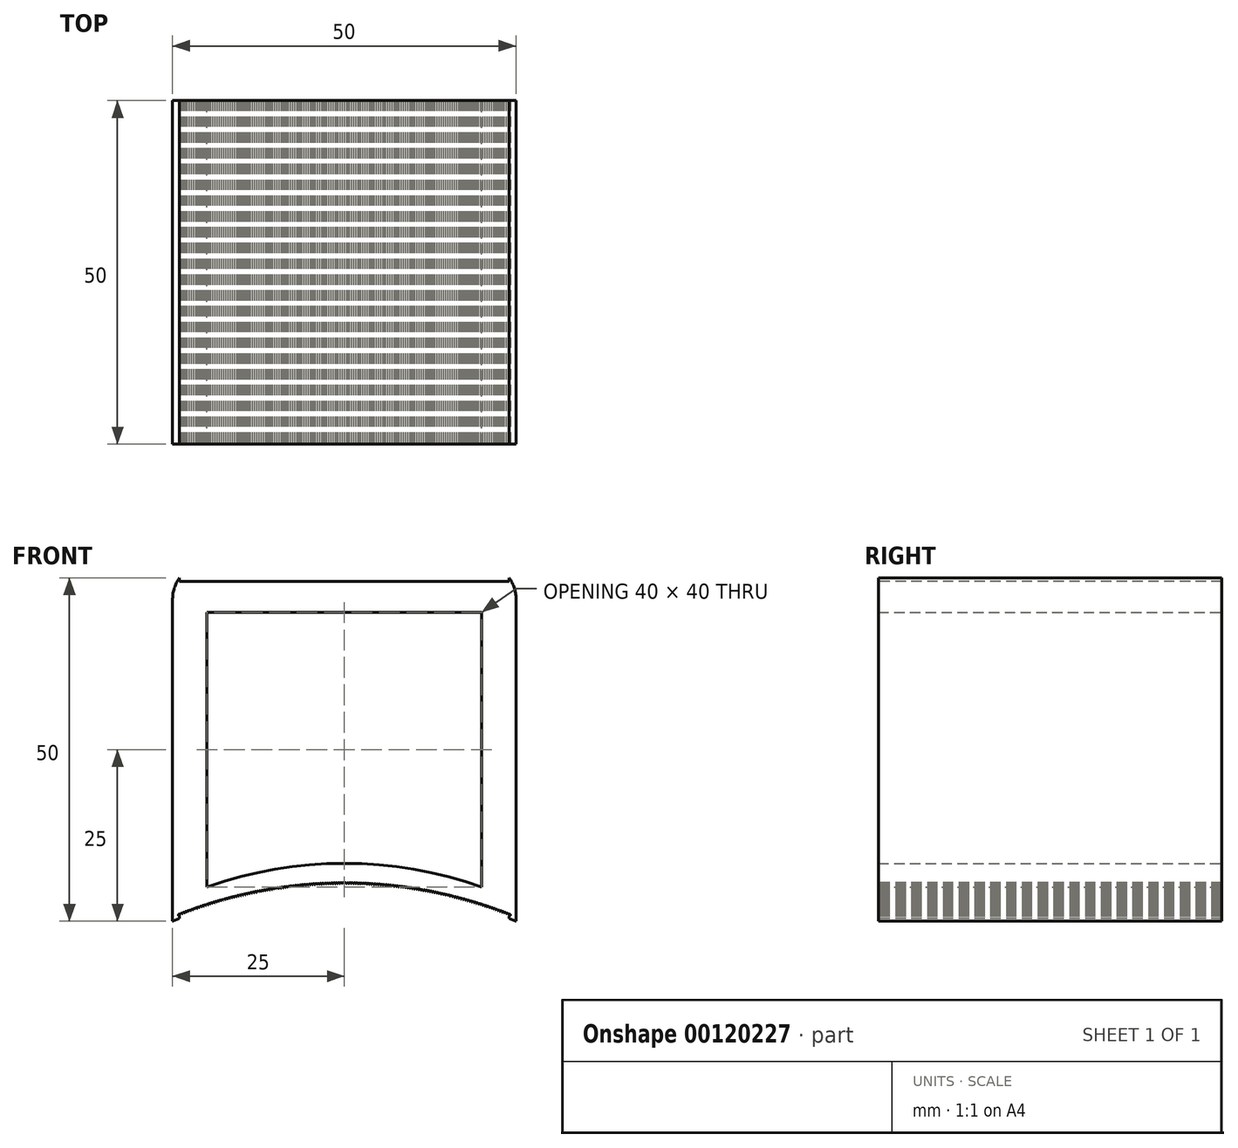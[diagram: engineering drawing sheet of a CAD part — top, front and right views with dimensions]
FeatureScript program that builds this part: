
annotation { "Feature Type Name" : "Feature", "Feature Type Description" : "" }
export const myFeature = defineFeature(function(context is Context, id is Id, definition is map)
    precondition{}
    {
        {
            var Q0;
            Q0=qCreatedBy(makeId("Front.planeOp"),FACE);
            var sketch = newSketch(context, id + "F0", { "sketchPlane" : qUnion([Q0])});
            skLineSegment(sketch, "E0.top", {"start": v(25, 25) * mm, "end": v(-25, 25) * mm});
            skLineSegment(sketch, "E0.left", {"start": v(25, -25) * mm, "end": v(25, 25) * mm});
            skLineSegment(sketch, "E0.right", {"start": v(-25, -25) * mm, "end": v(-25, 25) * mm});
            skPoint(sketch, "E0.middle", {"position": v(0, 0) * mm});
            skLineSegment(sketch, "E1.top", {"start": v(20, 20) * mm, "end": v(-20, 20) * mm});
            skLineSegment(sketch, "E1.left", {"start": v(20, -20) * mm, "end": v(20, 20) * mm});
            skLineSegment(sketch, "E1.right", {"start": v(-20, -20) * mm, "end": v(-20, 20) * mm});
            skArc(sketch, "E2", {"start": v(25, -25) * mm, "mid": v(0, -20) * mm, "end": v(-25, -25) * mm});
            skArc(sketch, "E3", {"start": v(20, -20) * mm, "mid": v(0, -16.57) * mm, "end": v(-20, -20) * mm});
            skSolve(sketch);
        }
        {
            var Q0;
            Q0=makeQuery(id+"F0.imprint","IMPRINT",FACE,{"disambiguationData":[TD([[makeQuery(id+"F0.imprint","IMPRINT",EDGE,{"derivedFrom":sQuery(id+"F0.wireOp",EDGE,"E0.top")}),1.0]])]});
            extrude(context, id + "F1", {"entities" : qUnion([Q0]), "depth" : 50 * mm});
        }
        {
            var Q0;
            Q0=makeQuery(id+"F1.opExtrude","CAP_FACE",FACE,{"disambiguationData":[OSD([sQuery(id+"F0.wireOp",EDGE,"E0.top"),sQuery(id+"F0.wireOp",EDGE,"E0.left"),sQuery(id+"F0.wireOp",EDGE,"E0.right"),sQuery(id+"F0.wireOp",EDGE,"E1.top"),sQuery(id+"F0.wireOp",EDGE,"E1.left"),sQuery(id+"F0.wireOp",EDGE,"E1.right"),sQuery(id+"F0.wireOp",EDGE,"E2"),sQuery(id+"F0.wireOp",EDGE,"E3")])],"isStart":false});
            var sketch = newSketch(context, id + "F2", { "sketchPlane" : qUnion([Q0])});
            skLineSegment(sketch, "E4", {"start": v(-24, -24.6) * mm, "end": v(-24, -24.1) * mm});
            skLineSegment(sketch, "E5", {"start": v(24, -24.6) * mm, "end": v(24, -24.1) * mm});
            skArc(sketch, "E6", {"start": v(24, -24.1) * mm, "mid": v(0, -19.54) * mm, "end": v(-24, -24.1) * mm});
            skArc(sketch, "E7", {"start": v(24, -24.6) * mm, "mid": v(0, -20) * mm, "end": v(-24, -24.6) * mm});
            skLineSegment(sketch, "E8.bottom", {"start": v(-24, 26.5) * mm, "end": v(24, 26.5) * mm});
            skLineSegment(sketch, "E8.top", {"start": v(-24, 24.5) * mm, "end": v(24, 24.5) * mm});
            skLineSegment(sketch, "E8.left", {"start": v(-24, 26.5) * mm, "end": v(-24, 24.5) * mm});
            skLineSegment(sketch, "E8.right", {"start": v(24, 26.5) * mm, "end": v(24, 24.5) * mm});
            skSolve(sketch);
        }
        {
            var Q0;
            {var subQ0=sQuery(id+"F2.wireOp",EDGE,"E8.top");Q0=makeQuery(id+"F2.imprint","IMPRINT",FACE,{"disambiguationData":[TD([[makeQuery(id+"F2.imprint","IMPRINT",EDGE,{"derivedFrom":subQ0}),1.0]])]});}
            var Q1;
            {var subQ0=sQuery(id+"F2.wireOp",EDGE,"E8.bottom");Q1=makeQuery(id+"F2.imprint","IMPRINT",FACE,{"disambiguationData":[TD([[makeQuery(id+"F2.imprint","IMPRINT",EDGE,{"derivedFrom":subQ0}),-1.0]])]});}
            var Q2;
            Q2=makeQuery(id+"F2.imprint","IMPRINT",FACE,{"disambiguationData":[TD([[makeQuery(id+"F2.imprint","IMPRINT",EDGE,{"derivedFrom":sQuery(id+"F2.wireOp",EDGE,"E4")}),-1.0]])]});
            extrude(context, id + "F3", {"entities" : qUnion([Q0, Q1, Q2]), "operationType" : NewBodyOperationType.REMOVE, "oppositeDirection" : true, "depth" : 50 * mm});
        }
        {
            var Q0;
            Q0=makeQuery(id+"F1.opExtrude","SWEPT_EDGE",EDGE,{"disambiguationData":[OSD([sQuery(id+"F0.wireOp",EDGE,"E0.top"),sQuery(id+"F0.wireOp",EDGE,"E0.left")])]});
            var Q1;
            Q1=makeQuery(id+"F1.opExtrude","SWEPT_EDGE",EDGE,{"disambiguationData":[OSD([sQuery(id+"F0.wireOp",EDGE,"E0.top"),sQuery(id+"F0.wireOp",EDGE,"E0.right")])]});
            fillet(context, id + "F4", {"entities" : qUnion([Q0, Q1]), "radius" : 5.08 * mm, "tangentPropagation" : true, "allowEdgeOverflow" : false});
        }
        {
            var Q0;
            Q0=makeQuery(id+"F1.opExtrude","CAP_FACE",FACE,{"disambiguationData":[OSD([sQuery(id+"F0.wireOp",EDGE,"E0.top"),sQuery(id+"F0.wireOp",EDGE,"E0.left"),sQuery(id+"F0.wireOp",EDGE,"E0.right"),sQuery(id+"F0.wireOp",EDGE,"E1.top"),sQuery(id+"F0.wireOp",EDGE,"E1.left"),sQuery(id+"F0.wireOp",EDGE,"E1.right"),sQuery(id+"F0.wireOp",EDGE,"E2"),sQuery(id+"F0.wireOp",EDGE,"E3")])],"isStart":false});
            var sketch = newSketch(context, id + "F5", { "sketchPlane" : qUnion([Q0])});
            skCircle(sketch, "E9", {"center": v(-24, -24.1) * mm, "radius": 0.15 * mm});
            skCircle(sketch, "E10", {"center": v(0, -85.04) * mm, "radius": 65.5 * mm, "construction": true});
            skPoint(sketch, "E10.first.point", {"position": v(-20.95, -22.98) * mm});
            skPoint(sketch, "E10.second.point", {"position": v(1.95, -19.57) * mm});
            skPoint(sketch, "E10.third.point", {"position": v(16.7, -21.7) * mm});
            skCircle(sketch, "E11.1.0", {"center": v(-23.7, -23.97) * mm, "radius": 0.15 * mm});
            skCircle(sketch, "E11.2.0", {"center": v(-23.38, -23.85) * mm, "radius": 0.15 * mm});
            skCircle(sketch, "E11.3.0", {"center": v(-23.08, -23.74) * mm, "radius": 0.15 * mm});
            skCircle(sketch, "E11.4.0", {"center": v(-22.77, -23.62) * mm, "radius": 0.15 * mm});
            skCircle(sketch, "E11.5.0", {"center": v(-22.46, -23.5) * mm, "radius": 0.15 * mm});
            skCircle(sketch, "E11.6.0", {"center": v(-22.15, -23.4) * mm, "radius": 0.15 * mm});
            skCircle(sketch, "E11.7.0", {"center": v(-21.84, -23.28) * mm, "radius": 0.15 * mm});
            skCircle(sketch, "E11.8.0", {"center": v(-21.53, -23.18) * mm, "radius": 0.15 * mm});
            skCircle(sketch, "E11.9.0", {"center": v(-21.21, -23.07) * mm, "radius": 0.15 * mm});
            skCircle(sketch, "E11.10.0", {"center": v(-20.9, -22.96) * mm, "radius": 0.15 * mm});
            skCircle(sketch, "E11.11.0", {"center": v(-20.59, -22.86) * mm, "radius": 0.15 * mm});
            skCircle(sketch, "E11.12.0", {"center": v(-20.27, -22.75) * mm, "radius": 0.15 * mm});
            skCircle(sketch, "E11.13.0", {"center": v(-19.96, -22.65) * mm, "radius": 0.15 * mm});
            skCircle(sketch, "E11.14.0", {"center": v(-19.65, -22.55) * mm, "radius": 0.15 * mm});
            skCircle(sketch, "E11.15.0", {"center": v(-19.33, -22.46) * mm, "radius": 0.15 * mm});
            skCircle(sketch, "E11.16.0", {"center": v(-19.02, -22.36) * mm, "radius": 0.15 * mm});
            skCircle(sketch, "E11.17.0", {"center": v(-18.7, -22.26) * mm, "radius": 0.15 * mm});
            skCircle(sketch, "E11.18.0", {"center": v(-18.38, -22.17) * mm, "radius": 0.15 * mm});
            skCircle(sketch, "E11.19.0", {"center": v(-18.07, -22.08) * mm, "radius": 0.15 * mm});
            skCircle(sketch, "E11.20.0", {"center": v(-17.75, -21.99) * mm, "radius": 0.15 * mm});
            skCircle(sketch, "E11.21.0", {"center": v(-17.43, -21.9) * mm, "radius": 0.15 * mm});
            skCircle(sketch, "E11.22.0", {"center": v(-17.11, -21.81) * mm, "radius": 0.15 * mm});
            skCircle(sketch, "E11.23.0", {"center": v(-16.8, -21.73) * mm, "radius": 0.15 * mm});
            skCircle(sketch, "E11.24.0", {"center": v(-16.48, -21.64) * mm, "radius": 0.15 * mm});
            skCircle(sketch, "E11.25.0", {"center": v(-16.16, -21.56) * mm, "radius": 0.15 * mm});
            skCircle(sketch, "E11.26.0", {"center": v(-15.84, -21.48) * mm, "radius": 0.15 * mm});
            skCircle(sketch, "E11.27.0", {"center": v(-15.52, -21.4) * mm, "radius": 0.15 * mm});
            skCircle(sketch, "E11.28.0", {"center": v(-15.2, -21.32) * mm, "radius": 0.15 * mm});
            skCircle(sketch, "E11.29.0", {"center": v(-14.87, -21.25) * mm, "radius": 0.15 * mm});
            skCircle(sketch, "E11.30.0", {"center": v(-14.55, -21.17) * mm, "radius": 0.15 * mm});
            skCircle(sketch, "E11.31.0", {"center": v(-14.23, -21.1) * mm, "radius": 0.15 * mm});
            skCircle(sketch, "E11.32.0", {"center": v(-13.9, -21.03) * mm, "radius": 0.15 * mm});
            skCircle(sketch, "E11.33.0", {"center": v(-13.59, -20.96) * mm, "radius": 0.15 * mm});
            skCircle(sketch, "E11.34.0", {"center": v(-13.26, -20.9) * mm, "radius": 0.15 * mm});
            skCircle(sketch, "E11.35.0", {"center": v(-12.94, -20.83) * mm, "radius": 0.15 * mm});
            skCircle(sketch, "E11.36.0", {"center": v(-12.62, -20.76) * mm, "radius": 0.15 * mm});
            skCircle(sketch, "E11.37.0", {"center": v(-12.3, -20.7) * mm, "radius": 0.15 * mm});
            skCircle(sketch, "E11.38.0", {"center": v(-11.97, -20.64) * mm, "radius": 0.15 * mm});
            skCircle(sketch, "E11.39.0", {"center": v(-11.64, -20.58) * mm, "radius": 0.15 * mm});
            skCircle(sketch, "E11.40.0", {"center": v(-11.32, -20.52) * mm, "radius": 0.15 * mm});
            skCircle(sketch, "E11.41.0", {"center": v(-11, -20.47) * mm, "radius": 0.15 * mm});
            skCircle(sketch, "E11.42.0", {"center": v(-10.67, -20.41) * mm, "radius": 0.15 * mm});
            skCircle(sketch, "E11.43.0", {"center": v(-10.34, -20.36) * mm, "radius": 0.15 * mm});
            skCircle(sketch, "E11.44.0", {"center": v(-10.02, -20.3) * mm, "radius": 0.15 * mm});
            skCircle(sketch, "E11.45.0", {"center": v(-9.7, -20.26) * mm, "radius": 0.15 * mm});
            skCircle(sketch, "E11.46.0", {"center": v(-9.36, -20.21) * mm, "radius": 0.15 * mm});
            skCircle(sketch, "E11.47.0", {"center": v(-9.04, -20.16) * mm, "radius": 0.15 * mm});
            skCircle(sketch, "E11.48.0", {"center": v(-8.71, -20.12) * mm, "radius": 0.15 * mm});
            skCircle(sketch, "E11.49.0", {"center": v(-8.38, -20.08) * mm, "radius": 0.15 * mm});
            skLineSegment(sketch, "E11.anchor1", {"start": v(0, -85.04) * mm, "end": v(-24, -24.1) * mm, "construction": true});
            skLineSegment(sketch, "E11.anchor2", {"start": v(0, -85.04) * mm, "end": v(24.01, -24.1) * mm, "construction": true});
            skCircle(sketch, "E12.1.50.0", {"center": v(-8.06, -20.04) * mm, "radius": 0.15 * mm});
            skCircle(sketch, "E12.1.51.0", {"center": v(-7.73, -20) * mm, "radius": 0.15 * mm});
            skCircle(sketch, "E12.1.52.0", {"center": v(-7.4, -19.96) * mm, "radius": 0.15 * mm});
            skCircle(sketch, "E12.1.53.0", {"center": v(-7.07, -19.92) * mm, "radius": 0.15 * mm});
            skCircle(sketch, "E12.1.54.0", {"center": v(-6.74, -19.89) * mm, "radius": 0.15 * mm});
            skCircle(sketch, "E12.1.55.0", {"center": v(-6.42, -19.85) * mm, "radius": 0.15 * mm});
            skCircle(sketch, "E12.1.56.0", {"center": v(-6.09, -19.82) * mm, "radius": 0.15 * mm});
            skCircle(sketch, "E12.1.57.0", {"center": v(-5.76, -19.8) * mm, "radius": 0.15 * mm});
            skCircle(sketch, "E12.1.58.0", {"center": v(-5.43, -19.76) * mm, "radius": 0.15 * mm});
            skCircle(sketch, "E12.1.59.0", {"center": v(-5.1, -19.74) * mm, "radius": 0.15 * mm});
            skCircle(sketch, "E12.1.60.0", {"center": v(-4.77, -19.71) * mm, "radius": 0.15 * mm});
            skCircle(sketch, "E12.1.61.0", {"center": v(-4.44, -19.69) * mm, "radius": 0.15 * mm});
            skCircle(sketch, "E12.1.62.0", {"center": v(-4.11, -19.67) * mm, "radius": 0.15 * mm});
            skCircle(sketch, "E12.1.63.0", {"center": v(-3.79, -19.65) * mm, "radius": 0.15 * mm});
            skCircle(sketch, "E12.1.64.0", {"center": v(-3.46, -19.63) * mm, "radius": 0.15 * mm});
            skCircle(sketch, "E12.1.65.0", {"center": v(-3.13, -19.61) * mm, "radius": 0.15 * mm});
            skCircle(sketch, "E12.1.66.0", {"center": v(-2.8, -19.6) * mm, "radius": 0.15 * mm});
            skCircle(sketch, "E12.1.67.0", {"center": v(-2.47, -19.58) * mm, "radius": 0.15 * mm});
            skCircle(sketch, "E12.1.68.0", {"center": v(-2.14, -19.57) * mm, "radius": 0.15 * mm});
            skCircle(sketch, "E12.1.69.0", {"center": v(-1.8, -19.56) * mm, "radius": 0.15 * mm});
            skCircle(sketch, "E12.1.70.0", {"center": v(-1.48, -19.55) * mm, "radius": 0.15 * mm});
            skCircle(sketch, "E12.1.71.0", {"center": v(-1.15, -19.55) * mm, "radius": 0.15 * mm});
            skCircle(sketch, "E12.1.72.0", {"center": v(-0.82, -19.54) * mm, "radius": 0.15 * mm});
            skCircle(sketch, "E12.1.73.0", {"center": v(-0.49, -19.54) * mm, "radius": 0.15 * mm});
            skCircle(sketch, "E12.1.74.0", {"center": v(-0.16, -19.54) * mm, "radius": 0.15 * mm});
            skCircle(sketch, "E12.1.75.0", {"center": v(0.17, -19.54) * mm, "radius": 0.15 * mm});
            skCircle(sketch, "E12.1.76.0", {"center": v(0.5, -19.54) * mm, "radius": 0.15 * mm});
            skCircle(sketch, "E12.1.77.0", {"center": v(0.83, -19.54) * mm, "radius": 0.15 * mm});
            skCircle(sketch, "E12.1.78.0", {"center": v(1.16, -19.55) * mm, "radius": 0.15 * mm});
            skCircle(sketch, "E12.1.79.0", {"center": v(1.5, -19.55) * mm, "radius": 0.15 * mm});
            skCircle(sketch, "E12.1.80.0", {"center": v(1.82, -19.56) * mm, "radius": 0.15 * mm});
            skCircle(sketch, "E12.1.81.0", {"center": v(2.15, -19.57) * mm, "radius": 0.15 * mm});
            skCircle(sketch, "E12.1.82.0", {"center": v(2.48, -19.58) * mm, "radius": 0.15 * mm});
            skCircle(sketch, "E12.1.83.0", {"center": v(2.8, -19.6) * mm, "radius": 0.15 * mm});
            skCircle(sketch, "E12.1.84.0", {"center": v(3.14, -19.61) * mm, "radius": 0.15 * mm});
            skCircle(sketch, "E12.1.85.0", {"center": v(3.47, -19.63) * mm, "radius": 0.15 * mm});
            skCircle(sketch, "E12.1.86.0", {"center": v(3.8, -19.65) * mm, "radius": 0.15 * mm});
            skCircle(sketch, "E12.1.87.0", {"center": v(4.13, -19.67) * mm, "radius": 0.15 * mm});
            skCircle(sketch, "E12.1.88.0", {"center": v(4.46, -19.69) * mm, "radius": 0.15 * mm});
            skCircle(sketch, "E12.1.89.0", {"center": v(4.79, -19.71) * mm, "radius": 0.15 * mm});
            skCircle(sketch, "E12.1.90.0", {"center": v(5.11, -19.74) * mm, "radius": 0.15 * mm});
            skCircle(sketch, "E12.1.91.0", {"center": v(5.44, -19.76) * mm, "radius": 0.15 * mm});
            skCircle(sketch, "E12.1.92.0", {"center": v(5.77, -19.8) * mm, "radius": 0.15 * mm});
            skCircle(sketch, "E12.1.93.0", {"center": v(6.1, -19.82) * mm, "radius": 0.15 * mm});
            skCircle(sketch, "E12.1.94.0", {"center": v(6.43, -19.85) * mm, "radius": 0.15 * mm});
            skCircle(sketch, "E12.1.95.0", {"center": v(6.76, -19.89) * mm, "radius": 0.15 * mm});
            skCircle(sketch, "E12.1.96.0", {"center": v(7.09, -19.92) * mm, "radius": 0.15 * mm});
            skCircle(sketch, "E12.1.97.0", {"center": v(7.41, -19.96) * mm, "radius": 0.15 * mm});
            skCircle(sketch, "E12.1.98.0", {"center": v(7.74, -20) * mm, "radius": 0.15 * mm});
            skCircle(sketch, "E12.1.99.0", {"center": v(8.07, -20.04) * mm, "radius": 0.15 * mm});
            skCircle(sketch, "E12.1.100.0", {"center": v(8.4, -20.08) * mm, "radius": 0.15 * mm});
            skCircle(sketch, "E12.1.101.0", {"center": v(8.72, -20.12) * mm, "radius": 0.15 * mm});
            skCircle(sketch, "E12.1.102.0", {"center": v(9.05, -20.17) * mm, "radius": 0.15 * mm});
            skCircle(sketch, "E12.1.103.0", {"center": v(9.38, -20.21) * mm, "radius": 0.15 * mm});
            skCircle(sketch, "E12.1.104.0", {"center": v(9.7, -20.26) * mm, "radius": 0.15 * mm});
            skCircle(sketch, "E12.1.105.0", {"center": v(10.03, -20.31) * mm, "radius": 0.15 * mm});
            skCircle(sketch, "E12.1.106.0", {"center": v(10.35, -20.36) * mm, "radius": 0.15 * mm});
            skCircle(sketch, "E12.1.107.0", {"center": v(10.68, -20.41) * mm, "radius": 0.15 * mm});
            skCircle(sketch, "E12.1.108.0", {"center": v(11, -20.47) * mm, "radius": 0.15 * mm});
            skCircle(sketch, "E12.1.109.0", {"center": v(11.33, -20.53) * mm, "radius": 0.15 * mm});
            skCircle(sketch, "E12.1.110.0", {"center": v(11.66, -20.58) * mm, "radius": 0.15 * mm});
            skCircle(sketch, "E12.1.111.0", {"center": v(11.98, -20.64) * mm, "radius": 0.15 * mm});
            skCircle(sketch, "E12.1.112.0", {"center": v(12.3, -20.7) * mm, "radius": 0.15 * mm});
            skCircle(sketch, "E12.1.113.0", {"center": v(12.63, -20.77) * mm, "radius": 0.15 * mm});
            skCircle(sketch, "E12.1.114.0", {"center": v(12.95, -20.83) * mm, "radius": 0.15 * mm});
            skCircle(sketch, "E12.1.115.0", {"center": v(13.28, -20.9) * mm, "radius": 0.15 * mm});
            skCircle(sketch, "E12.1.116.0", {"center": v(13.6, -20.96) * mm, "radius": 0.15 * mm});
            skCircle(sketch, "E12.1.117.0", {"center": v(13.92, -21.03) * mm, "radius": 0.15 * mm});
            skCircle(sketch, "E12.1.118.0", {"center": v(14.24, -21.1) * mm, "radius": 0.15 * mm});
            skCircle(sketch, "E12.1.119.0", {"center": v(14.56, -21.18) * mm, "radius": 0.15 * mm});
            skCircle(sketch, "E12.1.120.0", {"center": v(14.89, -21.25) * mm, "radius": 0.15 * mm});
            skCircle(sketch, "E12.1.121.0", {"center": v(15.2, -21.33) * mm, "radius": 0.15 * mm});
            skCircle(sketch, "E12.1.122.0", {"center": v(15.53, -21.4) * mm, "radius": 0.15 * mm});
            skCircle(sketch, "E12.1.123.0", {"center": v(15.85, -21.48) * mm, "radius": 0.15 * mm});
            skCircle(sketch, "E12.1.124.0", {"center": v(16.17, -21.56) * mm, "radius": 0.15 * mm});
            skCircle(sketch, "E12.1.125.0", {"center": v(16.49, -21.65) * mm, "radius": 0.15 * mm});
            skCircle(sketch, "E12.1.126.0", {"center": v(16.8, -21.73) * mm, "radius": 0.15 * mm});
            skCircle(sketch, "E12.1.127.0", {"center": v(17.13, -21.82) * mm, "radius": 0.15 * mm});
            skCircle(sketch, "E12.1.128.0", {"center": v(17.44, -21.9) * mm, "radius": 0.15 * mm});
            skCircle(sketch, "E12.1.129.0", {"center": v(17.76, -22) * mm, "radius": 0.15 * mm});
            skCircle(sketch, "E12.1.130.0", {"center": v(18.08, -22.08) * mm, "radius": 0.15 * mm});
            skCircle(sketch, "E12.1.131.0", {"center": v(18.4, -22.17) * mm, "radius": 0.15 * mm});
            skCircle(sketch, "E12.1.132.0", {"center": v(18.71, -22.27) * mm, "radius": 0.15 * mm});
            skCircle(sketch, "E12.1.133.0", {"center": v(19.03, -22.36) * mm, "radius": 0.15 * mm});
            skCircle(sketch, "E12.1.134.0", {"center": v(19.34, -22.46) * mm, "radius": 0.15 * mm});
            skCircle(sketch, "E12.1.135.0", {"center": v(19.66, -22.56) * mm, "radius": 0.15 * mm});
            skCircle(sketch, "E12.1.136.0", {"center": v(19.97, -22.66) * mm, "radius": 0.15 * mm});
            skCircle(sketch, "E12.1.137.0", {"center": v(20.29, -22.76) * mm, "radius": 0.15 * mm});
            skCircle(sketch, "E12.1.138.0", {"center": v(20.6, -22.86) * mm, "radius": 0.15 * mm});
            skCircle(sketch, "E12.1.139.0", {"center": v(20.91, -22.97) * mm, "radius": 0.15 * mm});
            skCircle(sketch, "E12.1.140.0", {"center": v(21.23, -23.07) * mm, "radius": 0.15 * mm});
            skCircle(sketch, "E12.1.141.0", {"center": v(21.54, -23.18) * mm, "radius": 0.15 * mm});
            skCircle(sketch, "E12.1.142.0", {"center": v(21.85, -23.29) * mm, "radius": 0.15 * mm});
            skCircle(sketch, "E12.1.143.0", {"center": v(22.16, -23.4) * mm, "radius": 0.15 * mm});
            skCircle(sketch, "E12.1.144.0", {"center": v(22.47, -23.51) * mm, "radius": 0.15 * mm});
            skCircle(sketch, "E12.1.145.0", {"center": v(22.78, -23.63) * mm, "radius": 0.15 * mm});
            skCircle(sketch, "E12.1.146.0", {"center": v(23.09, -23.74) * mm, "radius": 0.15 * mm});
            skCircle(sketch, "E12.1.147.0", {"center": v(23.4, -23.86) * mm, "radius": 0.15 * mm});
            skCircle(sketch, "E12.1.148.0", {"center": v(23.7, -23.98) * mm, "radius": 0.15 * mm});
            skCircle(sketch, "E12.1.149.0", {"center": v(24.01, -24.1) * mm, "radius": 0.15 * mm});
            skSolve(sketch);
        }
        {
            var Q0;
            {var subQ0=sQuery(id+"F5.wireOp",EDGE,"E11.4.0");var subQ1=makeQuery(id+"F3.boolean.opBoolean","COPY",EDGE,{"derivedFrom":makeQuery(id+"F3.opExtrude","CAP_EDGE",EDGE,{"disambiguationData":[OSD([sQuery(id+"F2.wireOp",EDGE,"E6")])],"isStart":true})});var subQ2=makeQuery(id+"F5.imprint","INTERSECT",VERTEX,{"disambiguationData":[OD(0.0)],"derivedFrom":[subQ1,subQ0]});Q0=makeQuery(id+"F5.imprint","IMPRINT",FACE,{"disambiguationData":[TD([[makeQuery(id+"F5.imprint","IMPRINT",EDGE,{"disambiguationData":[TD([[subQ2,-1.0]])],"derivedFrom":subQ0}),1.0]])]});}
            var Q1;
            {var subQ0=sQuery(id+"F5.wireOp",EDGE,"E11.3.0");var subQ1=makeQuery(id+"F3.boolean.opBoolean","COPY",EDGE,{"derivedFrom":makeQuery(id+"F3.opExtrude","CAP_EDGE",EDGE,{"disambiguationData":[OSD([sQuery(id+"F2.wireOp",EDGE,"E6")])],"isStart":true})});var subQ2=makeQuery(id+"F5.imprint","INTERSECT",VERTEX,{"disambiguationData":[OD(0.0)],"derivedFrom":[subQ1,subQ0]});Q1=makeQuery(id+"F5.imprint","IMPRINT",FACE,{"disambiguationData":[TD([[makeQuery(id+"F5.imprint","IMPRINT",EDGE,{"disambiguationData":[TD([[subQ2,-1.0]])],"derivedFrom":subQ0}),1.0]])]});}
            var Q2;
            {var subQ0=sQuery(id+"F5.wireOp",EDGE,"E11.2.0");var subQ1=makeQuery(id+"F3.boolean.opBoolean","COPY",EDGE,{"derivedFrom":makeQuery(id+"F3.opExtrude","CAP_EDGE",EDGE,{"disambiguationData":[OSD([sQuery(id+"F2.wireOp",EDGE,"E6")])],"isStart":true})});var subQ2=makeQuery(id+"F5.imprint","INTERSECT",VERTEX,{"disambiguationData":[OD(0.0)],"derivedFrom":[subQ1,subQ0]});Q2=makeQuery(id+"F5.imprint","IMPRINT",FACE,{"disambiguationData":[TD([[makeQuery(id+"F5.imprint","IMPRINT",EDGE,{"disambiguationData":[TD([[subQ2,-1.0]])],"derivedFrom":subQ0}),1.0]])]});}
            var Q3;
            {var subQ0=sQuery(id+"F5.wireOp",EDGE,"E11.1.0");var subQ1=makeQuery(id+"F3.boolean.opBoolean","COPY",EDGE,{"derivedFrom":makeQuery(id+"F3.opExtrude","CAP_EDGE",EDGE,{"disambiguationData":[OSD([sQuery(id+"F2.wireOp",EDGE,"E6")])],"isStart":true})});var subQ2=makeQuery(id+"F5.imprint","INTERSECT",VERTEX,{"disambiguationData":[OD(0.0)],"derivedFrom":[subQ1,subQ0]});Q3=makeQuery(id+"F5.imprint","IMPRINT",FACE,{"disambiguationData":[TD([[makeQuery(id+"F5.imprint","IMPRINT",EDGE,{"disambiguationData":[TD([[subQ2,-1.0]])],"derivedFrom":subQ0}),1.0]])]});}
            var Q4;
            {var subQ0=sQuery(id+"F5.wireOp",EDGE,"E11.1.0");var subQ1=makeQuery(id+"F3.boolean.opBoolean","COPY",EDGE,{"derivedFrom":makeQuery(id+"F3.opExtrude","CAP_EDGE",EDGE,{"disambiguationData":[OSD([sQuery(id+"F2.wireOp",EDGE,"E6")])],"isStart":true})});var subQ2=makeQuery(id+"F5.imprint","INTERSECT",VERTEX,{"disambiguationData":[OD(0.0)],"derivedFrom":[subQ1,subQ0]});Q4=makeQuery(id+"F5.imprint","IMPRINT",FACE,{"disambiguationData":[TD([[makeQuery(id+"F5.imprint","IMPRINT",EDGE,{"disambiguationData":[TD([[subQ2,1.0]])],"derivedFrom":subQ0}),1.0]])]});}
            var Q5;
            {var subQ0=sQuery(id+"F5.wireOp",EDGE,"E11.2.0");var subQ1=makeQuery(id+"F3.boolean.opBoolean","COPY",EDGE,{"derivedFrom":makeQuery(id+"F3.opExtrude","CAP_EDGE",EDGE,{"disambiguationData":[OSD([sQuery(id+"F2.wireOp",EDGE,"E6")])],"isStart":true})});var subQ2=makeQuery(id+"F5.imprint","INTERSECT",VERTEX,{"disambiguationData":[OD(0.0)],"derivedFrom":[subQ1,subQ0]});Q5=makeQuery(id+"F5.imprint","IMPRINT",FACE,{"disambiguationData":[TD([[makeQuery(id+"F5.imprint","IMPRINT",EDGE,{"disambiguationData":[TD([[subQ2,1.0]])],"derivedFrom":subQ0}),1.0]])]});}
            var Q6;
            {var subQ0=sQuery(id+"F5.wireOp",EDGE,"E11.3.0");var subQ1=makeQuery(id+"F3.boolean.opBoolean","COPY",EDGE,{"derivedFrom":makeQuery(id+"F3.opExtrude","CAP_EDGE",EDGE,{"disambiguationData":[OSD([sQuery(id+"F2.wireOp",EDGE,"E6")])],"isStart":true})});var subQ2=makeQuery(id+"F5.imprint","INTERSECT",VERTEX,{"disambiguationData":[OD(0.0)],"derivedFrom":[subQ1,subQ0]});Q6=makeQuery(id+"F5.imprint","IMPRINT",FACE,{"disambiguationData":[TD([[makeQuery(id+"F5.imprint","IMPRINT",EDGE,{"disambiguationData":[TD([[subQ2,1.0]])],"derivedFrom":subQ0}),1.0]])]});}
            var Q7;
            {var subQ0=sQuery(id+"F5.wireOp",EDGE,"E9");var subQ1=makeQuery(id+"F3.boolean.opBoolean","COPY",EDGE,{"derivedFrom":makeQuery(id+"F3.opExtrude","CAP_EDGE",EDGE,{"disambiguationData":[OSD([sQuery(id+"F2.wireOp",EDGE,"E4")])],"isStart":true})});var subQ2=makeQuery(id+"F5.imprint","INTERSECT",VERTEX,{"derivedFrom":[subQ1,subQ0]});Q7=makeQuery(id+"F5.imprint","IMPRINT",FACE,{"disambiguationData":[TD([[makeQuery(id+"F5.imprint","IMPRINT",EDGE,{"disambiguationData":[TD([[subQ2,-1.0]])],"derivedFrom":subQ0}),1.0]])]});}
            var Q8;
            {var subQ0=sQuery(id+"F5.wireOp",EDGE,"E9");var subQ1=makeQuery(id+"F3.boolean.opBoolean","COPY",EDGE,{"derivedFrom":makeQuery(id+"F3.opExtrude","CAP_EDGE",EDGE,{"disambiguationData":[OSD([sQuery(id+"F2.wireOp",EDGE,"E4")])],"isStart":true})});var subQ2=makeQuery(id+"F5.imprint","INTERSECT",VERTEX,{"derivedFrom":[subQ1,subQ0]});Q8=makeQuery(id+"F5.imprint","IMPRINT",FACE,{"disambiguationData":[TD([[makeQuery(id+"F5.imprint","IMPRINT",EDGE,{"disambiguationData":[TD([[subQ2,1.0]])],"derivedFrom":subQ0}),1.0]])]});}
            var Q9;
            {var subQ0=sQuery(id+"F5.wireOp",EDGE,"E11.13.0");var subQ1=makeQuery(id+"F3.boolean.opBoolean","COPY",EDGE,{"derivedFrom":makeQuery(id+"F3.opExtrude","CAP_EDGE",EDGE,{"disambiguationData":[OSD([sQuery(id+"F2.wireOp",EDGE,"E6")])],"isStart":true})});var subQ2=makeQuery(id+"F5.imprint","INTERSECT",VERTEX,{"disambiguationData":[OD(0.0)],"derivedFrom":[subQ1,subQ0]});Q9=makeQuery(id+"F5.imprint","IMPRINT",FACE,{"disambiguationData":[TD([[makeQuery(id+"F5.imprint","IMPRINT",EDGE,{"disambiguationData":[TD([[subQ2,1.0]])],"derivedFrom":subQ0}),1.0]])]});}
            var Q10;
            {var subQ0=sQuery(id+"F5.wireOp",EDGE,"E11.14.0");var subQ1=makeQuery(id+"F3.boolean.opBoolean","COPY",EDGE,{"derivedFrom":makeQuery(id+"F3.opExtrude","CAP_EDGE",EDGE,{"disambiguationData":[OSD([sQuery(id+"F2.wireOp",EDGE,"E6")])],"isStart":true})});var subQ2=makeQuery(id+"F5.imprint","INTERSECT",VERTEX,{"disambiguationData":[OD(0.0)],"derivedFrom":[subQ1,subQ0]});Q10=makeQuery(id+"F5.imprint","IMPRINT",FACE,{"disambiguationData":[TD([[makeQuery(id+"F5.imprint","IMPRINT",EDGE,{"disambiguationData":[TD([[subQ2,1.0]])],"derivedFrom":subQ0}),1.0]])]});}
            var Q11;
            {var subQ0=sQuery(id+"F5.wireOp",EDGE,"E11.30.0");var subQ1=makeQuery(id+"F3.boolean.opBoolean","COPY",EDGE,{"derivedFrom":makeQuery(id+"F3.opExtrude","CAP_EDGE",EDGE,{"disambiguationData":[OSD([sQuery(id+"F2.wireOp",EDGE,"E6")])],"isStart":true})});var subQ2=makeQuery(id+"F5.imprint","INTERSECT",VERTEX,{"disambiguationData":[OD(0.0)],"derivedFrom":[subQ1,subQ0]});Q11=makeQuery(id+"F5.imprint","IMPRINT",FACE,{"disambiguationData":[TD([[makeQuery(id+"F5.imprint","IMPRINT",EDGE,{"disambiguationData":[TD([[subQ2,-1.0]])],"derivedFrom":subQ0}),1.0]])]});}
            var Q12;
            {var subQ0=sQuery(id+"F5.wireOp",EDGE,"E11.13.0");var subQ1=makeQuery(id+"F3.boolean.opBoolean","COPY",EDGE,{"derivedFrom":makeQuery(id+"F3.opExtrude","CAP_EDGE",EDGE,{"disambiguationData":[OSD([sQuery(id+"F2.wireOp",EDGE,"E6")])],"isStart":true})});var subQ2=makeQuery(id+"F5.imprint","INTERSECT",VERTEX,{"disambiguationData":[OD(0.0)],"derivedFrom":[subQ1,subQ0]});Q12=makeQuery(id+"F5.imprint","IMPRINT",FACE,{"disambiguationData":[TD([[makeQuery(id+"F5.imprint","IMPRINT",EDGE,{"disambiguationData":[TD([[subQ2,-1.0]])],"derivedFrom":subQ0}),1.0]])]});}
            var Q13;
            {var subQ0=sQuery(id+"F5.wireOp",EDGE,"E11.15.0");var subQ1=makeQuery(id+"F3.boolean.opBoolean","COPY",EDGE,{"derivedFrom":makeQuery(id+"F3.opExtrude","CAP_EDGE",EDGE,{"disambiguationData":[OSD([sQuery(id+"F2.wireOp",EDGE,"E6")])],"isStart":true})});var subQ2=makeQuery(id+"F5.imprint","INTERSECT",VERTEX,{"disambiguationData":[OD(0.0)],"derivedFrom":[subQ1,subQ0]});Q13=makeQuery(id+"F5.imprint","IMPRINT",FACE,{"disambiguationData":[TD([[makeQuery(id+"F5.imprint","IMPRINT",EDGE,{"disambiguationData":[TD([[subQ2,1.0]])],"derivedFrom":subQ0}),1.0]])]});}
            var Q14;
            {var subQ0=sQuery(id+"F5.wireOp",EDGE,"E11.18.0");var subQ1=makeQuery(id+"F3.boolean.opBoolean","COPY",EDGE,{"derivedFrom":makeQuery(id+"F3.opExtrude","CAP_EDGE",EDGE,{"disambiguationData":[OSD([sQuery(id+"F2.wireOp",EDGE,"E6")])],"isStart":true})});var subQ2=makeQuery(id+"F5.imprint","INTERSECT",VERTEX,{"disambiguationData":[OD(0.0)],"derivedFrom":[subQ1,subQ0]});Q14=makeQuery(id+"F5.imprint","IMPRINT",FACE,{"disambiguationData":[TD([[makeQuery(id+"F5.imprint","IMPRINT",EDGE,{"disambiguationData":[TD([[subQ2,1.0]])],"derivedFrom":subQ0}),1.0]])]});}
            var Q15;
            {var subQ0=sQuery(id+"F5.wireOp",EDGE,"E11.35.0");var subQ1=makeQuery(id+"F3.boolean.opBoolean","COPY",EDGE,{"derivedFrom":makeQuery(id+"F3.opExtrude","CAP_EDGE",EDGE,{"disambiguationData":[OSD([sQuery(id+"F2.wireOp",EDGE,"E6")])],"isStart":true})});var subQ2=makeQuery(id+"F5.imprint","INTERSECT",VERTEX,{"disambiguationData":[OD(0.0)],"derivedFrom":[subQ1,subQ0]});Q15=makeQuery(id+"F5.imprint","IMPRINT",FACE,{"disambiguationData":[TD([[makeQuery(id+"F5.imprint","IMPRINT",EDGE,{"disambiguationData":[TD([[subQ2,1.0]])],"derivedFrom":subQ0}),1.0]])]});}
            var Q16;
            {var subQ0=sQuery(id+"F5.wireOp",EDGE,"E11.24.0");var subQ1=makeQuery(id+"F3.boolean.opBoolean","COPY",EDGE,{"derivedFrom":makeQuery(id+"F3.opExtrude","CAP_EDGE",EDGE,{"disambiguationData":[OSD([sQuery(id+"F2.wireOp",EDGE,"E6")])],"isStart":true})});var subQ2=makeQuery(id+"F5.imprint","INTERSECT",VERTEX,{"disambiguationData":[OD(0.0)],"derivedFrom":[subQ1,subQ0]});Q16=makeQuery(id+"F5.imprint","IMPRINT",FACE,{"disambiguationData":[TD([[makeQuery(id+"F5.imprint","IMPRINT",EDGE,{"disambiguationData":[TD([[subQ2,-1.0]])],"derivedFrom":subQ0}),1.0]])]});}
            var Q17;
            {var subQ0=sQuery(id+"F5.wireOp",EDGE,"E11.21.0");var subQ1=makeQuery(id+"F3.boolean.opBoolean","COPY",EDGE,{"derivedFrom":makeQuery(id+"F3.opExtrude","CAP_EDGE",EDGE,{"disambiguationData":[OSD([sQuery(id+"F2.wireOp",EDGE,"E6")])],"isStart":true})});var subQ2=makeQuery(id+"F5.imprint","INTERSECT",VERTEX,{"disambiguationData":[OD(0.0)],"derivedFrom":[subQ1,subQ0]});Q17=makeQuery(id+"F5.imprint","IMPRINT",FACE,{"disambiguationData":[TD([[makeQuery(id+"F5.imprint","IMPRINT",EDGE,{"disambiguationData":[TD([[subQ2,1.0]])],"derivedFrom":subQ0}),1.0]])]});}
            var Q18;
            {var subQ0=sQuery(id+"F5.wireOp",EDGE,"E11.22.0");var subQ1=makeQuery(id+"F3.boolean.opBoolean","COPY",EDGE,{"derivedFrom":makeQuery(id+"F3.opExtrude","CAP_EDGE",EDGE,{"disambiguationData":[OSD([sQuery(id+"F2.wireOp",EDGE,"E6")])],"isStart":true})});var subQ2=makeQuery(id+"F5.imprint","INTERSECT",VERTEX,{"disambiguationData":[OD(0.0)],"derivedFrom":[subQ1,subQ0]});Q18=makeQuery(id+"F5.imprint","IMPRINT",FACE,{"disambiguationData":[TD([[makeQuery(id+"F5.imprint","IMPRINT",EDGE,{"disambiguationData":[TD([[subQ2,1.0]])],"derivedFrom":subQ0}),1.0]])]});}
            var Q19;
            {var subQ0=sQuery(id+"F5.wireOp",EDGE,"E11.29.0");var subQ1=makeQuery(id+"F3.boolean.opBoolean","COPY",EDGE,{"derivedFrom":makeQuery(id+"F3.opExtrude","CAP_EDGE",EDGE,{"disambiguationData":[OSD([sQuery(id+"F2.wireOp",EDGE,"E6")])],"isStart":true})});var subQ2=makeQuery(id+"F5.imprint","INTERSECT",VERTEX,{"disambiguationData":[OD(0.0)],"derivedFrom":[subQ1,subQ0]});Q19=makeQuery(id+"F5.imprint","IMPRINT",FACE,{"disambiguationData":[TD([[makeQuery(id+"F5.imprint","IMPRINT",EDGE,{"disambiguationData":[TD([[subQ2,1.0]])],"derivedFrom":subQ0}),1.0]])]});}
            var Q20;
            {var subQ0=sQuery(id+"F5.wireOp",EDGE,"E11.9.0");var subQ1=makeQuery(id+"F3.boolean.opBoolean","COPY",EDGE,{"derivedFrom":makeQuery(id+"F3.opExtrude","CAP_EDGE",EDGE,{"disambiguationData":[OSD([sQuery(id+"F2.wireOp",EDGE,"E6")])],"isStart":true})});var subQ2=makeQuery(id+"F5.imprint","INTERSECT",VERTEX,{"disambiguationData":[OD(0.0)],"derivedFrom":[subQ1,subQ0]});Q20=makeQuery(id+"F5.imprint","IMPRINT",FACE,{"disambiguationData":[TD([[makeQuery(id+"F5.imprint","IMPRINT",EDGE,{"disambiguationData":[TD([[subQ2,-1.0]])],"derivedFrom":subQ0}),1.0]])]});}
            var Q21;
            {var subQ0=sQuery(id+"F5.wireOp",EDGE,"E11.6.0");var subQ1=makeQuery(id+"F3.boolean.opBoolean","COPY",EDGE,{"derivedFrom":makeQuery(id+"F3.opExtrude","CAP_EDGE",EDGE,{"disambiguationData":[OSD([sQuery(id+"F2.wireOp",EDGE,"E6")])],"isStart":true})});var subQ2=makeQuery(id+"F5.imprint","INTERSECT",VERTEX,{"disambiguationData":[OD(0.0)],"derivedFrom":[subQ1,subQ0]});Q21=makeQuery(id+"F5.imprint","IMPRINT",FACE,{"disambiguationData":[TD([[makeQuery(id+"F5.imprint","IMPRINT",EDGE,{"disambiguationData":[TD([[subQ2,-1.0]])],"derivedFrom":subQ0}),1.0]])]});}
            var Q22;
            {var subQ0=sQuery(id+"F5.wireOp",EDGE,"E11.7.0");var subQ1=makeQuery(id+"F3.boolean.opBoolean","COPY",EDGE,{"derivedFrom":makeQuery(id+"F3.opExtrude","CAP_EDGE",EDGE,{"disambiguationData":[OSD([sQuery(id+"F2.wireOp",EDGE,"E6")])],"isStart":true})});var subQ2=makeQuery(id+"F5.imprint","INTERSECT",VERTEX,{"disambiguationData":[OD(0.0)],"derivedFrom":[subQ1,subQ0]});Q22=makeQuery(id+"F5.imprint","IMPRINT",FACE,{"disambiguationData":[TD([[makeQuery(id+"F5.imprint","IMPRINT",EDGE,{"disambiguationData":[TD([[subQ2,-1.0]])],"derivedFrom":subQ0}),1.0]])]});}
            var Q23;
            {var subQ0=sQuery(id+"F5.wireOp",EDGE,"E11.11.0");var subQ1=makeQuery(id+"F3.boolean.opBoolean","COPY",EDGE,{"derivedFrom":makeQuery(id+"F3.opExtrude","CAP_EDGE",EDGE,{"disambiguationData":[OSD([sQuery(id+"F2.wireOp",EDGE,"E6")])],"isStart":true})});var subQ2=makeQuery(id+"F5.imprint","INTERSECT",VERTEX,{"disambiguationData":[OD(0.0)],"derivedFrom":[subQ1,subQ0]});Q23=makeQuery(id+"F5.imprint","IMPRINT",FACE,{"disambiguationData":[TD([[makeQuery(id+"F5.imprint","IMPRINT",EDGE,{"disambiguationData":[TD([[subQ2,-1.0]])],"derivedFrom":subQ0}),1.0]])]});}
            var Q24;
            {var subQ0=sQuery(id+"F5.wireOp",EDGE,"E11.12.0");var subQ1=makeQuery(id+"F3.boolean.opBoolean","COPY",EDGE,{"derivedFrom":makeQuery(id+"F3.opExtrude","CAP_EDGE",EDGE,{"disambiguationData":[OSD([sQuery(id+"F2.wireOp",EDGE,"E6")])],"isStart":true})});var subQ2=makeQuery(id+"F5.imprint","INTERSECT",VERTEX,{"disambiguationData":[OD(0.0)],"derivedFrom":[subQ1,subQ0]});Q24=makeQuery(id+"F5.imprint","IMPRINT",FACE,{"disambiguationData":[TD([[makeQuery(id+"F5.imprint","IMPRINT",EDGE,{"disambiguationData":[TD([[subQ2,-1.0]])],"derivedFrom":subQ0}),1.0]])]});}
            var Q25;
            {var subQ0=sQuery(id+"F5.wireOp",EDGE,"E11.18.0");var subQ1=makeQuery(id+"F3.boolean.opBoolean","COPY",EDGE,{"derivedFrom":makeQuery(id+"F3.opExtrude","CAP_EDGE",EDGE,{"disambiguationData":[OSD([sQuery(id+"F2.wireOp",EDGE,"E6")])],"isStart":true})});var subQ2=makeQuery(id+"F5.imprint","INTERSECT",VERTEX,{"disambiguationData":[OD(0.0)],"derivedFrom":[subQ1,subQ0]});Q25=makeQuery(id+"F5.imprint","IMPRINT",FACE,{"disambiguationData":[TD([[makeQuery(id+"F5.imprint","IMPRINT",EDGE,{"disambiguationData":[TD([[subQ2,-1.0]])],"derivedFrom":subQ0}),1.0]])]});}
            var Q26;
            {var subQ0=sQuery(id+"F5.wireOp",EDGE,"E11.34.0");var subQ1=makeQuery(id+"F3.boolean.opBoolean","COPY",EDGE,{"derivedFrom":makeQuery(id+"F3.opExtrude","CAP_EDGE",EDGE,{"disambiguationData":[OSD([sQuery(id+"F2.wireOp",EDGE,"E6")])],"isStart":true})});var subQ2=makeQuery(id+"F5.imprint","INTERSECT",VERTEX,{"disambiguationData":[OD(0.0)],"derivedFrom":[subQ1,subQ0]});Q26=makeQuery(id+"F5.imprint","IMPRINT",FACE,{"disambiguationData":[TD([[makeQuery(id+"F5.imprint","IMPRINT",EDGE,{"disambiguationData":[TD([[subQ2,-1.0]])],"derivedFrom":subQ0}),1.0]])]});}
            var Q27;
            {var subQ0=sQuery(id+"F5.wireOp",EDGE,"E11.8.0");var subQ1=makeQuery(id+"F3.boolean.opBoolean","COPY",EDGE,{"derivedFrom":makeQuery(id+"F3.opExtrude","CAP_EDGE",EDGE,{"disambiguationData":[OSD([sQuery(id+"F2.wireOp",EDGE,"E6")])],"isStart":true})});var subQ2=makeQuery(id+"F5.imprint","INTERSECT",VERTEX,{"disambiguationData":[OD(0.0)],"derivedFrom":[subQ1,subQ0]});Q27=makeQuery(id+"F5.imprint","IMPRINT",FACE,{"disambiguationData":[TD([[makeQuery(id+"F5.imprint","IMPRINT",EDGE,{"disambiguationData":[TD([[subQ2,-1.0]])],"derivedFrom":subQ0}),1.0]])]});}
            var Q28;
            {var subQ0=sQuery(id+"F5.wireOp",EDGE,"E11.30.0");var subQ1=makeQuery(id+"F3.boolean.opBoolean","COPY",EDGE,{"derivedFrom":makeQuery(id+"F3.opExtrude","CAP_EDGE",EDGE,{"disambiguationData":[OSD([sQuery(id+"F2.wireOp",EDGE,"E6")])],"isStart":true})});var subQ2=makeQuery(id+"F5.imprint","INTERSECT",VERTEX,{"disambiguationData":[OD(0.0)],"derivedFrom":[subQ1,subQ0]});Q28=makeQuery(id+"F5.imprint","IMPRINT",FACE,{"disambiguationData":[TD([[makeQuery(id+"F5.imprint","IMPRINT",EDGE,{"disambiguationData":[TD([[subQ2,1.0]])],"derivedFrom":subQ0}),1.0]])]});}
            var Q29;
            {var subQ0=sQuery(id+"F5.wireOp",EDGE,"E11.33.0");var subQ1=makeQuery(id+"F3.boolean.opBoolean","COPY",EDGE,{"derivedFrom":makeQuery(id+"F3.opExtrude","CAP_EDGE",EDGE,{"disambiguationData":[OSD([sQuery(id+"F2.wireOp",EDGE,"E6")])],"isStart":true})});var subQ2=makeQuery(id+"F5.imprint","INTERSECT",VERTEX,{"disambiguationData":[OD(0.0)],"derivedFrom":[subQ1,subQ0]});Q29=makeQuery(id+"F5.imprint","IMPRINT",FACE,{"disambiguationData":[TD([[makeQuery(id+"F5.imprint","IMPRINT",EDGE,{"disambiguationData":[TD([[subQ2,-1.0]])],"derivedFrom":subQ0}),1.0]])]});}
            var Q30;
            {var subQ0=sQuery(id+"F5.wireOp",EDGE,"E11.29.0");var subQ1=makeQuery(id+"F3.boolean.opBoolean","COPY",EDGE,{"derivedFrom":makeQuery(id+"F3.opExtrude","CAP_EDGE",EDGE,{"disambiguationData":[OSD([sQuery(id+"F2.wireOp",EDGE,"E6")])],"isStart":true})});var subQ2=makeQuery(id+"F5.imprint","INTERSECT",VERTEX,{"disambiguationData":[OD(0.0)],"derivedFrom":[subQ1,subQ0]});Q30=makeQuery(id+"F5.imprint","IMPRINT",FACE,{"disambiguationData":[TD([[makeQuery(id+"F5.imprint","IMPRINT",EDGE,{"disambiguationData":[TD([[subQ2,-1.0]])],"derivedFrom":subQ0}),1.0]])]});}
            var Q31;
            {var subQ0=sQuery(id+"F5.wireOp",EDGE,"E11.19.0");var subQ1=makeQuery(id+"F3.boolean.opBoolean","COPY",EDGE,{"derivedFrom":makeQuery(id+"F3.opExtrude","CAP_EDGE",EDGE,{"disambiguationData":[OSD([sQuery(id+"F2.wireOp",EDGE,"E6")])],"isStart":true})});var subQ2=makeQuery(id+"F5.imprint","INTERSECT",VERTEX,{"disambiguationData":[OD(0.0)],"derivedFrom":[subQ1,subQ0]});Q31=makeQuery(id+"F5.imprint","IMPRINT",FACE,{"disambiguationData":[TD([[makeQuery(id+"F5.imprint","IMPRINT",EDGE,{"disambiguationData":[TD([[subQ2,-1.0]])],"derivedFrom":subQ0}),1.0]])]});}
            var Q32;
            {var subQ0=sQuery(id+"F5.wireOp",EDGE,"E11.17.0");var subQ1=makeQuery(id+"F3.boolean.opBoolean","COPY",EDGE,{"derivedFrom":makeQuery(id+"F3.opExtrude","CAP_EDGE",EDGE,{"disambiguationData":[OSD([sQuery(id+"F2.wireOp",EDGE,"E6")])],"isStart":true})});var subQ2=makeQuery(id+"F5.imprint","INTERSECT",VERTEX,{"disambiguationData":[OD(0.0)],"derivedFrom":[subQ1,subQ0]});Q32=makeQuery(id+"F5.imprint","IMPRINT",FACE,{"disambiguationData":[TD([[makeQuery(id+"F5.imprint","IMPRINT",EDGE,{"disambiguationData":[TD([[subQ2,-1.0]])],"derivedFrom":subQ0}),1.0]])]});}
            var Q33;
            {var subQ0=sQuery(id+"F5.wireOp",EDGE,"E11.12.0");var subQ1=makeQuery(id+"F3.boolean.opBoolean","COPY",EDGE,{"derivedFrom":makeQuery(id+"F3.opExtrude","CAP_EDGE",EDGE,{"disambiguationData":[OSD([sQuery(id+"F2.wireOp",EDGE,"E6")])],"isStart":true})});var subQ2=makeQuery(id+"F5.imprint","INTERSECT",VERTEX,{"disambiguationData":[OD(0.0)],"derivedFrom":[subQ1,subQ0]});Q33=makeQuery(id+"F5.imprint","IMPRINT",FACE,{"disambiguationData":[TD([[makeQuery(id+"F5.imprint","IMPRINT",EDGE,{"disambiguationData":[TD([[subQ2,1.0]])],"derivedFrom":subQ0}),1.0]])]});}
            var Q34;
            {var subQ0=sQuery(id+"F5.wireOp",EDGE,"E11.28.0");var subQ1=makeQuery(id+"F3.boolean.opBoolean","COPY",EDGE,{"derivedFrom":makeQuery(id+"F3.opExtrude","CAP_EDGE",EDGE,{"disambiguationData":[OSD([sQuery(id+"F2.wireOp",EDGE,"E6")])],"isStart":true})});var subQ2=makeQuery(id+"F5.imprint","INTERSECT",VERTEX,{"disambiguationData":[OD(0.0)],"derivedFrom":[subQ1,subQ0]});Q34=makeQuery(id+"F5.imprint","IMPRINT",FACE,{"disambiguationData":[TD([[makeQuery(id+"F5.imprint","IMPRINT",EDGE,{"disambiguationData":[TD([[subQ2,1.0]])],"derivedFrom":subQ0}),1.0]])]});}
            var Q35;
            {var subQ0=sQuery(id+"F5.wireOp",EDGE,"E11.32.0");var subQ1=makeQuery(id+"F3.boolean.opBoolean","COPY",EDGE,{"derivedFrom":makeQuery(id+"F3.opExtrude","CAP_EDGE",EDGE,{"disambiguationData":[OSD([sQuery(id+"F2.wireOp",EDGE,"E6")])],"isStart":true})});var subQ2=makeQuery(id+"F5.imprint","INTERSECT",VERTEX,{"disambiguationData":[OD(0.0)],"derivedFrom":[subQ1,subQ0]});Q35=makeQuery(id+"F5.imprint","IMPRINT",FACE,{"disambiguationData":[TD([[makeQuery(id+"F5.imprint","IMPRINT",EDGE,{"disambiguationData":[TD([[subQ2,-1.0]])],"derivedFrom":subQ0}),1.0]])]});}
            var Q36;
            {var subQ0=sQuery(id+"F5.wireOp",EDGE,"E11.16.0");var subQ1=makeQuery(id+"F3.boolean.opBoolean","COPY",EDGE,{"derivedFrom":makeQuery(id+"F3.opExtrude","CAP_EDGE",EDGE,{"disambiguationData":[OSD([sQuery(id+"F2.wireOp",EDGE,"E6")])],"isStart":true})});var subQ2=makeQuery(id+"F5.imprint","INTERSECT",VERTEX,{"disambiguationData":[OD(0.0)],"derivedFrom":[subQ1,subQ0]});Q36=makeQuery(id+"F5.imprint","IMPRINT",FACE,{"disambiguationData":[TD([[makeQuery(id+"F5.imprint","IMPRINT",EDGE,{"disambiguationData":[TD([[subQ2,-1.0]])],"derivedFrom":subQ0}),1.0]])]});}
            var Q37;
            {var subQ0=sQuery(id+"F5.wireOp",EDGE,"E11.14.0");var subQ1=makeQuery(id+"F3.boolean.opBoolean","COPY",EDGE,{"derivedFrom":makeQuery(id+"F3.opExtrude","CAP_EDGE",EDGE,{"disambiguationData":[OSD([sQuery(id+"F2.wireOp",EDGE,"E6")])],"isStart":true})});var subQ2=makeQuery(id+"F5.imprint","INTERSECT",VERTEX,{"disambiguationData":[OD(0.0)],"derivedFrom":[subQ1,subQ0]});Q37=makeQuery(id+"F5.imprint","IMPRINT",FACE,{"disambiguationData":[TD([[makeQuery(id+"F5.imprint","IMPRINT",EDGE,{"disambiguationData":[TD([[subQ2,-1.0]])],"derivedFrom":subQ0}),1.0]])]});}
            var Q38;
            {var subQ0=sQuery(id+"F5.wireOp",EDGE,"E11.35.0");var subQ1=makeQuery(id+"F3.boolean.opBoolean","COPY",EDGE,{"derivedFrom":makeQuery(id+"F3.opExtrude","CAP_EDGE",EDGE,{"disambiguationData":[OSD([sQuery(id+"F2.wireOp",EDGE,"E6")])],"isStart":true})});var subQ2=makeQuery(id+"F5.imprint","INTERSECT",VERTEX,{"disambiguationData":[OD(0.0)],"derivedFrom":[subQ1,subQ0]});Q38=makeQuery(id+"F5.imprint","IMPRINT",FACE,{"disambiguationData":[TD([[makeQuery(id+"F5.imprint","IMPRINT",EDGE,{"disambiguationData":[TD([[subQ2,-1.0]])],"derivedFrom":subQ0}),1.0]])]});}
            var Q39;
            {var subQ0=sQuery(id+"F5.wireOp",EDGE,"E11.31.0");var subQ1=makeQuery(id+"F3.boolean.opBoolean","COPY",EDGE,{"derivedFrom":makeQuery(id+"F3.opExtrude","CAP_EDGE",EDGE,{"disambiguationData":[OSD([sQuery(id+"F2.wireOp",EDGE,"E6")])],"isStart":true})});var subQ2=makeQuery(id+"F5.imprint","INTERSECT",VERTEX,{"disambiguationData":[OD(0.0)],"derivedFrom":[subQ1,subQ0]});Q39=makeQuery(id+"F5.imprint","IMPRINT",FACE,{"disambiguationData":[TD([[makeQuery(id+"F5.imprint","IMPRINT",EDGE,{"disambiguationData":[TD([[subQ2,1.0]])],"derivedFrom":subQ0}),1.0]])]});}
            var Q40;
            {var subQ0=sQuery(id+"F5.wireOp",EDGE,"E11.25.0");var subQ1=makeQuery(id+"F3.boolean.opBoolean","COPY",EDGE,{"derivedFrom":makeQuery(id+"F3.opExtrude","CAP_EDGE",EDGE,{"disambiguationData":[OSD([sQuery(id+"F2.wireOp",EDGE,"E6")])],"isStart":true})});var subQ2=makeQuery(id+"F5.imprint","INTERSECT",VERTEX,{"disambiguationData":[OD(0.0)],"derivedFrom":[subQ1,subQ0]});Q40=makeQuery(id+"F5.imprint","IMPRINT",FACE,{"disambiguationData":[TD([[makeQuery(id+"F5.imprint","IMPRINT",EDGE,{"disambiguationData":[TD([[subQ2,1.0]])],"derivedFrom":subQ0}),1.0]])]});}
            var Q41;
            {var subQ0=sQuery(id+"F5.wireOp",EDGE,"E11.9.0");var subQ1=makeQuery(id+"F3.boolean.opBoolean","COPY",EDGE,{"derivedFrom":makeQuery(id+"F3.opExtrude","CAP_EDGE",EDGE,{"disambiguationData":[OSD([sQuery(id+"F2.wireOp",EDGE,"E6")])],"isStart":true})});var subQ2=makeQuery(id+"F5.imprint","INTERSECT",VERTEX,{"disambiguationData":[OD(0.0)],"derivedFrom":[subQ1,subQ0]});Q41=makeQuery(id+"F5.imprint","IMPRINT",FACE,{"disambiguationData":[TD([[makeQuery(id+"F5.imprint","IMPRINT",EDGE,{"disambiguationData":[TD([[subQ2,1.0]])],"derivedFrom":subQ0}),1.0]])]});}
            var Q42;
            {var subQ0=sQuery(id+"F5.wireOp",EDGE,"E11.20.0");var subQ1=makeQuery(id+"F3.boolean.opBoolean","COPY",EDGE,{"derivedFrom":makeQuery(id+"F3.opExtrude","CAP_EDGE",EDGE,{"disambiguationData":[OSD([sQuery(id+"F2.wireOp",EDGE,"E6")])],"isStart":true})});var subQ2=makeQuery(id+"F5.imprint","INTERSECT",VERTEX,{"disambiguationData":[OD(0.0)],"derivedFrom":[subQ1,subQ0]});Q42=makeQuery(id+"F5.imprint","IMPRINT",FACE,{"disambiguationData":[TD([[makeQuery(id+"F5.imprint","IMPRINT",EDGE,{"disambiguationData":[TD([[subQ2,-1.0]])],"derivedFrom":subQ0}),1.0]])]});}
            var Q43;
            {var subQ0=sQuery(id+"F5.wireOp",EDGE,"E11.32.0");var subQ1=makeQuery(id+"F3.boolean.opBoolean","COPY",EDGE,{"derivedFrom":makeQuery(id+"F3.opExtrude","CAP_EDGE",EDGE,{"disambiguationData":[OSD([sQuery(id+"F2.wireOp",EDGE,"E6")])],"isStart":true})});var subQ2=makeQuery(id+"F5.imprint","INTERSECT",VERTEX,{"disambiguationData":[OD(0.0)],"derivedFrom":[subQ1,subQ0]});Q43=makeQuery(id+"F5.imprint","IMPRINT",FACE,{"disambiguationData":[TD([[makeQuery(id+"F5.imprint","IMPRINT",EDGE,{"disambiguationData":[TD([[subQ2,1.0]])],"derivedFrom":subQ0}),1.0]])]});}
            var Q44;
            {var subQ0=sQuery(id+"F5.wireOp",EDGE,"E11.16.0");var subQ1=makeQuery(id+"F3.boolean.opBoolean","COPY",EDGE,{"derivedFrom":makeQuery(id+"F3.opExtrude","CAP_EDGE",EDGE,{"disambiguationData":[OSD([sQuery(id+"F2.wireOp",EDGE,"E6")])],"isStart":true})});var subQ2=makeQuery(id+"F5.imprint","INTERSECT",VERTEX,{"disambiguationData":[OD(0.0)],"derivedFrom":[subQ1,subQ0]});Q44=makeQuery(id+"F5.imprint","IMPRINT",FACE,{"disambiguationData":[TD([[makeQuery(id+"F5.imprint","IMPRINT",EDGE,{"disambiguationData":[TD([[subQ2,1.0]])],"derivedFrom":subQ0}),1.0]])]});}
            var Q45;
            {var subQ0=sQuery(id+"F5.wireOp",EDGE,"E11.21.0");var subQ1=makeQuery(id+"F3.boolean.opBoolean","COPY",EDGE,{"derivedFrom":makeQuery(id+"F3.opExtrude","CAP_EDGE",EDGE,{"disambiguationData":[OSD([sQuery(id+"F2.wireOp",EDGE,"E6")])],"isStart":true})});var subQ2=makeQuery(id+"F5.imprint","INTERSECT",VERTEX,{"disambiguationData":[OD(0.0)],"derivedFrom":[subQ1,subQ0]});Q45=makeQuery(id+"F5.imprint","IMPRINT",FACE,{"disambiguationData":[TD([[makeQuery(id+"F5.imprint","IMPRINT",EDGE,{"disambiguationData":[TD([[subQ2,-1.0]])],"derivedFrom":subQ0}),1.0]])]});}
            var Q46;
            {var subQ0=sQuery(id+"F5.wireOp",EDGE,"E11.33.0");var subQ1=makeQuery(id+"F3.boolean.opBoolean","COPY",EDGE,{"derivedFrom":makeQuery(id+"F3.opExtrude","CAP_EDGE",EDGE,{"disambiguationData":[OSD([sQuery(id+"F2.wireOp",EDGE,"E6")])],"isStart":true})});var subQ2=makeQuery(id+"F5.imprint","INTERSECT",VERTEX,{"disambiguationData":[OD(0.0)],"derivedFrom":[subQ1,subQ0]});Q46=makeQuery(id+"F5.imprint","IMPRINT",FACE,{"disambiguationData":[TD([[makeQuery(id+"F5.imprint","IMPRINT",EDGE,{"disambiguationData":[TD([[subQ2,1.0]])],"derivedFrom":subQ0}),1.0]])]});}
            var Q47;
            {var subQ0=sQuery(id+"F5.wireOp",EDGE,"E11.17.0");var subQ1=makeQuery(id+"F3.boolean.opBoolean","COPY",EDGE,{"derivedFrom":makeQuery(id+"F3.opExtrude","CAP_EDGE",EDGE,{"disambiguationData":[OSD([sQuery(id+"F2.wireOp",EDGE,"E6")])],"isStart":true})});var subQ2=makeQuery(id+"F5.imprint","INTERSECT",VERTEX,{"disambiguationData":[OD(0.0)],"derivedFrom":[subQ1,subQ0]});Q47=makeQuery(id+"F5.imprint","IMPRINT",FACE,{"disambiguationData":[TD([[makeQuery(id+"F5.imprint","IMPRINT",EDGE,{"disambiguationData":[TD([[subQ2,1.0]])],"derivedFrom":subQ0}),1.0]])]});}
            var Q48;
            {var subQ0=sQuery(id+"F5.wireOp",EDGE,"E11.22.0");var subQ1=makeQuery(id+"F3.boolean.opBoolean","COPY",EDGE,{"derivedFrom":makeQuery(id+"F3.opExtrude","CAP_EDGE",EDGE,{"disambiguationData":[OSD([sQuery(id+"F2.wireOp",EDGE,"E6")])],"isStart":true})});var subQ2=makeQuery(id+"F5.imprint","INTERSECT",VERTEX,{"disambiguationData":[OD(0.0)],"derivedFrom":[subQ1,subQ0]});Q48=makeQuery(id+"F5.imprint","IMPRINT",FACE,{"disambiguationData":[TD([[makeQuery(id+"F5.imprint","IMPRINT",EDGE,{"disambiguationData":[TD([[subQ2,-1.0]])],"derivedFrom":subQ0}),1.0]])]});}
            var Q49;
            {var subQ0=sQuery(id+"F5.wireOp",EDGE,"E11.34.0");var subQ1=makeQuery(id+"F3.boolean.opBoolean","COPY",EDGE,{"derivedFrom":makeQuery(id+"F3.opExtrude","CAP_EDGE",EDGE,{"disambiguationData":[OSD([sQuery(id+"F2.wireOp",EDGE,"E6")])],"isStart":true})});var subQ2=makeQuery(id+"F5.imprint","INTERSECT",VERTEX,{"disambiguationData":[OD(0.0)],"derivedFrom":[subQ1,subQ0]});Q49=makeQuery(id+"F5.imprint","IMPRINT",FACE,{"disambiguationData":[TD([[makeQuery(id+"F5.imprint","IMPRINT",EDGE,{"disambiguationData":[TD([[subQ2,1.0]])],"derivedFrom":subQ0}),1.0]])]});}
            var Q50;
            {var subQ0=sQuery(id+"F5.wireOp",EDGE,"E11.23.0");var subQ1=makeQuery(id+"F3.boolean.opBoolean","COPY",EDGE,{"derivedFrom":makeQuery(id+"F3.opExtrude","CAP_EDGE",EDGE,{"disambiguationData":[OSD([sQuery(id+"F2.wireOp",EDGE,"E6")])],"isStart":true})});var subQ2=makeQuery(id+"F5.imprint","INTERSECT",VERTEX,{"disambiguationData":[OD(0.0)],"derivedFrom":[subQ1,subQ0]});Q50=makeQuery(id+"F5.imprint","IMPRINT",FACE,{"disambiguationData":[TD([[makeQuery(id+"F5.imprint","IMPRINT",EDGE,{"disambiguationData":[TD([[subQ2,-1.0]])],"derivedFrom":subQ0}),1.0]])]});}
            var Q51;
            {var subQ0=sQuery(id+"F5.wireOp",EDGE,"E11.19.0");var subQ1=makeQuery(id+"F3.boolean.opBoolean","COPY",EDGE,{"derivedFrom":makeQuery(id+"F3.opExtrude","CAP_EDGE",EDGE,{"disambiguationData":[OSD([sQuery(id+"F2.wireOp",EDGE,"E6")])],"isStart":true})});var subQ2=makeQuery(id+"F5.imprint","INTERSECT",VERTEX,{"disambiguationData":[OD(0.0)],"derivedFrom":[subQ1,subQ0]});Q51=makeQuery(id+"F5.imprint","IMPRINT",FACE,{"disambiguationData":[TD([[makeQuery(id+"F5.imprint","IMPRINT",EDGE,{"disambiguationData":[TD([[subQ2,1.0]])],"derivedFrom":subQ0}),1.0]])]});}
            var Q52;
            {var subQ0=sQuery(id+"F5.wireOp",EDGE,"E11.26.0");var subQ1=makeQuery(id+"F3.boolean.opBoolean","COPY",EDGE,{"derivedFrom":makeQuery(id+"F3.opExtrude","CAP_EDGE",EDGE,{"disambiguationData":[OSD([sQuery(id+"F2.wireOp",EDGE,"E6")])],"isStart":true})});var subQ2=makeQuery(id+"F5.imprint","INTERSECT",VERTEX,{"disambiguationData":[OD(0.0)],"derivedFrom":[subQ1,subQ0]});Q52=makeQuery(id+"F5.imprint","IMPRINT",FACE,{"disambiguationData":[TD([[makeQuery(id+"F5.imprint","IMPRINT",EDGE,{"disambiguationData":[TD([[subQ2,1.0]])],"derivedFrom":subQ0}),1.0]])]});}
            var Q53;
            {var subQ0=sQuery(id+"F5.wireOp",EDGE,"E11.20.0");var subQ1=makeQuery(id+"F3.boolean.opBoolean","COPY",EDGE,{"derivedFrom":makeQuery(id+"F3.opExtrude","CAP_EDGE",EDGE,{"disambiguationData":[OSD([sQuery(id+"F2.wireOp",EDGE,"E6")])],"isStart":true})});var subQ2=makeQuery(id+"F5.imprint","INTERSECT",VERTEX,{"disambiguationData":[OD(0.0)],"derivedFrom":[subQ1,subQ0]});Q53=makeQuery(id+"F5.imprint","IMPRINT",FACE,{"disambiguationData":[TD([[makeQuery(id+"F5.imprint","IMPRINT",EDGE,{"disambiguationData":[TD([[subQ2,1.0]])],"derivedFrom":subQ0}),1.0]])]});}
            var Q54;
            {var subQ0=sQuery(id+"F5.wireOp",EDGE,"E11.25.0");var subQ1=makeQuery(id+"F3.boolean.opBoolean","COPY",EDGE,{"derivedFrom":makeQuery(id+"F3.opExtrude","CAP_EDGE",EDGE,{"disambiguationData":[OSD([sQuery(id+"F2.wireOp",EDGE,"E6")])],"isStart":true})});var subQ2=makeQuery(id+"F5.imprint","INTERSECT",VERTEX,{"disambiguationData":[OD(0.0)],"derivedFrom":[subQ1,subQ0]});Q54=makeQuery(id+"F5.imprint","IMPRINT",FACE,{"disambiguationData":[TD([[makeQuery(id+"F5.imprint","IMPRINT",EDGE,{"disambiguationData":[TD([[subQ2,-1.0]])],"derivedFrom":subQ0}),1.0]])]});}
            var Q55;
            {var subQ0=sQuery(id+"F5.wireOp",EDGE,"E11.26.0");var subQ1=makeQuery(id+"F3.boolean.opBoolean","COPY",EDGE,{"derivedFrom":makeQuery(id+"F3.opExtrude","CAP_EDGE",EDGE,{"disambiguationData":[OSD([sQuery(id+"F2.wireOp",EDGE,"E6")])],"isStart":true})});var subQ2=makeQuery(id+"F5.imprint","INTERSECT",VERTEX,{"disambiguationData":[OD(0.0)],"derivedFrom":[subQ1,subQ0]});Q55=makeQuery(id+"F5.imprint","IMPRINT",FACE,{"disambiguationData":[TD([[makeQuery(id+"F5.imprint","IMPRINT",EDGE,{"disambiguationData":[TD([[subQ2,-1.0]])],"derivedFrom":subQ0}),1.0]])]});}
            var Q56;
            {var subQ0=sQuery(id+"F5.wireOp",EDGE,"E11.11.0");var subQ1=makeQuery(id+"F3.boolean.opBoolean","COPY",EDGE,{"derivedFrom":makeQuery(id+"F3.opExtrude","CAP_EDGE",EDGE,{"disambiguationData":[OSD([sQuery(id+"F2.wireOp",EDGE,"E6")])],"isStart":true})});var subQ2=makeQuery(id+"F5.imprint","INTERSECT",VERTEX,{"disambiguationData":[OD(0.0)],"derivedFrom":[subQ1,subQ0]});Q56=makeQuery(id+"F5.imprint","IMPRINT",FACE,{"disambiguationData":[TD([[makeQuery(id+"F5.imprint","IMPRINT",EDGE,{"disambiguationData":[TD([[subQ2,1.0]])],"derivedFrom":subQ0}),1.0]])]});}
            var Q57;
            {var subQ0=sQuery(id+"F5.wireOp",EDGE,"E11.6.0");var subQ1=makeQuery(id+"F3.boolean.opBoolean","COPY",EDGE,{"derivedFrom":makeQuery(id+"F3.opExtrude","CAP_EDGE",EDGE,{"disambiguationData":[OSD([sQuery(id+"F2.wireOp",EDGE,"E6")])],"isStart":true})});var subQ2=makeQuery(id+"F5.imprint","INTERSECT",VERTEX,{"disambiguationData":[OD(0.0)],"derivedFrom":[subQ1,subQ0]});Q57=makeQuery(id+"F5.imprint","IMPRINT",FACE,{"disambiguationData":[TD([[makeQuery(id+"F5.imprint","IMPRINT",EDGE,{"disambiguationData":[TD([[subQ2,1.0]])],"derivedFrom":subQ0}),1.0]])]});}
            var Q58;
            {var subQ0=sQuery(id+"F5.wireOp",EDGE,"E11.27.0");var subQ1=makeQuery(id+"F3.boolean.opBoolean","COPY",EDGE,{"derivedFrom":makeQuery(id+"F3.opExtrude","CAP_EDGE",EDGE,{"disambiguationData":[OSD([sQuery(id+"F2.wireOp",EDGE,"E6")])],"isStart":true})});var subQ2=makeQuery(id+"F5.imprint","INTERSECT",VERTEX,{"disambiguationData":[OD(0.0)],"derivedFrom":[subQ1,subQ0]});Q58=makeQuery(id+"F5.imprint","IMPRINT",FACE,{"disambiguationData":[TD([[makeQuery(id+"F5.imprint","IMPRINT",EDGE,{"disambiguationData":[TD([[subQ2,-1.0]])],"derivedFrom":subQ0}),1.0]])]});}
            var Q59;
            {var subQ0=sQuery(id+"F5.wireOp",EDGE,"E11.23.0");var subQ1=makeQuery(id+"F3.boolean.opBoolean","COPY",EDGE,{"derivedFrom":makeQuery(id+"F3.opExtrude","CAP_EDGE",EDGE,{"disambiguationData":[OSD([sQuery(id+"F2.wireOp",EDGE,"E6")])],"isStart":true})});var subQ2=makeQuery(id+"F5.imprint","INTERSECT",VERTEX,{"disambiguationData":[OD(0.0)],"derivedFrom":[subQ1,subQ0]});Q59=makeQuery(id+"F5.imprint","IMPRINT",FACE,{"disambiguationData":[TD([[makeQuery(id+"F5.imprint","IMPRINT",EDGE,{"disambiguationData":[TD([[subQ2,1.0]])],"derivedFrom":subQ0}),1.0]])]});}
            var Q60;
            {var subQ0=sQuery(id+"F5.wireOp",EDGE,"E11.27.0");var subQ1=makeQuery(id+"F3.boolean.opBoolean","COPY",EDGE,{"derivedFrom":makeQuery(id+"F3.opExtrude","CAP_EDGE",EDGE,{"disambiguationData":[OSD([sQuery(id+"F2.wireOp",EDGE,"E6")])],"isStart":true})});var subQ2=makeQuery(id+"F5.imprint","INTERSECT",VERTEX,{"disambiguationData":[OD(0.0)],"derivedFrom":[subQ1,subQ0]});Q60=makeQuery(id+"F5.imprint","IMPRINT",FACE,{"disambiguationData":[TD([[makeQuery(id+"F5.imprint","IMPRINT",EDGE,{"disambiguationData":[TD([[subQ2,1.0]])],"derivedFrom":subQ0}),1.0]])]});}
            var Q61;
            {var subQ0=sQuery(id+"F5.wireOp",EDGE,"E11.7.0");var subQ1=makeQuery(id+"F3.boolean.opBoolean","COPY",EDGE,{"derivedFrom":makeQuery(id+"F3.opExtrude","CAP_EDGE",EDGE,{"disambiguationData":[OSD([sQuery(id+"F2.wireOp",EDGE,"E6")])],"isStart":true})});var subQ2=makeQuery(id+"F5.imprint","INTERSECT",VERTEX,{"disambiguationData":[OD(0.0)],"derivedFrom":[subQ1,subQ0]});Q61=makeQuery(id+"F5.imprint","IMPRINT",FACE,{"disambiguationData":[TD([[makeQuery(id+"F5.imprint","IMPRINT",EDGE,{"disambiguationData":[TD([[subQ2,1.0]])],"derivedFrom":subQ0}),1.0]])]});}
            var Q62;
            {var subQ0=sQuery(id+"F5.wireOp",EDGE,"E11.28.0");var subQ1=makeQuery(id+"F3.boolean.opBoolean","COPY",EDGE,{"derivedFrom":makeQuery(id+"F3.opExtrude","CAP_EDGE",EDGE,{"disambiguationData":[OSD([sQuery(id+"F2.wireOp",EDGE,"E6")])],"isStart":true})});var subQ2=makeQuery(id+"F5.imprint","INTERSECT",VERTEX,{"disambiguationData":[OD(0.0)],"derivedFrom":[subQ1,subQ0]});Q62=makeQuery(id+"F5.imprint","IMPRINT",FACE,{"disambiguationData":[TD([[makeQuery(id+"F5.imprint","IMPRINT",EDGE,{"disambiguationData":[TD([[subQ2,-1.0]])],"derivedFrom":subQ0}),1.0]])]});}
            var Q63;
            {var subQ0=sQuery(id+"F5.wireOp",EDGE,"E11.24.0");var subQ1=makeQuery(id+"F3.boolean.opBoolean","COPY",EDGE,{"derivedFrom":makeQuery(id+"F3.opExtrude","CAP_EDGE",EDGE,{"disambiguationData":[OSD([sQuery(id+"F2.wireOp",EDGE,"E6")])],"isStart":true})});var subQ2=makeQuery(id+"F5.imprint","INTERSECT",VERTEX,{"disambiguationData":[OD(0.0)],"derivedFrom":[subQ1,subQ0]});Q63=makeQuery(id+"F5.imprint","IMPRINT",FACE,{"disambiguationData":[TD([[makeQuery(id+"F5.imprint","IMPRINT",EDGE,{"disambiguationData":[TD([[subQ2,1.0]])],"derivedFrom":subQ0}),1.0]])]});}
            var Q64;
            {var subQ0=sQuery(id+"F5.wireOp",EDGE,"E11.8.0");var subQ1=makeQuery(id+"F3.boolean.opBoolean","COPY",EDGE,{"derivedFrom":makeQuery(id+"F3.opExtrude","CAP_EDGE",EDGE,{"disambiguationData":[OSD([sQuery(id+"F2.wireOp",EDGE,"E6")])],"isStart":true})});var subQ2=makeQuery(id+"F5.imprint","INTERSECT",VERTEX,{"disambiguationData":[OD(0.0)],"derivedFrom":[subQ1,subQ0]});Q64=makeQuery(id+"F5.imprint","IMPRINT",FACE,{"disambiguationData":[TD([[makeQuery(id+"F5.imprint","IMPRINT",EDGE,{"disambiguationData":[TD([[subQ2,1.0]])],"derivedFrom":subQ0}),1.0]])]});}
            var Q65;
            {var subQ0=sQuery(id+"F5.wireOp",EDGE,"E11.31.0");var subQ1=makeQuery(id+"F3.boolean.opBoolean","COPY",EDGE,{"derivedFrom":makeQuery(id+"F3.opExtrude","CAP_EDGE",EDGE,{"disambiguationData":[OSD([sQuery(id+"F2.wireOp",EDGE,"E6")])],"isStart":true})});var subQ2=makeQuery(id+"F5.imprint","INTERSECT",VERTEX,{"disambiguationData":[OD(0.0)],"derivedFrom":[subQ1,subQ0]});Q65=makeQuery(id+"F5.imprint","IMPRINT",FACE,{"disambiguationData":[TD([[makeQuery(id+"F5.imprint","IMPRINT",EDGE,{"disambiguationData":[TD([[subQ2,-1.0]])],"derivedFrom":subQ0}),1.0]])]});}
            var Q66;
            {var subQ0=sQuery(id+"F5.wireOp",EDGE,"E11.15.0");var subQ1=makeQuery(id+"F3.boolean.opBoolean","COPY",EDGE,{"derivedFrom":makeQuery(id+"F3.opExtrude","CAP_EDGE",EDGE,{"disambiguationData":[OSD([sQuery(id+"F2.wireOp",EDGE,"E6")])],"isStart":true})});var subQ2=makeQuery(id+"F5.imprint","INTERSECT",VERTEX,{"disambiguationData":[OD(0.0)],"derivedFrom":[subQ1,subQ0]});Q66=makeQuery(id+"F5.imprint","IMPRINT",FACE,{"disambiguationData":[TD([[makeQuery(id+"F5.imprint","IMPRINT",EDGE,{"disambiguationData":[TD([[subQ2,-1.0]])],"derivedFrom":subQ0}),1.0]])]});}
            var Q67;
            {var subQ0=sQuery(id+"F5.wireOp",EDGE,"E11.10.0");var subQ1=makeQuery(id+"F3.boolean.opBoolean","COPY",EDGE,{"derivedFrom":makeQuery(id+"F3.opExtrude","CAP_EDGE",EDGE,{"disambiguationData":[OSD([sQuery(id+"F2.wireOp",EDGE,"E6")])],"isStart":true})});var subQ2=makeQuery(id+"F5.imprint","INTERSECT",VERTEX,{"disambiguationData":[OD(0.0)],"derivedFrom":[subQ1,subQ0]});Q67=makeQuery(id+"F5.imprint","IMPRINT",FACE,{"disambiguationData":[TD([[makeQuery(id+"F5.imprint","IMPRINT",EDGE,{"disambiguationData":[TD([[subQ2,-1.0]])],"derivedFrom":subQ0}),1.0]])]});}
            var Q68;
            {var subQ0=sQuery(id+"F5.wireOp",EDGE,"E11.10.0");var subQ1=makeQuery(id+"F3.boolean.opBoolean","COPY",EDGE,{"derivedFrom":makeQuery(id+"F3.opExtrude","CAP_EDGE",EDGE,{"disambiguationData":[OSD([sQuery(id+"F2.wireOp",EDGE,"E6")])],"isStart":true})});var subQ2=makeQuery(id+"F5.imprint","INTERSECT",VERTEX,{"disambiguationData":[OD(0.0)],"derivedFrom":[subQ1,subQ0]});Q68=makeQuery(id+"F5.imprint","IMPRINT",FACE,{"disambiguationData":[TD([[makeQuery(id+"F5.imprint","IMPRINT",EDGE,{"disambiguationData":[TD([[subQ2,1.0]])],"derivedFrom":subQ0}),1.0]])]});}
            var Q69;
            {var subQ0=sQuery(id+"F5.wireOp",EDGE,"E11.5.0");var subQ1=makeQuery(id+"F3.boolean.opBoolean","COPY",EDGE,{"derivedFrom":makeQuery(id+"F3.opExtrude","CAP_EDGE",EDGE,{"disambiguationData":[OSD([sQuery(id+"F2.wireOp",EDGE,"E6")])],"isStart":true})});var subQ2=makeQuery(id+"F5.imprint","INTERSECT",VERTEX,{"disambiguationData":[OD(0.0)],"derivedFrom":[subQ1,subQ0]});Q69=makeQuery(id+"F5.imprint","IMPRINT",FACE,{"disambiguationData":[TD([[makeQuery(id+"F5.imprint","IMPRINT",EDGE,{"disambiguationData":[TD([[subQ2,-1.0]])],"derivedFrom":subQ0}),1.0]])]});}
            var Q70;
            {var subQ0=sQuery(id+"F5.wireOp",EDGE,"E11.4.0");var subQ1=makeQuery(id+"F3.boolean.opBoolean","COPY",EDGE,{"derivedFrom":makeQuery(id+"F3.opExtrude","CAP_EDGE",EDGE,{"disambiguationData":[OSD([sQuery(id+"F2.wireOp",EDGE,"E6")])],"isStart":true})});var subQ2=makeQuery(id+"F5.imprint","INTERSECT",VERTEX,{"disambiguationData":[OD(0.0)],"derivedFrom":[subQ1,subQ0]});Q70=makeQuery(id+"F5.imprint","IMPRINT",FACE,{"disambiguationData":[TD([[makeQuery(id+"F5.imprint","IMPRINT",EDGE,{"disambiguationData":[TD([[subQ2,1.0]])],"derivedFrom":subQ0}),1.0]])]});}
            var Q71;
            {var subQ0=sQuery(id+"F5.wireOp",EDGE,"E11.5.0");var subQ1=makeQuery(id+"F3.boolean.opBoolean","COPY",EDGE,{"derivedFrom":makeQuery(id+"F3.opExtrude","CAP_EDGE",EDGE,{"disambiguationData":[OSD([sQuery(id+"F2.wireOp",EDGE,"E6")])],"isStart":true})});var subQ2=makeQuery(id+"F5.imprint","INTERSECT",VERTEX,{"disambiguationData":[OD(0.0)],"derivedFrom":[subQ1,subQ0]});Q71=makeQuery(id+"F5.imprint","IMPRINT",FACE,{"disambiguationData":[TD([[makeQuery(id+"F5.imprint","IMPRINT",EDGE,{"disambiguationData":[TD([[subQ2,1.0]])],"derivedFrom":subQ0}),1.0]])]});}
            var Q72;
            {var subQ0=sQuery(id+"F5.wireOp",EDGE,"E12.1.61.0");var subQ1=makeQuery(id+"F3.boolean.opBoolean","COPY",EDGE,{"derivedFrom":makeQuery(id+"F3.opExtrude","CAP_EDGE",EDGE,{"disambiguationData":[OSD([sQuery(id+"F2.wireOp",EDGE,"E6")])],"isStart":true})});var subQ2=makeQuery(id+"F5.imprint","INTERSECT",VERTEX,{"disambiguationData":[OD(0.0)],"derivedFrom":[subQ1,subQ0]});Q72=makeQuery(id+"F5.imprint","IMPRINT",FACE,{"disambiguationData":[TD([[makeQuery(id+"F5.imprint","IMPRINT",EDGE,{"disambiguationData":[TD([[subQ2,-1.0]])],"derivedFrom":subQ0}),1.0]])]});}
            var Q73;
            {var subQ0=sQuery(id+"F5.wireOp",EDGE,"E12.1.60.0");var subQ1=makeQuery(id+"F3.boolean.opBoolean","COPY",EDGE,{"derivedFrom":makeQuery(id+"F3.opExtrude","CAP_EDGE",EDGE,{"disambiguationData":[OSD([sQuery(id+"F2.wireOp",EDGE,"E6")])],"isStart":true})});var subQ2=makeQuery(id+"F5.imprint","INTERSECT",VERTEX,{"disambiguationData":[OD(0.0)],"derivedFrom":[subQ1,subQ0]});Q73=makeQuery(id+"F5.imprint","IMPRINT",FACE,{"disambiguationData":[TD([[makeQuery(id+"F5.imprint","IMPRINT",EDGE,{"disambiguationData":[TD([[subQ2,-1.0]])],"derivedFrom":subQ0}),1.0]])]});}
            var Q74;
            {var subQ0=sQuery(id+"F5.wireOp",EDGE,"E12.1.59.0");var subQ1=makeQuery(id+"F3.boolean.opBoolean","COPY",EDGE,{"derivedFrom":makeQuery(id+"F3.opExtrude","CAP_EDGE",EDGE,{"disambiguationData":[OSD([sQuery(id+"F2.wireOp",EDGE,"E6")])],"isStart":true})});var subQ2=makeQuery(id+"F5.imprint","INTERSECT",VERTEX,{"disambiguationData":[OD(0.0)],"derivedFrom":[subQ1,subQ0]});Q74=makeQuery(id+"F5.imprint","IMPRINT",FACE,{"disambiguationData":[TD([[makeQuery(id+"F5.imprint","IMPRINT",EDGE,{"disambiguationData":[TD([[subQ2,-1.0]])],"derivedFrom":subQ0}),1.0]])]});}
            var Q75;
            {var subQ0=sQuery(id+"F5.wireOp",EDGE,"E11.45.0");var subQ1=makeQuery(id+"F3.boolean.opBoolean","COPY",EDGE,{"derivedFrom":makeQuery(id+"F3.opExtrude","CAP_EDGE",EDGE,{"disambiguationData":[OSD([sQuery(id+"F2.wireOp",EDGE,"E6")])],"isStart":true})});var subQ2=makeQuery(id+"F5.imprint","INTERSECT",VERTEX,{"disambiguationData":[OD(0.0)],"derivedFrom":[subQ1,subQ0]});Q75=makeQuery(id+"F5.imprint","IMPRINT",FACE,{"disambiguationData":[TD([[makeQuery(id+"F5.imprint","IMPRINT",EDGE,{"disambiguationData":[TD([[subQ2,1.0]])],"derivedFrom":subQ0}),1.0]])]});}
            var Q76;
            {var subQ0=sQuery(id+"F5.wireOp",EDGE,"E11.46.0");var subQ1=makeQuery(id+"F3.boolean.opBoolean","COPY",EDGE,{"derivedFrom":makeQuery(id+"F3.opExtrude","CAP_EDGE",EDGE,{"disambiguationData":[OSD([sQuery(id+"F2.wireOp",EDGE,"E6")])],"isStart":true})});var subQ2=makeQuery(id+"F5.imprint","INTERSECT",VERTEX,{"disambiguationData":[OD(0.0)],"derivedFrom":[subQ1,subQ0]});Q76=makeQuery(id+"F5.imprint","IMPRINT",FACE,{"disambiguationData":[TD([[makeQuery(id+"F5.imprint","IMPRINT",EDGE,{"disambiguationData":[TD([[subQ2,-1.0]])],"derivedFrom":subQ0}),1.0]])]});}
            var Q77;
            {var subQ0=sQuery(id+"F5.wireOp",EDGE,"E12.1.50.0");var subQ1=makeQuery(id+"F3.boolean.opBoolean","COPY",EDGE,{"derivedFrom":makeQuery(id+"F3.opExtrude","CAP_EDGE",EDGE,{"disambiguationData":[OSD([sQuery(id+"F2.wireOp",EDGE,"E6")])],"isStart":true})});var subQ2=makeQuery(id+"F5.imprint","INTERSECT",VERTEX,{"disambiguationData":[OD(0.0)],"derivedFrom":[subQ1,subQ0]});Q77=makeQuery(id+"F5.imprint","IMPRINT",FACE,{"disambiguationData":[TD([[makeQuery(id+"F5.imprint","IMPRINT",EDGE,{"disambiguationData":[TD([[subQ2,-1.0]])],"derivedFrom":subQ0}),1.0]])]});}
            var Q78;
            {var subQ0=sQuery(id+"F5.wireOp",EDGE,"E11.45.0");var subQ1=makeQuery(id+"F3.boolean.opBoolean","COPY",EDGE,{"derivedFrom":makeQuery(id+"F3.opExtrude","CAP_EDGE",EDGE,{"disambiguationData":[OSD([sQuery(id+"F2.wireOp",EDGE,"E6")])],"isStart":true})});var subQ2=makeQuery(id+"F5.imprint","INTERSECT",VERTEX,{"disambiguationData":[OD(0.0)],"derivedFrom":[subQ1,subQ0]});Q78=makeQuery(id+"F5.imprint","IMPRINT",FACE,{"disambiguationData":[TD([[makeQuery(id+"F5.imprint","IMPRINT",EDGE,{"disambiguationData":[TD([[subQ2,-1.0]])],"derivedFrom":subQ0}),1.0]])]});}
            var Q79;
            {var subQ0=sQuery(id+"F5.wireOp",EDGE,"E11.49.0");var subQ1=makeQuery(id+"F3.boolean.opBoolean","COPY",EDGE,{"derivedFrom":makeQuery(id+"F3.opExtrude","CAP_EDGE",EDGE,{"disambiguationData":[OSD([sQuery(id+"F2.wireOp",EDGE,"E6")])],"isStart":true})});var subQ2=makeQuery(id+"F5.imprint","INTERSECT",VERTEX,{"disambiguationData":[OD(0.0)],"derivedFrom":[subQ1,subQ0]});Q79=makeQuery(id+"F5.imprint","IMPRINT",FACE,{"disambiguationData":[TD([[makeQuery(id+"F5.imprint","IMPRINT",EDGE,{"disambiguationData":[TD([[subQ2,-1.0]])],"derivedFrom":subQ0}),1.0]])]});}
            var Q80;
            {var subQ0=sQuery(id+"F5.wireOp",EDGE,"E11.44.0");var subQ1=makeQuery(id+"F3.boolean.opBoolean","COPY",EDGE,{"derivedFrom":makeQuery(id+"F3.opExtrude","CAP_EDGE",EDGE,{"disambiguationData":[OSD([sQuery(id+"F2.wireOp",EDGE,"E6")])],"isStart":true})});var subQ2=makeQuery(id+"F5.imprint","INTERSECT",VERTEX,{"disambiguationData":[OD(0.0)],"derivedFrom":[subQ1,subQ0]});Q80=makeQuery(id+"F5.imprint","IMPRINT",FACE,{"disambiguationData":[TD([[makeQuery(id+"F5.imprint","IMPRINT",EDGE,{"disambiguationData":[TD([[subQ2,1.0]])],"derivedFrom":subQ0}),1.0]])]});}
            var Q81;
            {var subQ0=sQuery(id+"F5.wireOp",EDGE,"E11.48.0");var subQ1=makeQuery(id+"F3.boolean.opBoolean","COPY",EDGE,{"derivedFrom":makeQuery(id+"F3.opExtrude","CAP_EDGE",EDGE,{"disambiguationData":[OSD([sQuery(id+"F2.wireOp",EDGE,"E6")])],"isStart":true})});var subQ2=makeQuery(id+"F5.imprint","INTERSECT",VERTEX,{"disambiguationData":[OD(0.0)],"derivedFrom":[subQ1,subQ0]});Q81=makeQuery(id+"F5.imprint","IMPRINT",FACE,{"disambiguationData":[TD([[makeQuery(id+"F5.imprint","IMPRINT",EDGE,{"disambiguationData":[TD([[subQ2,-1.0]])],"derivedFrom":subQ0}),1.0]])]});}
            var Q82;
            {var subQ0=sQuery(id+"F5.wireOp",EDGE,"E12.1.51.0");var subQ1=makeQuery(id+"F3.boolean.opBoolean","COPY",EDGE,{"derivedFrom":makeQuery(id+"F3.opExtrude","CAP_EDGE",EDGE,{"disambiguationData":[OSD([sQuery(id+"F2.wireOp",EDGE,"E6")])],"isStart":true})});var subQ2=makeQuery(id+"F5.imprint","INTERSECT",VERTEX,{"disambiguationData":[OD(0.0)],"derivedFrom":[subQ1,subQ0]});Q82=makeQuery(id+"F5.imprint","IMPRINT",FACE,{"disambiguationData":[TD([[makeQuery(id+"F5.imprint","IMPRINT",EDGE,{"disambiguationData":[TD([[subQ2,-1.0]])],"derivedFrom":subQ0}),1.0]])]});}
            var Q83;
            {var subQ0=sQuery(id+"F5.wireOp",EDGE,"E11.47.0");var subQ1=makeQuery(id+"F3.boolean.opBoolean","COPY",EDGE,{"derivedFrom":makeQuery(id+"F3.opExtrude","CAP_EDGE",EDGE,{"disambiguationData":[OSD([sQuery(id+"F2.wireOp",EDGE,"E6")])],"isStart":true})});var subQ2=makeQuery(id+"F5.imprint","INTERSECT",VERTEX,{"disambiguationData":[OD(0.0)],"derivedFrom":[subQ1,subQ0]});Q83=makeQuery(id+"F5.imprint","IMPRINT",FACE,{"disambiguationData":[TD([[makeQuery(id+"F5.imprint","IMPRINT",EDGE,{"disambiguationData":[TD([[subQ2,1.0]])],"derivedFrom":subQ0}),1.0]])]});}
            var Q84;
            {var subQ0=sQuery(id+"F5.wireOp",EDGE,"E11.41.0");var subQ1=makeQuery(id+"F3.boolean.opBoolean","COPY",EDGE,{"derivedFrom":makeQuery(id+"F3.opExtrude","CAP_EDGE",EDGE,{"disambiguationData":[OSD([sQuery(id+"F2.wireOp",EDGE,"E6")])],"isStart":true})});var subQ2=makeQuery(id+"F5.imprint","INTERSECT",VERTEX,{"disambiguationData":[OD(0.0)],"derivedFrom":[subQ1,subQ0]});Q84=makeQuery(id+"F5.imprint","IMPRINT",FACE,{"disambiguationData":[TD([[makeQuery(id+"F5.imprint","IMPRINT",EDGE,{"disambiguationData":[TD([[subQ2,1.0]])],"derivedFrom":subQ0}),1.0]])]});}
            var Q85;
            {var subQ0=sQuery(id+"F5.wireOp",EDGE,"E11.36.0");var subQ1=makeQuery(id+"F3.boolean.opBoolean","COPY",EDGE,{"derivedFrom":makeQuery(id+"F3.opExtrude","CAP_EDGE",EDGE,{"disambiguationData":[OSD([sQuery(id+"F2.wireOp",EDGE,"E6")])],"isStart":true})});var subQ2=makeQuery(id+"F5.imprint","INTERSECT",VERTEX,{"disambiguationData":[OD(0.0)],"derivedFrom":[subQ1,subQ0]});Q85=makeQuery(id+"F5.imprint","IMPRINT",FACE,{"disambiguationData":[TD([[makeQuery(id+"F5.imprint","IMPRINT",EDGE,{"disambiguationData":[TD([[subQ2,-1.0]])],"derivedFrom":subQ0}),1.0]])]});}
            var Q86;
            {var subQ0=sQuery(id+"F5.wireOp",EDGE,"E11.48.0");var subQ1=makeQuery(id+"F3.boolean.opBoolean","COPY",EDGE,{"derivedFrom":makeQuery(id+"F3.opExtrude","CAP_EDGE",EDGE,{"disambiguationData":[OSD([sQuery(id+"F2.wireOp",EDGE,"E6")])],"isStart":true})});var subQ2=makeQuery(id+"F5.imprint","INTERSECT",VERTEX,{"disambiguationData":[OD(0.0)],"derivedFrom":[subQ1,subQ0]});Q86=makeQuery(id+"F5.imprint","IMPRINT",FACE,{"disambiguationData":[TD([[makeQuery(id+"F5.imprint","IMPRINT",EDGE,{"disambiguationData":[TD([[subQ2,1.0]])],"derivedFrom":subQ0}),1.0]])]});}
            var Q87;
            {var subQ0=sQuery(id+"F5.wireOp",EDGE,"E11.37.0");var subQ1=makeQuery(id+"F3.boolean.opBoolean","COPY",EDGE,{"derivedFrom":makeQuery(id+"F3.opExtrude","CAP_EDGE",EDGE,{"disambiguationData":[OSD([sQuery(id+"F2.wireOp",EDGE,"E6")])],"isStart":true})});var subQ2=makeQuery(id+"F5.imprint","INTERSECT",VERTEX,{"disambiguationData":[OD(0.0)],"derivedFrom":[subQ1,subQ0]});Q87=makeQuery(id+"F5.imprint","IMPRINT",FACE,{"disambiguationData":[TD([[makeQuery(id+"F5.imprint","IMPRINT",EDGE,{"disambiguationData":[TD([[subQ2,-1.0]])],"derivedFrom":subQ0}),1.0]])]});}
            var Q88;
            {var subQ0=sQuery(id+"F5.wireOp",EDGE,"E11.38.0");var subQ1=makeQuery(id+"F3.boolean.opBoolean","COPY",EDGE,{"derivedFrom":makeQuery(id+"F3.opExtrude","CAP_EDGE",EDGE,{"disambiguationData":[OSD([sQuery(id+"F2.wireOp",EDGE,"E6")])],"isStart":true})});var subQ2=makeQuery(id+"F5.imprint","INTERSECT",VERTEX,{"disambiguationData":[OD(0.0)],"derivedFrom":[subQ1,subQ0]});Q88=makeQuery(id+"F5.imprint","IMPRINT",FACE,{"disambiguationData":[TD([[makeQuery(id+"F5.imprint","IMPRINT",EDGE,{"disambiguationData":[TD([[subQ2,-1.0]])],"derivedFrom":subQ0}),1.0]])]});}
            var Q89;
            {var subQ0=sQuery(id+"F5.wireOp",EDGE,"E12.1.50.0");var subQ1=makeQuery(id+"F3.boolean.opBoolean","COPY",EDGE,{"derivedFrom":makeQuery(id+"F3.opExtrude","CAP_EDGE",EDGE,{"disambiguationData":[OSD([sQuery(id+"F2.wireOp",EDGE,"E6")])],"isStart":true})});var subQ2=makeQuery(id+"F5.imprint","INTERSECT",VERTEX,{"disambiguationData":[OD(0.0)],"derivedFrom":[subQ1,subQ0]});Q89=makeQuery(id+"F5.imprint","IMPRINT",FACE,{"disambiguationData":[TD([[makeQuery(id+"F5.imprint","IMPRINT",EDGE,{"disambiguationData":[TD([[subQ2,1.0]])],"derivedFrom":subQ0}),1.0]])]});}
            var Q90;
            {var subQ0=sQuery(id+"F5.wireOp",EDGE,"E12.1.55.0");var subQ1=makeQuery(id+"F3.boolean.opBoolean","COPY",EDGE,{"derivedFrom":makeQuery(id+"F3.opExtrude","CAP_EDGE",EDGE,{"disambiguationData":[OSD([sQuery(id+"F2.wireOp",EDGE,"E6")])],"isStart":true})});var subQ2=makeQuery(id+"F5.imprint","INTERSECT",VERTEX,{"disambiguationData":[OD(0.0)],"derivedFrom":[subQ1,subQ0]});Q90=makeQuery(id+"F5.imprint","IMPRINT",FACE,{"disambiguationData":[TD([[makeQuery(id+"F5.imprint","IMPRINT",EDGE,{"disambiguationData":[TD([[subQ2,-1.0]])],"derivedFrom":subQ0}),1.0]])]});}
            var Q91;
            {var subQ0=sQuery(id+"F5.wireOp",EDGE,"E11.39.0");var subQ1=makeQuery(id+"F3.boolean.opBoolean","COPY",EDGE,{"derivedFrom":makeQuery(id+"F3.opExtrude","CAP_EDGE",EDGE,{"disambiguationData":[OSD([sQuery(id+"F2.wireOp",EDGE,"E6")])],"isStart":true})});var subQ2=makeQuery(id+"F5.imprint","INTERSECT",VERTEX,{"disambiguationData":[OD(0.0)],"derivedFrom":[subQ1,subQ0]});Q91=makeQuery(id+"F5.imprint","IMPRINT",FACE,{"disambiguationData":[TD([[makeQuery(id+"F5.imprint","IMPRINT",EDGE,{"disambiguationData":[TD([[subQ2,-1.0]])],"derivedFrom":subQ0}),1.0]])]});}
            var Q92;
            {var subQ0=sQuery(id+"F5.wireOp",EDGE,"E12.1.51.0");var subQ1=makeQuery(id+"F3.boolean.opBoolean","COPY",EDGE,{"derivedFrom":makeQuery(id+"F3.opExtrude","CAP_EDGE",EDGE,{"disambiguationData":[OSD([sQuery(id+"F2.wireOp",EDGE,"E6")])],"isStart":true})});var subQ2=makeQuery(id+"F5.imprint","INTERSECT",VERTEX,{"disambiguationData":[OD(0.0)],"derivedFrom":[subQ1,subQ0]});Q92=makeQuery(id+"F5.imprint","IMPRINT",FACE,{"disambiguationData":[TD([[makeQuery(id+"F5.imprint","IMPRINT",EDGE,{"disambiguationData":[TD([[subQ2,1.0]])],"derivedFrom":subQ0}),1.0]])]});}
            var Q93;
            {var subQ0=sQuery(id+"F5.wireOp",EDGE,"E11.36.0");var subQ1=makeQuery(id+"F3.boolean.opBoolean","COPY",EDGE,{"derivedFrom":makeQuery(id+"F3.opExtrude","CAP_EDGE",EDGE,{"disambiguationData":[OSD([sQuery(id+"F2.wireOp",EDGE,"E6")])],"isStart":true})});var subQ2=makeQuery(id+"F5.imprint","INTERSECT",VERTEX,{"disambiguationData":[OD(0.0)],"derivedFrom":[subQ1,subQ0]});Q93=makeQuery(id+"F5.imprint","IMPRINT",FACE,{"disambiguationData":[TD([[makeQuery(id+"F5.imprint","IMPRINT",EDGE,{"disambiguationData":[TD([[subQ2,1.0]])],"derivedFrom":subQ0}),1.0]])]});}
            var Q94;
            {var subQ0=sQuery(id+"F5.wireOp",EDGE,"E12.1.56.0");var subQ1=makeQuery(id+"F3.boolean.opBoolean","COPY",EDGE,{"derivedFrom":makeQuery(id+"F3.opExtrude","CAP_EDGE",EDGE,{"disambiguationData":[OSD([sQuery(id+"F2.wireOp",EDGE,"E6")])],"isStart":true})});var subQ2=makeQuery(id+"F5.imprint","INTERSECT",VERTEX,{"disambiguationData":[OD(0.0)],"derivedFrom":[subQ1,subQ0]});Q94=makeQuery(id+"F5.imprint","IMPRINT",FACE,{"disambiguationData":[TD([[makeQuery(id+"F5.imprint","IMPRINT",EDGE,{"disambiguationData":[TD([[subQ2,-1.0]])],"derivedFrom":subQ0}),1.0]])]});}
            var Q95;
            {var subQ0=sQuery(id+"F5.wireOp",EDGE,"E11.40.0");var subQ1=makeQuery(id+"F3.boolean.opBoolean","COPY",EDGE,{"derivedFrom":makeQuery(id+"F3.opExtrude","CAP_EDGE",EDGE,{"disambiguationData":[OSD([sQuery(id+"F2.wireOp",EDGE,"E6")])],"isStart":true})});var subQ2=makeQuery(id+"F5.imprint","INTERSECT",VERTEX,{"disambiguationData":[OD(0.0)],"derivedFrom":[subQ1,subQ0]});Q95=makeQuery(id+"F5.imprint","IMPRINT",FACE,{"disambiguationData":[TD([[makeQuery(id+"F5.imprint","IMPRINT",EDGE,{"disambiguationData":[TD([[subQ2,-1.0]])],"derivedFrom":subQ0}),1.0]])]});}
            var Q96;
            {var subQ0=sQuery(id+"F5.wireOp",EDGE,"E11.37.0");var subQ1=makeQuery(id+"F3.boolean.opBoolean","COPY",EDGE,{"derivedFrom":makeQuery(id+"F3.opExtrude","CAP_EDGE",EDGE,{"disambiguationData":[OSD([sQuery(id+"F2.wireOp",EDGE,"E6")])],"isStart":true})});var subQ2=makeQuery(id+"F5.imprint","INTERSECT",VERTEX,{"disambiguationData":[OD(0.0)],"derivedFrom":[subQ1,subQ0]});Q96=makeQuery(id+"F5.imprint","IMPRINT",FACE,{"disambiguationData":[TD([[makeQuery(id+"F5.imprint","IMPRINT",EDGE,{"disambiguationData":[TD([[subQ2,1.0]])],"derivedFrom":subQ0}),1.0]])]});}
            var Q97;
            {var subQ0=sQuery(id+"F5.wireOp",EDGE,"E12.1.57.0");var subQ1=makeQuery(id+"F3.boolean.opBoolean","COPY",EDGE,{"derivedFrom":makeQuery(id+"F3.opExtrude","CAP_EDGE",EDGE,{"disambiguationData":[OSD([sQuery(id+"F2.wireOp",EDGE,"E6")])],"isStart":true})});var subQ2=makeQuery(id+"F5.imprint","INTERSECT",VERTEX,{"disambiguationData":[OD(0.0)],"derivedFrom":[subQ1,subQ0]});Q97=makeQuery(id+"F5.imprint","IMPRINT",FACE,{"disambiguationData":[TD([[makeQuery(id+"F5.imprint","IMPRINT",EDGE,{"disambiguationData":[TD([[subQ2,-1.0]])],"derivedFrom":subQ0}),1.0]])]});}
            var Q98;
            {var subQ0=sQuery(id+"F5.wireOp",EDGE,"E11.41.0");var subQ1=makeQuery(id+"F3.boolean.opBoolean","COPY",EDGE,{"derivedFrom":makeQuery(id+"F3.opExtrude","CAP_EDGE",EDGE,{"disambiguationData":[OSD([sQuery(id+"F2.wireOp",EDGE,"E6")])],"isStart":true})});var subQ2=makeQuery(id+"F5.imprint","INTERSECT",VERTEX,{"disambiguationData":[OD(0.0)],"derivedFrom":[subQ1,subQ0]});Q98=makeQuery(id+"F5.imprint","IMPRINT",FACE,{"disambiguationData":[TD([[makeQuery(id+"F5.imprint","IMPRINT",EDGE,{"disambiguationData":[TD([[subQ2,-1.0]])],"derivedFrom":subQ0}),1.0]])]});}
            var Q99;
            {var subQ0=sQuery(id+"F5.wireOp",EDGE,"E12.1.58.0");var subQ1=makeQuery(id+"F3.boolean.opBoolean","COPY",EDGE,{"derivedFrom":makeQuery(id+"F3.opExtrude","CAP_EDGE",EDGE,{"disambiguationData":[OSD([sQuery(id+"F2.wireOp",EDGE,"E6")])],"isStart":true})});var subQ2=makeQuery(id+"F5.imprint","INTERSECT",VERTEX,{"disambiguationData":[OD(0.0)],"derivedFrom":[subQ1,subQ0]});Q99=makeQuery(id+"F5.imprint","IMPRINT",FACE,{"disambiguationData":[TD([[makeQuery(id+"F5.imprint","IMPRINT",EDGE,{"disambiguationData":[TD([[subQ2,-1.0]])],"derivedFrom":subQ0}),1.0]])]});}
            var Q100;
            {var subQ0=sQuery(id+"F5.wireOp",EDGE,"E11.42.0");var subQ1=makeQuery(id+"F3.boolean.opBoolean","COPY",EDGE,{"derivedFrom":makeQuery(id+"F3.opExtrude","CAP_EDGE",EDGE,{"disambiguationData":[OSD([sQuery(id+"F2.wireOp",EDGE,"E6")])],"isStart":true})});var subQ2=makeQuery(id+"F5.imprint","INTERSECT",VERTEX,{"disambiguationData":[OD(0.0)],"derivedFrom":[subQ1,subQ0]});Q100=makeQuery(id+"F5.imprint","IMPRINT",FACE,{"disambiguationData":[TD([[makeQuery(id+"F5.imprint","IMPRINT",EDGE,{"disambiguationData":[TD([[subQ2,-1.0]])],"derivedFrom":subQ0}),1.0]])]});}
            var Q101;
            {var subQ0=sQuery(id+"F5.wireOp",EDGE,"E11.38.0");var subQ1=makeQuery(id+"F3.boolean.opBoolean","COPY",EDGE,{"derivedFrom":makeQuery(id+"F3.opExtrude","CAP_EDGE",EDGE,{"disambiguationData":[OSD([sQuery(id+"F2.wireOp",EDGE,"E6")])],"isStart":true})});var subQ2=makeQuery(id+"F5.imprint","INTERSECT",VERTEX,{"disambiguationData":[OD(0.0)],"derivedFrom":[subQ1,subQ0]});Q101=makeQuery(id+"F5.imprint","IMPRINT",FACE,{"disambiguationData":[TD([[makeQuery(id+"F5.imprint","IMPRINT",EDGE,{"disambiguationData":[TD([[subQ2,1.0]])],"derivedFrom":subQ0}),1.0]])]});}
            var Q102;
            {var subQ0=sQuery(id+"F5.wireOp",EDGE,"E11.43.0");var subQ1=makeQuery(id+"F3.boolean.opBoolean","COPY",EDGE,{"derivedFrom":makeQuery(id+"F3.opExtrude","CAP_EDGE",EDGE,{"disambiguationData":[OSD([sQuery(id+"F2.wireOp",EDGE,"E6")])],"isStart":true})});var subQ2=makeQuery(id+"F5.imprint","INTERSECT",VERTEX,{"disambiguationData":[OD(0.0)],"derivedFrom":[subQ1,subQ0]});Q102=makeQuery(id+"F5.imprint","IMPRINT",FACE,{"disambiguationData":[TD([[makeQuery(id+"F5.imprint","IMPRINT",EDGE,{"disambiguationData":[TD([[subQ2,-1.0]])],"derivedFrom":subQ0}),1.0]])]});}
            var Q103;
            {var subQ0=sQuery(id+"F5.wireOp",EDGE,"E11.43.0");var subQ1=makeQuery(id+"F3.boolean.opBoolean","COPY",EDGE,{"derivedFrom":makeQuery(id+"F3.opExtrude","CAP_EDGE",EDGE,{"disambiguationData":[OSD([sQuery(id+"F2.wireOp",EDGE,"E6")])],"isStart":true})});var subQ2=makeQuery(id+"F5.imprint","INTERSECT",VERTEX,{"disambiguationData":[OD(0.0)],"derivedFrom":[subQ1,subQ0]});Q103=makeQuery(id+"F5.imprint","IMPRINT",FACE,{"disambiguationData":[TD([[makeQuery(id+"F5.imprint","IMPRINT",EDGE,{"disambiguationData":[TD([[subQ2,1.0]])],"derivedFrom":subQ0}),1.0]])]});}
            var Q104;
            {var subQ0=sQuery(id+"F5.wireOp",EDGE,"E12.1.55.0");var subQ1=makeQuery(id+"F3.boolean.opBoolean","COPY",EDGE,{"derivedFrom":makeQuery(id+"F3.opExtrude","CAP_EDGE",EDGE,{"disambiguationData":[OSD([sQuery(id+"F2.wireOp",EDGE,"E6")])],"isStart":true})});var subQ2=makeQuery(id+"F5.imprint","INTERSECT",VERTEX,{"disambiguationData":[OD(0.0)],"derivedFrom":[subQ1,subQ0]});Q104=makeQuery(id+"F5.imprint","IMPRINT",FACE,{"disambiguationData":[TD([[makeQuery(id+"F5.imprint","IMPRINT",EDGE,{"disambiguationData":[TD([[subQ2,1.0]])],"derivedFrom":subQ0}),1.0]])]});}
            var Q105;
            {var subQ0=sQuery(id+"F5.wireOp",EDGE,"E11.44.0");var subQ1=makeQuery(id+"F3.boolean.opBoolean","COPY",EDGE,{"derivedFrom":makeQuery(id+"F3.opExtrude","CAP_EDGE",EDGE,{"disambiguationData":[OSD([sQuery(id+"F2.wireOp",EDGE,"E6")])],"isStart":true})});var subQ2=makeQuery(id+"F5.imprint","INTERSECT",VERTEX,{"disambiguationData":[OD(0.0)],"derivedFrom":[subQ1,subQ0]});Q105=makeQuery(id+"F5.imprint","IMPRINT",FACE,{"disambiguationData":[TD([[makeQuery(id+"F5.imprint","IMPRINT",EDGE,{"disambiguationData":[TD([[subQ2,-1.0]])],"derivedFrom":subQ0}),1.0]])]});}
            var Q106;
            {var subQ0=sQuery(id+"F5.wireOp",EDGE,"E11.40.0");var subQ1=makeQuery(id+"F3.boolean.opBoolean","COPY",EDGE,{"derivedFrom":makeQuery(id+"F3.opExtrude","CAP_EDGE",EDGE,{"disambiguationData":[OSD([sQuery(id+"F2.wireOp",EDGE,"E6")])],"isStart":true})});var subQ2=makeQuery(id+"F5.imprint","INTERSECT",VERTEX,{"disambiguationData":[OD(0.0)],"derivedFrom":[subQ1,subQ0]});Q106=makeQuery(id+"F5.imprint","IMPRINT",FACE,{"disambiguationData":[TD([[makeQuery(id+"F5.imprint","IMPRINT",EDGE,{"disambiguationData":[TD([[subQ2,1.0]])],"derivedFrom":subQ0}),1.0]])]});}
            var Q107;
            {var subQ0=sQuery(id+"F5.wireOp",EDGE,"E11.47.0");var subQ1=makeQuery(id+"F3.boolean.opBoolean","COPY",EDGE,{"derivedFrom":makeQuery(id+"F3.opExtrude","CAP_EDGE",EDGE,{"disambiguationData":[OSD([sQuery(id+"F2.wireOp",EDGE,"E6")])],"isStart":true})});var subQ2=makeQuery(id+"F5.imprint","INTERSECT",VERTEX,{"disambiguationData":[OD(0.0)],"derivedFrom":[subQ1,subQ0]});Q107=makeQuery(id+"F5.imprint","IMPRINT",FACE,{"disambiguationData":[TD([[makeQuery(id+"F5.imprint","IMPRINT",EDGE,{"disambiguationData":[TD([[subQ2,-1.0]])],"derivedFrom":subQ0}),1.0]])]});}
            var Q108;
            {var subQ0=sQuery(id+"F5.wireOp",EDGE,"E12.1.56.0");var subQ1=makeQuery(id+"F3.boolean.opBoolean","COPY",EDGE,{"derivedFrom":makeQuery(id+"F3.opExtrude","CAP_EDGE",EDGE,{"disambiguationData":[OSD([sQuery(id+"F2.wireOp",EDGE,"E6")])],"isStart":true})});var subQ2=makeQuery(id+"F5.imprint","INTERSECT",VERTEX,{"disambiguationData":[OD(0.0)],"derivedFrom":[subQ1,subQ0]});Q108=makeQuery(id+"F5.imprint","IMPRINT",FACE,{"disambiguationData":[TD([[makeQuery(id+"F5.imprint","IMPRINT",EDGE,{"disambiguationData":[TD([[subQ2,1.0]])],"derivedFrom":subQ0}),1.0]])]});}
            var Q109;
            {var subQ0=sQuery(id+"F5.wireOp",EDGE,"E11.46.0");var subQ1=makeQuery(id+"F3.boolean.opBoolean","COPY",EDGE,{"derivedFrom":makeQuery(id+"F3.opExtrude","CAP_EDGE",EDGE,{"disambiguationData":[OSD([sQuery(id+"F2.wireOp",EDGE,"E6")])],"isStart":true})});var subQ2=makeQuery(id+"F5.imprint","INTERSECT",VERTEX,{"disambiguationData":[OD(0.0)],"derivedFrom":[subQ1,subQ0]});Q109=makeQuery(id+"F5.imprint","IMPRINT",FACE,{"disambiguationData":[TD([[makeQuery(id+"F5.imprint","IMPRINT",EDGE,{"disambiguationData":[TD([[subQ2,1.0]])],"derivedFrom":subQ0}),1.0]])]});}
            var Q110;
            {var subQ0=sQuery(id+"F5.wireOp",EDGE,"E12.1.57.0");var subQ1=makeQuery(id+"F3.boolean.opBoolean","COPY",EDGE,{"derivedFrom":makeQuery(id+"F3.opExtrude","CAP_EDGE",EDGE,{"disambiguationData":[OSD([sQuery(id+"F2.wireOp",EDGE,"E6")])],"isStart":true})});var subQ2=makeQuery(id+"F5.imprint","INTERSECT",VERTEX,{"disambiguationData":[OD(0.0)],"derivedFrom":[subQ1,subQ0]});Q110=makeQuery(id+"F5.imprint","IMPRINT",FACE,{"disambiguationData":[TD([[makeQuery(id+"F5.imprint","IMPRINT",EDGE,{"disambiguationData":[TD([[subQ2,1.0]])],"derivedFrom":subQ0}),1.0]])]});}
            var Q111;
            {var subQ0=sQuery(id+"F5.wireOp",EDGE,"E12.1.52.0");var subQ1=makeQuery(id+"F3.boolean.opBoolean","COPY",EDGE,{"derivedFrom":makeQuery(id+"F3.opExtrude","CAP_EDGE",EDGE,{"disambiguationData":[OSD([sQuery(id+"F2.wireOp",EDGE,"E6")])],"isStart":true})});var subQ2=makeQuery(id+"F5.imprint","INTERSECT",VERTEX,{"disambiguationData":[OD(0.0)],"derivedFrom":[subQ1,subQ0]});Q111=makeQuery(id+"F5.imprint","IMPRINT",FACE,{"disambiguationData":[TD([[makeQuery(id+"F5.imprint","IMPRINT",EDGE,{"disambiguationData":[TD([[subQ2,-1.0]])],"derivedFrom":subQ0}),1.0]])]});}
            var Q112;
            {var subQ0=sQuery(id+"F5.wireOp",EDGE,"E12.1.53.0");var subQ1=makeQuery(id+"F3.boolean.opBoolean","COPY",EDGE,{"derivedFrom":makeQuery(id+"F3.opExtrude","CAP_EDGE",EDGE,{"disambiguationData":[OSD([sQuery(id+"F2.wireOp",EDGE,"E6")])],"isStart":true})});var subQ2=makeQuery(id+"F5.imprint","INTERSECT",VERTEX,{"disambiguationData":[OD(0.0)],"derivedFrom":[subQ1,subQ0]});Q112=makeQuery(id+"F5.imprint","IMPRINT",FACE,{"disambiguationData":[TD([[makeQuery(id+"F5.imprint","IMPRINT",EDGE,{"disambiguationData":[TD([[subQ2,-1.0]])],"derivedFrom":subQ0}),1.0]])]});}
            var Q113;
            {var subQ0=sQuery(id+"F5.wireOp",EDGE,"E11.49.0");var subQ1=makeQuery(id+"F3.boolean.opBoolean","COPY",EDGE,{"derivedFrom":makeQuery(id+"F3.opExtrude","CAP_EDGE",EDGE,{"disambiguationData":[OSD([sQuery(id+"F2.wireOp",EDGE,"E6")])],"isStart":true})});var subQ2=makeQuery(id+"F5.imprint","INTERSECT",VERTEX,{"disambiguationData":[OD(0.0)],"derivedFrom":[subQ1,subQ0]});Q113=makeQuery(id+"F5.imprint","IMPRINT",FACE,{"disambiguationData":[TD([[makeQuery(id+"F5.imprint","IMPRINT",EDGE,{"disambiguationData":[TD([[subQ2,1.0]])],"derivedFrom":subQ0}),1.0]])]});}
            var Q114;
            {var subQ0=sQuery(id+"F5.wireOp",EDGE,"E12.1.54.0");var subQ1=makeQuery(id+"F3.boolean.opBoolean","COPY",EDGE,{"derivedFrom":makeQuery(id+"F3.opExtrude","CAP_EDGE",EDGE,{"disambiguationData":[OSD([sQuery(id+"F2.wireOp",EDGE,"E6")])],"isStart":true})});var subQ2=makeQuery(id+"F5.imprint","INTERSECT",VERTEX,{"disambiguationData":[OD(0.0)],"derivedFrom":[subQ1,subQ0]});Q114=makeQuery(id+"F5.imprint","IMPRINT",FACE,{"disambiguationData":[TD([[makeQuery(id+"F5.imprint","IMPRINT",EDGE,{"disambiguationData":[TD([[subQ2,-1.0]])],"derivedFrom":subQ0}),1.0]])]});}
            var Q115;
            {var subQ0=sQuery(id+"F5.wireOp",EDGE,"E12.1.58.0");var subQ1=makeQuery(id+"F3.boolean.opBoolean","COPY",EDGE,{"derivedFrom":makeQuery(id+"F3.opExtrude","CAP_EDGE",EDGE,{"disambiguationData":[OSD([sQuery(id+"F2.wireOp",EDGE,"E6")])],"isStart":true})});var subQ2=makeQuery(id+"F5.imprint","INTERSECT",VERTEX,{"disambiguationData":[OD(0.0)],"derivedFrom":[subQ1,subQ0]});Q115=makeQuery(id+"F5.imprint","IMPRINT",FACE,{"disambiguationData":[TD([[makeQuery(id+"F5.imprint","IMPRINT",EDGE,{"disambiguationData":[TD([[subQ2,1.0]])],"derivedFrom":subQ0}),1.0]])]});}
            var Q116;
            {var subQ0=sQuery(id+"F5.wireOp",EDGE,"E11.42.0");var subQ1=makeQuery(id+"F3.boolean.opBoolean","COPY",EDGE,{"derivedFrom":makeQuery(id+"F3.opExtrude","CAP_EDGE",EDGE,{"disambiguationData":[OSD([sQuery(id+"F2.wireOp",EDGE,"E6")])],"isStart":true})});var subQ2=makeQuery(id+"F5.imprint","INTERSECT",VERTEX,{"disambiguationData":[OD(0.0)],"derivedFrom":[subQ1,subQ0]});Q116=makeQuery(id+"F5.imprint","IMPRINT",FACE,{"disambiguationData":[TD([[makeQuery(id+"F5.imprint","IMPRINT",EDGE,{"disambiguationData":[TD([[subQ2,1.0]])],"derivedFrom":subQ0}),1.0]])]});}
            var Q117;
            {var subQ0=sQuery(id+"F5.wireOp",EDGE,"E12.1.52.0");var subQ1=makeQuery(id+"F3.boolean.opBoolean","COPY",EDGE,{"derivedFrom":makeQuery(id+"F3.opExtrude","CAP_EDGE",EDGE,{"disambiguationData":[OSD([sQuery(id+"F2.wireOp",EDGE,"E6")])],"isStart":true})});var subQ2=makeQuery(id+"F5.imprint","INTERSECT",VERTEX,{"disambiguationData":[OD(0.0)],"derivedFrom":[subQ1,subQ0]});Q117=makeQuery(id+"F5.imprint","IMPRINT",FACE,{"disambiguationData":[TD([[makeQuery(id+"F5.imprint","IMPRINT",EDGE,{"disambiguationData":[TD([[subQ2,1.0]])],"derivedFrom":subQ0}),1.0]])]});}
            var Q118;
            {var subQ0=sQuery(id+"F5.wireOp",EDGE,"E12.1.54.0");var subQ1=makeQuery(id+"F3.boolean.opBoolean","COPY",EDGE,{"derivedFrom":makeQuery(id+"F3.opExtrude","CAP_EDGE",EDGE,{"disambiguationData":[OSD([sQuery(id+"F2.wireOp",EDGE,"E6")])],"isStart":true})});var subQ2=makeQuery(id+"F5.imprint","INTERSECT",VERTEX,{"disambiguationData":[OD(0.0)],"derivedFrom":[subQ1,subQ0]});Q118=makeQuery(id+"F5.imprint","IMPRINT",FACE,{"disambiguationData":[TD([[makeQuery(id+"F5.imprint","IMPRINT",EDGE,{"disambiguationData":[TD([[subQ2,1.0]])],"derivedFrom":subQ0}),1.0]])]});}
            var Q119;
            {var subQ0=sQuery(id+"F5.wireOp",EDGE,"E11.39.0");var subQ1=makeQuery(id+"F3.boolean.opBoolean","COPY",EDGE,{"derivedFrom":makeQuery(id+"F3.opExtrude","CAP_EDGE",EDGE,{"disambiguationData":[OSD([sQuery(id+"F2.wireOp",EDGE,"E6")])],"isStart":true})});var subQ2=makeQuery(id+"F5.imprint","INTERSECT",VERTEX,{"disambiguationData":[OD(0.0)],"derivedFrom":[subQ1,subQ0]});Q119=makeQuery(id+"F5.imprint","IMPRINT",FACE,{"disambiguationData":[TD([[makeQuery(id+"F5.imprint","IMPRINT",EDGE,{"disambiguationData":[TD([[subQ2,1.0]])],"derivedFrom":subQ0}),1.0]])]});}
            var Q120;
            {var subQ0=sQuery(id+"F5.wireOp",EDGE,"E12.1.53.0");var subQ1=makeQuery(id+"F3.boolean.opBoolean","COPY",EDGE,{"derivedFrom":makeQuery(id+"F3.opExtrude","CAP_EDGE",EDGE,{"disambiguationData":[OSD([sQuery(id+"F2.wireOp",EDGE,"E6")])],"isStart":true})});var subQ2=makeQuery(id+"F5.imprint","INTERSECT",VERTEX,{"disambiguationData":[OD(0.0)],"derivedFrom":[subQ1,subQ0]});Q120=makeQuery(id+"F5.imprint","IMPRINT",FACE,{"disambiguationData":[TD([[makeQuery(id+"F5.imprint","IMPRINT",EDGE,{"disambiguationData":[TD([[subQ2,1.0]])],"derivedFrom":subQ0}),1.0]])]});}
            var Q121;
            {var subQ0=sQuery(id+"F5.wireOp",EDGE,"E12.1.98.0");var subQ1=makeQuery(id+"F3.boolean.opBoolean","COPY",EDGE,{"derivedFrom":makeQuery(id+"F3.opExtrude","CAP_EDGE",EDGE,{"disambiguationData":[OSD([sQuery(id+"F2.wireOp",EDGE,"E6")])],"isStart":true})});var subQ2=makeQuery(id+"F5.imprint","INTERSECT",VERTEX,{"disambiguationData":[OD(0.0)],"derivedFrom":[subQ1,subQ0]});Q121=makeQuery(id+"F5.imprint","IMPRINT",FACE,{"disambiguationData":[TD([[makeQuery(id+"F5.imprint","IMPRINT",EDGE,{"disambiguationData":[TD([[subQ2,-1.0]])],"derivedFrom":subQ0}),1.0]])]});}
            var Q122;
            {var subQ0=sQuery(id+"F5.wireOp",EDGE,"E12.1.110.0");var subQ1=makeQuery(id+"F3.boolean.opBoolean","COPY",EDGE,{"derivedFrom":makeQuery(id+"F3.opExtrude","CAP_EDGE",EDGE,{"disambiguationData":[OSD([sQuery(id+"F2.wireOp",EDGE,"E6")])],"isStart":true})});var subQ2=makeQuery(id+"F5.imprint","INTERSECT",VERTEX,{"disambiguationData":[OD(0.0)],"derivedFrom":[subQ1,subQ0]});Q122=makeQuery(id+"F5.imprint","IMPRINT",FACE,{"disambiguationData":[TD([[makeQuery(id+"F5.imprint","IMPRINT",EDGE,{"disambiguationData":[TD([[subQ2,-1.0]])],"derivedFrom":subQ0}),1.0]])]});}
            var Q123;
            {var subQ0=sQuery(id+"F5.wireOp",EDGE,"E12.1.105.0");var subQ1=makeQuery(id+"F3.boolean.opBoolean","COPY",EDGE,{"derivedFrom":makeQuery(id+"F3.opExtrude","CAP_EDGE",EDGE,{"disambiguationData":[OSD([sQuery(id+"F2.wireOp",EDGE,"E6")])],"isStart":true})});var subQ2=makeQuery(id+"F5.imprint","INTERSECT",VERTEX,{"disambiguationData":[OD(0.0)],"derivedFrom":[subQ1,subQ0]});Q123=makeQuery(id+"F5.imprint","IMPRINT",FACE,{"disambiguationData":[TD([[makeQuery(id+"F5.imprint","IMPRINT",EDGE,{"disambiguationData":[TD([[subQ2,-1.0]])],"derivedFrom":subQ0}),1.0]])]});}
            var Q124;
            {var subQ0=sQuery(id+"F5.wireOp",EDGE,"E12.1.99.0");var subQ1=makeQuery(id+"F3.boolean.opBoolean","COPY",EDGE,{"derivedFrom":makeQuery(id+"F3.opExtrude","CAP_EDGE",EDGE,{"disambiguationData":[OSD([sQuery(id+"F2.wireOp",EDGE,"E6")])],"isStart":true})});var subQ2=makeQuery(id+"F5.imprint","INTERSECT",VERTEX,{"disambiguationData":[OD(0.0)],"derivedFrom":[subQ1,subQ0]});Q124=makeQuery(id+"F5.imprint","IMPRINT",FACE,{"disambiguationData":[TD([[makeQuery(id+"F5.imprint","IMPRINT",EDGE,{"disambiguationData":[TD([[subQ2,1.0]])],"derivedFrom":subQ0}),1.0]])]});}
            var Q125;
            {var subQ0=sQuery(id+"F5.wireOp",EDGE,"E12.1.59.0");var subQ1=makeQuery(id+"F3.boolean.opBoolean","COPY",EDGE,{"derivedFrom":makeQuery(id+"F3.opExtrude","CAP_EDGE",EDGE,{"disambiguationData":[OSD([sQuery(id+"F2.wireOp",EDGE,"E6")])],"isStart":true})});var subQ2=makeQuery(id+"F5.imprint","INTERSECT",VERTEX,{"disambiguationData":[OD(0.0)],"derivedFrom":[subQ1,subQ0]});Q125=makeQuery(id+"F5.imprint","IMPRINT",FACE,{"disambiguationData":[TD([[makeQuery(id+"F5.imprint","IMPRINT",EDGE,{"disambiguationData":[TD([[subQ2,1.0]])],"derivedFrom":subQ0}),1.0]])]});}
            var Q126;
            {var subQ0=sQuery(id+"F5.wireOp",EDGE,"E12.1.106.0");var subQ1=makeQuery(id+"F3.boolean.opBoolean","COPY",EDGE,{"derivedFrom":makeQuery(id+"F3.opExtrude","CAP_EDGE",EDGE,{"disambiguationData":[OSD([sQuery(id+"F2.wireOp",EDGE,"E6")])],"isStart":true})});var subQ2=makeQuery(id+"F5.imprint","INTERSECT",VERTEX,{"disambiguationData":[OD(0.0)],"derivedFrom":[subQ1,subQ0]});Q126=makeQuery(id+"F5.imprint","IMPRINT",FACE,{"disambiguationData":[TD([[makeQuery(id+"F5.imprint","IMPRINT",EDGE,{"disambiguationData":[TD([[subQ2,-1.0]])],"derivedFrom":subQ0}),1.0]])]});}
            var Q127;
            {var subQ0=sQuery(id+"F5.wireOp",EDGE,"E12.1.90.0");var subQ1=makeQuery(id+"F3.boolean.opBoolean","COPY",EDGE,{"derivedFrom":makeQuery(id+"F3.opExtrude","CAP_EDGE",EDGE,{"disambiguationData":[OSD([sQuery(id+"F2.wireOp",EDGE,"E6")])],"isStart":true})});var subQ2=makeQuery(id+"F5.imprint","INTERSECT",VERTEX,{"disambiguationData":[OD(0.0)],"derivedFrom":[subQ1,subQ0]});Q127=makeQuery(id+"F5.imprint","IMPRINT",FACE,{"disambiguationData":[TD([[makeQuery(id+"F5.imprint","IMPRINT",EDGE,{"disambiguationData":[TD([[subQ2,1.0]])],"derivedFrom":subQ0}),1.0]])]});}
            var Q128;
            {var subQ0=sQuery(id+"F5.wireOp",EDGE,"E12.1.77.0");var subQ1=makeQuery(id+"F3.boolean.opBoolean","COPY",EDGE,{"derivedFrom":makeQuery(id+"F3.opExtrude","CAP_EDGE",EDGE,{"disambiguationData":[OSD([sQuery(id+"F2.wireOp",EDGE,"E6")])],"isStart":true})});var subQ2=makeQuery(id+"F5.imprint","INTERSECT",VERTEX,{"disambiguationData":[OD(0.0)],"derivedFrom":[subQ1,subQ0]});Q128=makeQuery(id+"F5.imprint","IMPRINT",FACE,{"disambiguationData":[TD([[makeQuery(id+"F5.imprint","IMPRINT",EDGE,{"disambiguationData":[TD([[subQ2,-1.0]])],"derivedFrom":subQ0}),1.0]])]});}
            var Q129;
            {var subQ0=sQuery(id+"F5.wireOp",EDGE,"E12.1.97.0");var subQ1=makeQuery(id+"F3.boolean.opBoolean","COPY",EDGE,{"derivedFrom":makeQuery(id+"F3.opExtrude","CAP_EDGE",EDGE,{"disambiguationData":[OSD([sQuery(id+"F2.wireOp",EDGE,"E6")])],"isStart":true})});var subQ2=makeQuery(id+"F5.imprint","INTERSECT",VERTEX,{"disambiguationData":[OD(0.0)],"derivedFrom":[subQ1,subQ0]});Q129=makeQuery(id+"F5.imprint","IMPRINT",FACE,{"disambiguationData":[TD([[makeQuery(id+"F5.imprint","IMPRINT",EDGE,{"disambiguationData":[TD([[subQ2,-1.0]])],"derivedFrom":subQ0}),1.0]])]});}
            var Q130;
            {var subQ0=sQuery(id+"F5.wireOp",EDGE,"E12.1.61.0");var subQ1=makeQuery(id+"F3.boolean.opBoolean","COPY",EDGE,{"derivedFrom":makeQuery(id+"F3.opExtrude","CAP_EDGE",EDGE,{"disambiguationData":[OSD([sQuery(id+"F2.wireOp",EDGE,"E6")])],"isStart":true})});var subQ2=makeQuery(id+"F5.imprint","INTERSECT",VERTEX,{"disambiguationData":[OD(0.0)],"derivedFrom":[subQ1,subQ0]});Q130=makeQuery(id+"F5.imprint","IMPRINT",FACE,{"disambiguationData":[TD([[makeQuery(id+"F5.imprint","IMPRINT",EDGE,{"disambiguationData":[TD([[subQ2,1.0]])],"derivedFrom":subQ0}),1.0]])]});}
            var Q131;
            {var subQ0=sQuery(id+"F5.wireOp",EDGE,"E12.1.109.0");var subQ1=makeQuery(id+"F3.boolean.opBoolean","COPY",EDGE,{"derivedFrom":makeQuery(id+"F3.opExtrude","CAP_EDGE",EDGE,{"disambiguationData":[OSD([sQuery(id+"F2.wireOp",EDGE,"E6")])],"isStart":true})});var subQ2=makeQuery(id+"F5.imprint","INTERSECT",VERTEX,{"disambiguationData":[OD(0.0)],"derivedFrom":[subQ1,subQ0]});Q131=makeQuery(id+"F5.imprint","IMPRINT",FACE,{"disambiguationData":[TD([[makeQuery(id+"F5.imprint","IMPRINT",EDGE,{"disambiguationData":[TD([[subQ2,-1.0]])],"derivedFrom":subQ0}),1.0]])]});}
            var Q132;
            {var subQ0=sQuery(id+"F5.wireOp",EDGE,"E12.1.77.0");var subQ1=makeQuery(id+"F3.boolean.opBoolean","COPY",EDGE,{"derivedFrom":makeQuery(id+"F3.opExtrude","CAP_EDGE",EDGE,{"disambiguationData":[OSD([sQuery(id+"F2.wireOp",EDGE,"E6")])],"isStart":true})});var subQ2=makeQuery(id+"F5.imprint","INTERSECT",VERTEX,{"disambiguationData":[OD(0.0)],"derivedFrom":[subQ1,subQ0]});Q132=makeQuery(id+"F5.imprint","IMPRINT",FACE,{"disambiguationData":[TD([[makeQuery(id+"F5.imprint","IMPRINT",EDGE,{"disambiguationData":[TD([[subQ2,1.0]])],"derivedFrom":subQ0}),1.0]])]});}
            var Q133;
            {var subQ0=sQuery(id+"F5.wireOp",EDGE,"E12.1.66.0");var subQ1=makeQuery(id+"F3.boolean.opBoolean","COPY",EDGE,{"derivedFrom":makeQuery(id+"F3.opExtrude","CAP_EDGE",EDGE,{"disambiguationData":[OSD([sQuery(id+"F2.wireOp",EDGE,"E6")])],"isStart":true})});var subQ2=makeQuery(id+"F5.imprint","INTERSECT",VERTEX,{"disambiguationData":[OD(0.0)],"derivedFrom":[subQ1,subQ0]});Q133=makeQuery(id+"F5.imprint","IMPRINT",FACE,{"disambiguationData":[TD([[makeQuery(id+"F5.imprint","IMPRINT",EDGE,{"disambiguationData":[TD([[subQ2,-1.0]])],"derivedFrom":subQ0}),1.0]])]});}
            var Q134;
            {var subQ0=sQuery(id+"F5.wireOp",EDGE,"E12.1.62.0");var subQ1=makeQuery(id+"F3.boolean.opBoolean","COPY",EDGE,{"derivedFrom":makeQuery(id+"F3.opExtrude","CAP_EDGE",EDGE,{"disambiguationData":[OSD([sQuery(id+"F2.wireOp",EDGE,"E6")])],"isStart":true})});var subQ2=makeQuery(id+"F5.imprint","INTERSECT",VERTEX,{"disambiguationData":[OD(0.0)],"derivedFrom":[subQ1,subQ0]});Q134=makeQuery(id+"F5.imprint","IMPRINT",FACE,{"disambiguationData":[TD([[makeQuery(id+"F5.imprint","IMPRINT",EDGE,{"disambiguationData":[TD([[subQ2,-1.0]])],"derivedFrom":subQ0}),1.0]])]});}
            var Q135;
            {var subQ0=sQuery(id+"F5.wireOp",EDGE,"E12.1.65.0");var subQ1=makeQuery(id+"F3.boolean.opBoolean","COPY",EDGE,{"derivedFrom":makeQuery(id+"F3.opExtrude","CAP_EDGE",EDGE,{"disambiguationData":[OSD([sQuery(id+"F2.wireOp",EDGE,"E6")])],"isStart":true})});var subQ2=makeQuery(id+"F5.imprint","INTERSECT",VERTEX,{"disambiguationData":[OD(0.0)],"derivedFrom":[subQ1,subQ0]});Q135=makeQuery(id+"F5.imprint","IMPRINT",FACE,{"disambiguationData":[TD([[makeQuery(id+"F5.imprint","IMPRINT",EDGE,{"disambiguationData":[TD([[subQ2,-1.0]])],"derivedFrom":subQ0}),1.0]])]});}
            var Q136;
            {var subQ0=sQuery(id+"F5.wireOp",EDGE,"E12.1.62.0");var subQ1=makeQuery(id+"F3.boolean.opBoolean","COPY",EDGE,{"derivedFrom":makeQuery(id+"F3.opExtrude","CAP_EDGE",EDGE,{"disambiguationData":[OSD([sQuery(id+"F2.wireOp",EDGE,"E6")])],"isStart":true})});var subQ2=makeQuery(id+"F5.imprint","INTERSECT",VERTEX,{"disambiguationData":[OD(0.0)],"derivedFrom":[subQ1,subQ0]});Q136=makeQuery(id+"F5.imprint","IMPRINT",FACE,{"disambiguationData":[TD([[makeQuery(id+"F5.imprint","IMPRINT",EDGE,{"disambiguationData":[TD([[subQ2,1.0]])],"derivedFrom":subQ0}),1.0]])]});}
            var Q137;
            {var subQ0=sQuery(id+"F5.wireOp",EDGE,"E12.1.94.0");var subQ1=makeQuery(id+"F3.boolean.opBoolean","COPY",EDGE,{"derivedFrom":makeQuery(id+"F3.opExtrude","CAP_EDGE",EDGE,{"disambiguationData":[OSD([sQuery(id+"F2.wireOp",EDGE,"E6")])],"isStart":true})});var subQ2=makeQuery(id+"F5.imprint","INTERSECT",VERTEX,{"disambiguationData":[OD(0.0)],"derivedFrom":[subQ1,subQ0]});Q137=makeQuery(id+"F5.imprint","IMPRINT",FACE,{"disambiguationData":[TD([[makeQuery(id+"F5.imprint","IMPRINT",EDGE,{"disambiguationData":[TD([[subQ2,1.0]])],"derivedFrom":subQ0}),1.0]])]});}
            var Q138;
            {var subQ0=sQuery(id+"F5.wireOp",EDGE,"E12.1.78.0");var subQ1=makeQuery(id+"F3.boolean.opBoolean","COPY",EDGE,{"derivedFrom":makeQuery(id+"F3.opExtrude","CAP_EDGE",EDGE,{"disambiguationData":[OSD([sQuery(id+"F2.wireOp",EDGE,"E6")])],"isStart":true})});var subQ2=makeQuery(id+"F5.imprint","INTERSECT",VERTEX,{"disambiguationData":[OD(0.0)],"derivedFrom":[subQ1,subQ0]});Q138=makeQuery(id+"F5.imprint","IMPRINT",FACE,{"disambiguationData":[TD([[makeQuery(id+"F5.imprint","IMPRINT",EDGE,{"disambiguationData":[TD([[subQ2,1.0]])],"derivedFrom":subQ0}),1.0]])]});}
            var Q139;
            {var subQ0=sQuery(id+"F5.wireOp",EDGE,"E12.1.76.0");var subQ1=makeQuery(id+"F3.boolean.opBoolean","COPY",EDGE,{"derivedFrom":makeQuery(id+"F3.opExtrude","CAP_EDGE",EDGE,{"disambiguationData":[OSD([sQuery(id+"F2.wireOp",EDGE,"E6")])],"isStart":true})});var subQ2=makeQuery(id+"F5.imprint","INTERSECT",VERTEX,{"disambiguationData":[OD(0.0)],"derivedFrom":[subQ1,subQ0]});Q139=makeQuery(id+"F5.imprint","IMPRINT",FACE,{"disambiguationData":[TD([[makeQuery(id+"F5.imprint","IMPRINT",EDGE,{"disambiguationData":[TD([[subQ2,1.0]])],"derivedFrom":subQ0}),1.0]])]});}
            var Q140;
            {var subQ0=sQuery(id+"F5.wireOp",EDGE,"E12.1.92.0");var subQ1=makeQuery(id+"F3.boolean.opBoolean","COPY",EDGE,{"derivedFrom":makeQuery(id+"F3.opExtrude","CAP_EDGE",EDGE,{"disambiguationData":[OSD([sQuery(id+"F2.wireOp",EDGE,"E6")])],"isStart":true})});var subQ2=makeQuery(id+"F5.imprint","INTERSECT",VERTEX,{"disambiguationData":[OD(0.0)],"derivedFrom":[subQ1,subQ0]});Q140=makeQuery(id+"F5.imprint","IMPRINT",FACE,{"disambiguationData":[TD([[makeQuery(id+"F5.imprint","IMPRINT",EDGE,{"disambiguationData":[TD([[subQ2,1.0]])],"derivedFrom":subQ0}),1.0]])]});}
            var Q141;
            {var subQ0=sQuery(id+"F5.wireOp",EDGE,"E12.1.108.0");var subQ1=makeQuery(id+"F3.boolean.opBoolean","COPY",EDGE,{"derivedFrom":makeQuery(id+"F3.opExtrude","CAP_EDGE",EDGE,{"disambiguationData":[OSD([sQuery(id+"F2.wireOp",EDGE,"E6")])],"isStart":true})});var subQ2=makeQuery(id+"F5.imprint","INTERSECT",VERTEX,{"disambiguationData":[OD(0.0)],"derivedFrom":[subQ1,subQ0]});Q141=makeQuery(id+"F5.imprint","IMPRINT",FACE,{"disambiguationData":[TD([[makeQuery(id+"F5.imprint","IMPRINT",EDGE,{"disambiguationData":[TD([[subQ2,-1.0]])],"derivedFrom":subQ0}),1.0]])]});}
            var Q142;
            {var subQ0=sQuery(id+"F5.wireOp",EDGE,"E12.1.60.0");var subQ1=makeQuery(id+"F3.boolean.opBoolean","COPY",EDGE,{"derivedFrom":makeQuery(id+"F3.opExtrude","CAP_EDGE",EDGE,{"disambiguationData":[OSD([sQuery(id+"F2.wireOp",EDGE,"E6")])],"isStart":true})});var subQ2=makeQuery(id+"F5.imprint","INTERSECT",VERTEX,{"disambiguationData":[OD(0.0)],"derivedFrom":[subQ1,subQ0]});Q142=makeQuery(id+"F5.imprint","IMPRINT",FACE,{"disambiguationData":[TD([[makeQuery(id+"F5.imprint","IMPRINT",EDGE,{"disambiguationData":[TD([[subQ2,1.0]])],"derivedFrom":subQ0}),1.0]])]});}
            var Q143;
            {var subQ0=sQuery(id+"F5.wireOp",EDGE,"E12.1.96.0");var subQ1=makeQuery(id+"F3.boolean.opBoolean","COPY",EDGE,{"derivedFrom":makeQuery(id+"F3.opExtrude","CAP_EDGE",EDGE,{"disambiguationData":[OSD([sQuery(id+"F2.wireOp",EDGE,"E6")])],"isStart":true})});var subQ2=makeQuery(id+"F5.imprint","INTERSECT",VERTEX,{"disambiguationData":[OD(0.0)],"derivedFrom":[subQ1,subQ0]});Q143=makeQuery(id+"F5.imprint","IMPRINT",FACE,{"disambiguationData":[TD([[makeQuery(id+"F5.imprint","IMPRINT",EDGE,{"disambiguationData":[TD([[subQ2,-1.0]])],"derivedFrom":subQ0}),1.0]])]});}
            var Q144;
            {var subQ0=sQuery(id+"F5.wireOp",EDGE,"E12.1.64.0");var subQ1=makeQuery(id+"F3.boolean.opBoolean","COPY",EDGE,{"derivedFrom":makeQuery(id+"F3.opExtrude","CAP_EDGE",EDGE,{"disambiguationData":[OSD([sQuery(id+"F2.wireOp",EDGE,"E6")])],"isStart":true})});var subQ2=makeQuery(id+"F5.imprint","INTERSECT",VERTEX,{"disambiguationData":[OD(0.0)],"derivedFrom":[subQ1,subQ0]});Q144=makeQuery(id+"F5.imprint","IMPRINT",FACE,{"disambiguationData":[TD([[makeQuery(id+"F5.imprint","IMPRINT",EDGE,{"disambiguationData":[TD([[subQ2,-1.0]])],"derivedFrom":subQ0}),1.0]])]});}
            var Q145;
            {var subQ0=sQuery(id+"F5.wireOp",EDGE,"E12.1.78.0");var subQ1=makeQuery(id+"F3.boolean.opBoolean","COPY",EDGE,{"derivedFrom":makeQuery(id+"F3.opExtrude","CAP_EDGE",EDGE,{"disambiguationData":[OSD([sQuery(id+"F2.wireOp",EDGE,"E6")])],"isStart":true})});var subQ2=makeQuery(id+"F5.imprint","INTERSECT",VERTEX,{"disambiguationData":[OD(0.0)],"derivedFrom":[subQ1,subQ0]});Q145=makeQuery(id+"F5.imprint","IMPRINT",FACE,{"disambiguationData":[TD([[makeQuery(id+"F5.imprint","IMPRINT",EDGE,{"disambiguationData":[TD([[subQ2,-1.0]])],"derivedFrom":subQ0}),1.0]])]});}
            var Q146;
            {var subQ0=sQuery(id+"F5.wireOp",EDGE,"E12.1.74.0");var subQ1=makeQuery(id+"F3.boolean.opBoolean","COPY",EDGE,{"derivedFrom":makeQuery(id+"F3.opExtrude","CAP_EDGE",EDGE,{"disambiguationData":[OSD([sQuery(id+"F2.wireOp",EDGE,"E6")])],"isStart":true})});var subQ2=makeQuery(id+"F5.imprint","INTERSECT",VERTEX,{"disambiguationData":[OD(0.0)],"derivedFrom":[subQ1,subQ0]});Q146=makeQuery(id+"F5.imprint","IMPRINT",FACE,{"disambiguationData":[TD([[makeQuery(id+"F5.imprint","IMPRINT",EDGE,{"disambiguationData":[TD([[subQ2,1.0]])],"derivedFrom":subQ0}),1.0]])]});}
            var Q147;
            {var subQ0=sQuery(id+"F5.wireOp",EDGE,"E12.1.67.0");var subQ1=makeQuery(id+"F3.boolean.opBoolean","COPY",EDGE,{"derivedFrom":makeQuery(id+"F3.opExtrude","CAP_EDGE",EDGE,{"disambiguationData":[OSD([sQuery(id+"F2.wireOp",EDGE,"E6")])],"isStart":true})});var subQ2=makeQuery(id+"F5.imprint","INTERSECT",VERTEX,{"disambiguationData":[OD(0.0)],"derivedFrom":[subQ1,subQ0]});Q147=makeQuery(id+"F5.imprint","IMPRINT",FACE,{"disambiguationData":[TD([[makeQuery(id+"F5.imprint","IMPRINT",EDGE,{"disambiguationData":[TD([[subQ2,-1.0]])],"derivedFrom":subQ0}),1.0]])]});}
            var Q148;
            {var subQ0=sQuery(id+"F5.wireOp",EDGE,"E12.1.109.0");var subQ1=makeQuery(id+"F3.boolean.opBoolean","COPY",EDGE,{"derivedFrom":makeQuery(id+"F3.opExtrude","CAP_EDGE",EDGE,{"disambiguationData":[OSD([sQuery(id+"F2.wireOp",EDGE,"E6")])],"isStart":true})});var subQ2=makeQuery(id+"F5.imprint","INTERSECT",VERTEX,{"disambiguationData":[OD(0.0)],"derivedFrom":[subQ1,subQ0]});Q148=makeQuery(id+"F5.imprint","IMPRINT",FACE,{"disambiguationData":[TD([[makeQuery(id+"F5.imprint","IMPRINT",EDGE,{"disambiguationData":[TD([[subQ2,1.0]])],"derivedFrom":subQ0}),1.0]])]});}
            var Q149;
            {var subQ0=sQuery(id+"F5.wireOp",EDGE,"E12.1.99.0");var subQ1=makeQuery(id+"F3.boolean.opBoolean","COPY",EDGE,{"derivedFrom":makeQuery(id+"F3.opExtrude","CAP_EDGE",EDGE,{"disambiguationData":[OSD([sQuery(id+"F2.wireOp",EDGE,"E6")])],"isStart":true})});var subQ2=makeQuery(id+"F5.imprint","INTERSECT",VERTEX,{"disambiguationData":[OD(0.0)],"derivedFrom":[subQ1,subQ0]});Q149=makeQuery(id+"F5.imprint","IMPRINT",FACE,{"disambiguationData":[TD([[makeQuery(id+"F5.imprint","IMPRINT",EDGE,{"disambiguationData":[TD([[subQ2,-1.0]])],"derivedFrom":subQ0}),1.0]])]});}
            var Q150;
            {var subQ0=sQuery(id+"F5.wireOp",EDGE,"E12.1.63.0");var subQ1=makeQuery(id+"F3.boolean.opBoolean","COPY",EDGE,{"derivedFrom":makeQuery(id+"F3.opExtrude","CAP_EDGE",EDGE,{"disambiguationData":[OSD([sQuery(id+"F2.wireOp",EDGE,"E6")])],"isStart":true})});var subQ2=makeQuery(id+"F5.imprint","INTERSECT",VERTEX,{"disambiguationData":[OD(0.0)],"derivedFrom":[subQ1,subQ0]});Q150=makeQuery(id+"F5.imprint","IMPRINT",FACE,{"disambiguationData":[TD([[makeQuery(id+"F5.imprint","IMPRINT",EDGE,{"disambiguationData":[TD([[subQ2,1.0]])],"derivedFrom":subQ0}),1.0]])]});}
            var Q151;
            {var subQ0=sQuery(id+"F5.wireOp",EDGE,"E12.1.79.0");var subQ1=makeQuery(id+"F3.boolean.opBoolean","COPY",EDGE,{"derivedFrom":makeQuery(id+"F3.opExtrude","CAP_EDGE",EDGE,{"disambiguationData":[OSD([sQuery(id+"F2.wireOp",EDGE,"E6")])],"isStart":true})});var subQ2=makeQuery(id+"F5.imprint","INTERSECT",VERTEX,{"disambiguationData":[OD(0.0)],"derivedFrom":[subQ1,subQ0]});Q151=makeQuery(id+"F5.imprint","IMPRINT",FACE,{"disambiguationData":[TD([[makeQuery(id+"F5.imprint","IMPRINT",EDGE,{"disambiguationData":[TD([[subQ2,1.0]])],"derivedFrom":subQ0}),1.0]])]});}
            var Q152;
            {var subQ0=sQuery(id+"F5.wireOp",EDGE,"E12.1.95.0");var subQ1=makeQuery(id+"F3.boolean.opBoolean","COPY",EDGE,{"derivedFrom":makeQuery(id+"F3.opExtrude","CAP_EDGE",EDGE,{"disambiguationData":[OSD([sQuery(id+"F2.wireOp",EDGE,"E6")])],"isStart":true})});var subQ2=makeQuery(id+"F5.imprint","INTERSECT",VERTEX,{"disambiguationData":[OD(0.0)],"derivedFrom":[subQ1,subQ0]});Q152=makeQuery(id+"F5.imprint","IMPRINT",FACE,{"disambiguationData":[TD([[makeQuery(id+"F5.imprint","IMPRINT",EDGE,{"disambiguationData":[TD([[subQ2,1.0]])],"derivedFrom":subQ0}),1.0]])]});}
            var Q153;
            {var subQ0=sQuery(id+"F5.wireOp",EDGE,"E12.1.93.0");var subQ1=makeQuery(id+"F3.boolean.opBoolean","COPY",EDGE,{"derivedFrom":makeQuery(id+"F3.opExtrude","CAP_EDGE",EDGE,{"disambiguationData":[OSD([sQuery(id+"F2.wireOp",EDGE,"E6")])],"isStart":true})});var subQ2=makeQuery(id+"F5.imprint","INTERSECT",VERTEX,{"disambiguationData":[OD(0.0)],"derivedFrom":[subQ1,subQ0]});Q153=makeQuery(id+"F5.imprint","IMPRINT",FACE,{"disambiguationData":[TD([[makeQuery(id+"F5.imprint","IMPRINT",EDGE,{"disambiguationData":[TD([[subQ2,-1.0]])],"derivedFrom":subQ0}),1.0]])]});}
            var Q154;
            {var subQ0=sQuery(id+"F5.wireOp",EDGE,"E12.1.68.0");var subQ1=makeQuery(id+"F3.boolean.opBoolean","COPY",EDGE,{"derivedFrom":makeQuery(id+"F3.opExtrude","CAP_EDGE",EDGE,{"disambiguationData":[OSD([sQuery(id+"F2.wireOp",EDGE,"E6")])],"isStart":true})});var subQ2=makeQuery(id+"F5.imprint","INTERSECT",VERTEX,{"disambiguationData":[OD(0.0)],"derivedFrom":[subQ1,subQ0]});Q154=makeQuery(id+"F5.imprint","IMPRINT",FACE,{"disambiguationData":[TD([[makeQuery(id+"F5.imprint","IMPRINT",EDGE,{"disambiguationData":[TD([[subQ2,-1.0]])],"derivedFrom":subQ0}),1.0]])]});}
            var Q155;
            {var subQ0=sQuery(id+"F5.wireOp",EDGE,"E12.1.64.0");var subQ1=makeQuery(id+"F3.boolean.opBoolean","COPY",EDGE,{"derivedFrom":makeQuery(id+"F3.opExtrude","CAP_EDGE",EDGE,{"disambiguationData":[OSD([sQuery(id+"F2.wireOp",EDGE,"E6")])],"isStart":true})});var subQ2=makeQuery(id+"F5.imprint","INTERSECT",VERTEX,{"disambiguationData":[OD(0.0)],"derivedFrom":[subQ1,subQ0]});Q155=makeQuery(id+"F5.imprint","IMPRINT",FACE,{"disambiguationData":[TD([[makeQuery(id+"F5.imprint","IMPRINT",EDGE,{"disambiguationData":[TD([[subQ2,1.0]])],"derivedFrom":subQ0}),1.0]])]});}
            var Q156;
            {var subQ0=sQuery(id+"F5.wireOp",EDGE,"E12.1.89.0");var subQ1=makeQuery(id+"F3.boolean.opBoolean","COPY",EDGE,{"derivedFrom":makeQuery(id+"F3.opExtrude","CAP_EDGE",EDGE,{"disambiguationData":[OSD([sQuery(id+"F2.wireOp",EDGE,"E6")])],"isStart":true})});var subQ2=makeQuery(id+"F5.imprint","INTERSECT",VERTEX,{"disambiguationData":[OD(0.0)],"derivedFrom":[subQ1,subQ0]});Q156=makeQuery(id+"F5.imprint","IMPRINT",FACE,{"disambiguationData":[TD([[makeQuery(id+"F5.imprint","IMPRINT",EDGE,{"disambiguationData":[TD([[subQ2,1.0]])],"derivedFrom":subQ0}),1.0]])]});}
            var Q157;
            {var subQ0=sQuery(id+"F5.wireOp",EDGE,"E12.1.73.0");var subQ1=makeQuery(id+"F3.boolean.opBoolean","COPY",EDGE,{"derivedFrom":makeQuery(id+"F3.opExtrude","CAP_EDGE",EDGE,{"disambiguationData":[OSD([sQuery(id+"F2.wireOp",EDGE,"E6")])],"isStart":true})});var subQ2=makeQuery(id+"F5.imprint","INTERSECT",VERTEX,{"disambiguationData":[OD(0.0)],"derivedFrom":[subQ1,subQ0]});Q157=makeQuery(id+"F5.imprint","IMPRINT",FACE,{"disambiguationData":[TD([[makeQuery(id+"F5.imprint","IMPRINT",EDGE,{"disambiguationData":[TD([[subQ2,1.0]])],"derivedFrom":subQ0}),1.0]])]});}
            var Q158;
            {var subQ0=sQuery(id+"F5.wireOp",EDGE,"E12.1.96.0");var subQ1=makeQuery(id+"F3.boolean.opBoolean","COPY",EDGE,{"derivedFrom":makeQuery(id+"F3.opExtrude","CAP_EDGE",EDGE,{"disambiguationData":[OSD([sQuery(id+"F2.wireOp",EDGE,"E6")])],"isStart":true})});var subQ2=makeQuery(id+"F5.imprint","INTERSECT",VERTEX,{"disambiguationData":[OD(0.0)],"derivedFrom":[subQ1,subQ0]});Q158=makeQuery(id+"F5.imprint","IMPRINT",FACE,{"disambiguationData":[TD([[makeQuery(id+"F5.imprint","IMPRINT",EDGE,{"disambiguationData":[TD([[subQ2,1.0]])],"derivedFrom":subQ0}),1.0]])]});}
            var Q159;
            {var subQ0=sQuery(id+"F5.wireOp",EDGE,"E12.1.110.0");var subQ1=makeQuery(id+"F3.boolean.opBoolean","COPY",EDGE,{"derivedFrom":makeQuery(id+"F3.opExtrude","CAP_EDGE",EDGE,{"disambiguationData":[OSD([sQuery(id+"F2.wireOp",EDGE,"E6")])],"isStart":true})});var subQ2=makeQuery(id+"F5.imprint","INTERSECT",VERTEX,{"disambiguationData":[OD(0.0)],"derivedFrom":[subQ1,subQ0]});Q159=makeQuery(id+"F5.imprint","IMPRINT",FACE,{"disambiguationData":[TD([[makeQuery(id+"F5.imprint","IMPRINT",EDGE,{"disambiguationData":[TD([[subQ2,1.0]])],"derivedFrom":subQ0}),1.0]])]});}
            var Q160;
            {var subQ0=sQuery(id+"F5.wireOp",EDGE,"E12.1.85.0");var subQ1=makeQuery(id+"F3.boolean.opBoolean","COPY",EDGE,{"derivedFrom":makeQuery(id+"F3.opExtrude","CAP_EDGE",EDGE,{"disambiguationData":[OSD([sQuery(id+"F2.wireOp",EDGE,"E6")])],"isStart":true})});var subQ2=makeQuery(id+"F5.imprint","INTERSECT",VERTEX,{"disambiguationData":[OD(0.0)],"derivedFrom":[subQ1,subQ0]});Q160=makeQuery(id+"F5.imprint","IMPRINT",FACE,{"disambiguationData":[TD([[makeQuery(id+"F5.imprint","IMPRINT",EDGE,{"disambiguationData":[TD([[subQ2,-1.0]])],"derivedFrom":subQ0}),1.0]])]});}
            var Q161;
            {var subQ0=sQuery(id+"F5.wireOp",EDGE,"E12.1.69.0");var subQ1=makeQuery(id+"F3.boolean.opBoolean","COPY",EDGE,{"derivedFrom":makeQuery(id+"F3.opExtrude","CAP_EDGE",EDGE,{"disambiguationData":[OSD([sQuery(id+"F2.wireOp",EDGE,"E6")])],"isStart":true})});var subQ2=makeQuery(id+"F5.imprint","INTERSECT",VERTEX,{"disambiguationData":[OD(0.0)],"derivedFrom":[subQ1,subQ0]});Q161=makeQuery(id+"F5.imprint","IMPRINT",FACE,{"disambiguationData":[TD([[makeQuery(id+"F5.imprint","IMPRINT",EDGE,{"disambiguationData":[TD([[subQ2,-1.0]])],"derivedFrom":subQ0}),1.0]])]});}
            var Q162;
            {var subQ0=sQuery(id+"F5.wireOp",EDGE,"E12.1.97.0");var subQ1=makeQuery(id+"F3.boolean.opBoolean","COPY",EDGE,{"derivedFrom":makeQuery(id+"F3.opExtrude","CAP_EDGE",EDGE,{"disambiguationData":[OSD([sQuery(id+"F2.wireOp",EDGE,"E6")])],"isStart":true})});var subQ2=makeQuery(id+"F5.imprint","INTERSECT",VERTEX,{"disambiguationData":[OD(0.0)],"derivedFrom":[subQ1,subQ0]});Q162=makeQuery(id+"F5.imprint","IMPRINT",FACE,{"disambiguationData":[TD([[makeQuery(id+"F5.imprint","IMPRINT",EDGE,{"disambiguationData":[TD([[subQ2,1.0]])],"derivedFrom":subQ0}),1.0]])]});}
            var Q163;
            {var subQ0=sQuery(id+"F5.wireOp",EDGE,"E12.1.94.0");var subQ1=makeQuery(id+"F3.boolean.opBoolean","COPY",EDGE,{"derivedFrom":makeQuery(id+"F3.opExtrude","CAP_EDGE",EDGE,{"disambiguationData":[OSD([sQuery(id+"F2.wireOp",EDGE,"E6")])],"isStart":true})});var subQ2=makeQuery(id+"F5.imprint","INTERSECT",VERTEX,{"disambiguationData":[OD(0.0)],"derivedFrom":[subQ1,subQ0]});Q163=makeQuery(id+"F5.imprint","IMPRINT",FACE,{"disambiguationData":[TD([[makeQuery(id+"F5.imprint","IMPRINT",EDGE,{"disambiguationData":[TD([[subQ2,-1.0]])],"derivedFrom":subQ0}),1.0]])]});}
            var Q164;
            {var subQ0=sQuery(id+"F5.wireOp",EDGE,"E12.1.102.0");var subQ1=makeQuery(id+"F3.boolean.opBoolean","COPY",EDGE,{"derivedFrom":makeQuery(id+"F3.opExtrude","CAP_EDGE",EDGE,{"disambiguationData":[OSD([sQuery(id+"F2.wireOp",EDGE,"E6")])],"isStart":true})});var subQ2=makeQuery(id+"F5.imprint","INTERSECT",VERTEX,{"disambiguationData":[OD(0.0)],"derivedFrom":[subQ1,subQ0]});Q164=makeQuery(id+"F5.imprint","IMPRINT",FACE,{"disambiguationData":[TD([[makeQuery(id+"F5.imprint","IMPRINT",EDGE,{"disambiguationData":[TD([[subQ2,1.0]])],"derivedFrom":subQ0}),1.0]])]});}
            var Q165;
            {var subQ0=sQuery(id+"F5.wireOp",EDGE,"E12.1.70.0");var subQ1=makeQuery(id+"F3.boolean.opBoolean","COPY",EDGE,{"derivedFrom":makeQuery(id+"F3.opExtrude","CAP_EDGE",EDGE,{"disambiguationData":[OSD([sQuery(id+"F2.wireOp",EDGE,"E6")])],"isStart":true})});var subQ2=makeQuery(id+"F5.imprint","INTERSECT",VERTEX,{"disambiguationData":[OD(0.0)],"derivedFrom":[subQ1,subQ0]});Q165=makeQuery(id+"F5.imprint","IMPRINT",FACE,{"disambiguationData":[TD([[makeQuery(id+"F5.imprint","IMPRINT",EDGE,{"disambiguationData":[TD([[subQ2,-1.0]])],"derivedFrom":subQ0}),1.0]])]});}
            var Q166;
            {var subQ0=sQuery(id+"F5.wireOp",EDGE,"E12.1.86.0");var subQ1=makeQuery(id+"F3.boolean.opBoolean","COPY",EDGE,{"derivedFrom":makeQuery(id+"F3.opExtrude","CAP_EDGE",EDGE,{"disambiguationData":[OSD([sQuery(id+"F2.wireOp",EDGE,"E6")])],"isStart":true})});var subQ2=makeQuery(id+"F5.imprint","INTERSECT",VERTEX,{"disambiguationData":[OD(0.0)],"derivedFrom":[subQ1,subQ0]});Q166=makeQuery(id+"F5.imprint","IMPRINT",FACE,{"disambiguationData":[TD([[makeQuery(id+"F5.imprint","IMPRINT",EDGE,{"disambiguationData":[TD([[subQ2,-1.0]])],"derivedFrom":subQ0}),1.0]])]});}
            var Q167;
            {var subQ0=sQuery(id+"F5.wireOp",EDGE,"E12.1.98.0");var subQ1=makeQuery(id+"F3.boolean.opBoolean","COPY",EDGE,{"derivedFrom":makeQuery(id+"F3.opExtrude","CAP_EDGE",EDGE,{"disambiguationData":[OSD([sQuery(id+"F2.wireOp",EDGE,"E6")])],"isStart":true})});var subQ2=makeQuery(id+"F5.imprint","INTERSECT",VERTEX,{"disambiguationData":[OD(0.0)],"derivedFrom":[subQ1,subQ0]});Q167=makeQuery(id+"F5.imprint","IMPRINT",FACE,{"disambiguationData":[TD([[makeQuery(id+"F5.imprint","IMPRINT",EDGE,{"disambiguationData":[TD([[subQ2,1.0]])],"derivedFrom":subQ0}),1.0]])]});}
            var Q168;
            {var subQ0=sQuery(id+"F5.wireOp",EDGE,"E12.1.66.0");var subQ1=makeQuery(id+"F3.boolean.opBoolean","COPY",EDGE,{"derivedFrom":makeQuery(id+"F3.opExtrude","CAP_EDGE",EDGE,{"disambiguationData":[OSD([sQuery(id+"F2.wireOp",EDGE,"E6")])],"isStart":true})});var subQ2=makeQuery(id+"F5.imprint","INTERSECT",VERTEX,{"disambiguationData":[OD(0.0)],"derivedFrom":[subQ1,subQ0]});Q168=makeQuery(id+"F5.imprint","IMPRINT",FACE,{"disambiguationData":[TD([[makeQuery(id+"F5.imprint","IMPRINT",EDGE,{"disambiguationData":[TD([[subQ2,1.0]])],"derivedFrom":subQ0}),1.0]])]});}
            var Q169;
            {var subQ0=sQuery(id+"F5.wireOp",EDGE,"E12.1.87.0");var subQ1=makeQuery(id+"F3.boolean.opBoolean","COPY",EDGE,{"derivedFrom":makeQuery(id+"F3.opExtrude","CAP_EDGE",EDGE,{"disambiguationData":[OSD([sQuery(id+"F2.wireOp",EDGE,"E6")])],"isStart":true})});var subQ2=makeQuery(id+"F5.imprint","INTERSECT",VERTEX,{"disambiguationData":[OD(0.0)],"derivedFrom":[subQ1,subQ0]});Q169=makeQuery(id+"F5.imprint","IMPRINT",FACE,{"disambiguationData":[TD([[makeQuery(id+"F5.imprint","IMPRINT",EDGE,{"disambiguationData":[TD([[subQ2,-1.0]])],"derivedFrom":subQ0}),1.0]])]});}
            var Q170;
            {var subQ0=sQuery(id+"F5.wireOp",EDGE,"E12.1.103.0");var subQ1=makeQuery(id+"F3.boolean.opBoolean","COPY",EDGE,{"derivedFrom":makeQuery(id+"F3.opExtrude","CAP_EDGE",EDGE,{"disambiguationData":[OSD([sQuery(id+"F2.wireOp",EDGE,"E6")])],"isStart":true})});var subQ2=makeQuery(id+"F5.imprint","INTERSECT",VERTEX,{"disambiguationData":[OD(0.0)],"derivedFrom":[subQ1,subQ0]});Q170=makeQuery(id+"F5.imprint","IMPRINT",FACE,{"disambiguationData":[TD([[makeQuery(id+"F5.imprint","IMPRINT",EDGE,{"disambiguationData":[TD([[subQ2,1.0]])],"derivedFrom":subQ0}),1.0]])]});}
            var Q171;
            {var subQ0=sQuery(id+"F5.wireOp",EDGE,"E12.1.71.0");var subQ1=makeQuery(id+"F3.boolean.opBoolean","COPY",EDGE,{"derivedFrom":makeQuery(id+"F3.opExtrude","CAP_EDGE",EDGE,{"disambiguationData":[OSD([sQuery(id+"F2.wireOp",EDGE,"E6")])],"isStart":true})});var subQ2=makeQuery(id+"F5.imprint","INTERSECT",VERTEX,{"disambiguationData":[OD(0.0)],"derivedFrom":[subQ1,subQ0]});Q171=makeQuery(id+"F5.imprint","IMPRINT",FACE,{"disambiguationData":[TD([[makeQuery(id+"F5.imprint","IMPRINT",EDGE,{"disambiguationData":[TD([[subQ2,-1.0]])],"derivedFrom":subQ0}),1.0]])]});}
            var Q172;
            {var subQ0=sQuery(id+"F5.wireOp",EDGE,"E12.1.67.0");var subQ1=makeQuery(id+"F3.boolean.opBoolean","COPY",EDGE,{"derivedFrom":makeQuery(id+"F3.opExtrude","CAP_EDGE",EDGE,{"disambiguationData":[OSD([sQuery(id+"F2.wireOp",EDGE,"E6")])],"isStart":true})});var subQ2=makeQuery(id+"F5.imprint","INTERSECT",VERTEX,{"disambiguationData":[OD(0.0)],"derivedFrom":[subQ1,subQ0]});Q172=makeQuery(id+"F5.imprint","IMPRINT",FACE,{"disambiguationData":[TD([[makeQuery(id+"F5.imprint","IMPRINT",EDGE,{"disambiguationData":[TD([[subQ2,1.0]])],"derivedFrom":subQ0}),1.0]])]});}
            var Q173;
            {var subQ0=sQuery(id+"F5.wireOp",EDGE,"E12.1.104.0");var subQ1=makeQuery(id+"F3.boolean.opBoolean","COPY",EDGE,{"derivedFrom":makeQuery(id+"F3.opExtrude","CAP_EDGE",EDGE,{"disambiguationData":[OSD([sQuery(id+"F2.wireOp",EDGE,"E6")])],"isStart":true})});var subQ2=makeQuery(id+"F5.imprint","INTERSECT",VERTEX,{"disambiguationData":[OD(0.0)],"derivedFrom":[subQ1,subQ0]});Q173=makeQuery(id+"F5.imprint","IMPRINT",FACE,{"disambiguationData":[TD([[makeQuery(id+"F5.imprint","IMPRINT",EDGE,{"disambiguationData":[TD([[subQ2,1.0]])],"derivedFrom":subQ0}),1.0]])]});}
            var Q174;
            {var subQ0=sQuery(id+"F5.wireOp",EDGE,"E12.1.72.0");var subQ1=makeQuery(id+"F3.boolean.opBoolean","COPY",EDGE,{"derivedFrom":makeQuery(id+"F3.opExtrude","CAP_EDGE",EDGE,{"disambiguationData":[OSD([sQuery(id+"F2.wireOp",EDGE,"E6")])],"isStart":true})});var subQ2=makeQuery(id+"F5.imprint","INTERSECT",VERTEX,{"disambiguationData":[OD(0.0)],"derivedFrom":[subQ1,subQ0]});Q174=makeQuery(id+"F5.imprint","IMPRINT",FACE,{"disambiguationData":[TD([[makeQuery(id+"F5.imprint","IMPRINT",EDGE,{"disambiguationData":[TD([[subQ2,-1.0]])],"derivedFrom":subQ0}),1.0]])]});}
            var Q175;
            {var subQ0=sQuery(id+"F5.wireOp",EDGE,"E12.1.88.0");var subQ1=makeQuery(id+"F3.boolean.opBoolean","COPY",EDGE,{"derivedFrom":makeQuery(id+"F3.opExtrude","CAP_EDGE",EDGE,{"disambiguationData":[OSD([sQuery(id+"F2.wireOp",EDGE,"E6")])],"isStart":true})});var subQ2=makeQuery(id+"F5.imprint","INTERSECT",VERTEX,{"disambiguationData":[OD(0.0)],"derivedFrom":[subQ1,subQ0]});Q175=makeQuery(id+"F5.imprint","IMPRINT",FACE,{"disambiguationData":[TD([[makeQuery(id+"F5.imprint","IMPRINT",EDGE,{"disambiguationData":[TD([[subQ2,-1.0]])],"derivedFrom":subQ0}),1.0]])]});}
            var Q176;
            {var subQ0=sQuery(id+"F5.wireOp",EDGE,"E12.1.68.0");var subQ1=makeQuery(id+"F3.boolean.opBoolean","COPY",EDGE,{"derivedFrom":makeQuery(id+"F3.opExtrude","CAP_EDGE",EDGE,{"disambiguationData":[OSD([sQuery(id+"F2.wireOp",EDGE,"E6")])],"isStart":true})});var subQ2=makeQuery(id+"F5.imprint","INTERSECT",VERTEX,{"disambiguationData":[OD(0.0)],"derivedFrom":[subQ1,subQ0]});Q176=makeQuery(id+"F5.imprint","IMPRINT",FACE,{"disambiguationData":[TD([[makeQuery(id+"F5.imprint","IMPRINT",EDGE,{"disambiguationData":[TD([[subQ2,1.0]])],"derivedFrom":subQ0}),1.0]])]});}
            var Q177;
            {var subQ0=sQuery(id+"F5.wireOp",EDGE,"E12.1.85.0");var subQ1=makeQuery(id+"F3.boolean.opBoolean","COPY",EDGE,{"derivedFrom":makeQuery(id+"F3.opExtrude","CAP_EDGE",EDGE,{"disambiguationData":[OSD([sQuery(id+"F2.wireOp",EDGE,"E6")])],"isStart":true})});var subQ2=makeQuery(id+"F5.imprint","INTERSECT",VERTEX,{"disambiguationData":[OD(0.0)],"derivedFrom":[subQ1,subQ0]});Q177=makeQuery(id+"F5.imprint","IMPRINT",FACE,{"disambiguationData":[TD([[makeQuery(id+"F5.imprint","IMPRINT",EDGE,{"disambiguationData":[TD([[subQ2,1.0]])],"derivedFrom":subQ0}),1.0]])]});}
            var Q178;
            {var subQ0=sQuery(id+"F5.wireOp",EDGE,"E12.1.69.0");var subQ1=makeQuery(id+"F3.boolean.opBoolean","COPY",EDGE,{"derivedFrom":makeQuery(id+"F3.opExtrude","CAP_EDGE",EDGE,{"disambiguationData":[OSD([sQuery(id+"F2.wireOp",EDGE,"E6")])],"isStart":true})});var subQ2=makeQuery(id+"F5.imprint","INTERSECT",VERTEX,{"disambiguationData":[OD(0.0)],"derivedFrom":[subQ1,subQ0]});Q178=makeQuery(id+"F5.imprint","IMPRINT",FACE,{"disambiguationData":[TD([[makeQuery(id+"F5.imprint","IMPRINT",EDGE,{"disambiguationData":[TD([[subQ2,1.0]])],"derivedFrom":subQ0}),1.0]])]});}
            var Q179;
            {var subQ0=sQuery(id+"F5.wireOp",EDGE,"E12.1.105.0");var subQ1=makeQuery(id+"F3.boolean.opBoolean","COPY",EDGE,{"derivedFrom":makeQuery(id+"F3.opExtrude","CAP_EDGE",EDGE,{"disambiguationData":[OSD([sQuery(id+"F2.wireOp",EDGE,"E6")])],"isStart":true})});var subQ2=makeQuery(id+"F5.imprint","INTERSECT",VERTEX,{"disambiguationData":[OD(0.0)],"derivedFrom":[subQ1,subQ0]});Q179=makeQuery(id+"F5.imprint","IMPRINT",FACE,{"disambiguationData":[TD([[makeQuery(id+"F5.imprint","IMPRINT",EDGE,{"disambiguationData":[TD([[subQ2,1.0]])],"derivedFrom":subQ0}),1.0]])]});}
            var Q180;
            {var subQ0=sQuery(id+"F5.wireOp",EDGE,"E12.1.89.0");var subQ1=makeQuery(id+"F3.boolean.opBoolean","COPY",EDGE,{"derivedFrom":makeQuery(id+"F3.opExtrude","CAP_EDGE",EDGE,{"disambiguationData":[OSD([sQuery(id+"F2.wireOp",EDGE,"E6")])],"isStart":true})});var subQ2=makeQuery(id+"F5.imprint","INTERSECT",VERTEX,{"disambiguationData":[OD(0.0)],"derivedFrom":[subQ1,subQ0]});Q180=makeQuery(id+"F5.imprint","IMPRINT",FACE,{"disambiguationData":[TD([[makeQuery(id+"F5.imprint","IMPRINT",EDGE,{"disambiguationData":[TD([[subQ2,-1.0]])],"derivedFrom":subQ0}),1.0]])]});}
            var Q181;
            {var subQ0=sQuery(id+"F5.wireOp",EDGE,"E12.1.73.0");var subQ1=makeQuery(id+"F3.boolean.opBoolean","COPY",EDGE,{"derivedFrom":makeQuery(id+"F3.opExtrude","CAP_EDGE",EDGE,{"disambiguationData":[OSD([sQuery(id+"F2.wireOp",EDGE,"E6")])],"isStart":true})});var subQ2=makeQuery(id+"F5.imprint","INTERSECT",VERTEX,{"disambiguationData":[OD(0.0)],"derivedFrom":[subQ1,subQ0]});Q181=makeQuery(id+"F5.imprint","IMPRINT",FACE,{"disambiguationData":[TD([[makeQuery(id+"F5.imprint","IMPRINT",EDGE,{"disambiguationData":[TD([[subQ2,-1.0]])],"derivedFrom":subQ0}),1.0]])]});}
            var Q182;
            {var subQ0=sQuery(id+"F5.wireOp",EDGE,"E12.1.86.0");var subQ1=makeQuery(id+"F3.boolean.opBoolean","COPY",EDGE,{"derivedFrom":makeQuery(id+"F3.opExtrude","CAP_EDGE",EDGE,{"disambiguationData":[OSD([sQuery(id+"F2.wireOp",EDGE,"E6")])],"isStart":true})});var subQ2=makeQuery(id+"F5.imprint","INTERSECT",VERTEX,{"disambiguationData":[OD(0.0)],"derivedFrom":[subQ1,subQ0]});Q182=makeQuery(id+"F5.imprint","IMPRINT",FACE,{"disambiguationData":[TD([[makeQuery(id+"F5.imprint","IMPRINT",EDGE,{"disambiguationData":[TD([[subQ2,1.0]])],"derivedFrom":subQ0}),1.0]])]});}
            var Q183;
            {var subQ0=sQuery(id+"F5.wireOp",EDGE,"E12.1.70.0");var subQ1=makeQuery(id+"F3.boolean.opBoolean","COPY",EDGE,{"derivedFrom":makeQuery(id+"F3.opExtrude","CAP_EDGE",EDGE,{"disambiguationData":[OSD([sQuery(id+"F2.wireOp",EDGE,"E6")])],"isStart":true})});var subQ2=makeQuery(id+"F5.imprint","INTERSECT",VERTEX,{"disambiguationData":[OD(0.0)],"derivedFrom":[subQ1,subQ0]});Q183=makeQuery(id+"F5.imprint","IMPRINT",FACE,{"disambiguationData":[TD([[makeQuery(id+"F5.imprint","IMPRINT",EDGE,{"disambiguationData":[TD([[subQ2,1.0]])],"derivedFrom":subQ0}),1.0]])]});}
            var Q184;
            {var subQ0=sQuery(id+"F5.wireOp",EDGE,"E12.1.106.0");var subQ1=makeQuery(id+"F3.boolean.opBoolean","COPY",EDGE,{"derivedFrom":makeQuery(id+"F3.opExtrude","CAP_EDGE",EDGE,{"disambiguationData":[OSD([sQuery(id+"F2.wireOp",EDGE,"E6")])],"isStart":true})});var subQ2=makeQuery(id+"F5.imprint","INTERSECT",VERTEX,{"disambiguationData":[OD(0.0)],"derivedFrom":[subQ1,subQ0]});Q184=makeQuery(id+"F5.imprint","IMPRINT",FACE,{"disambiguationData":[TD([[makeQuery(id+"F5.imprint","IMPRINT",EDGE,{"disambiguationData":[TD([[subQ2,1.0]])],"derivedFrom":subQ0}),1.0]])]});}
            var Q185;
            {var subQ0=sQuery(id+"F5.wireOp",EDGE,"E12.1.90.0");var subQ1=makeQuery(id+"F3.boolean.opBoolean","COPY",EDGE,{"derivedFrom":makeQuery(id+"F3.opExtrude","CAP_EDGE",EDGE,{"disambiguationData":[OSD([sQuery(id+"F2.wireOp",EDGE,"E6")])],"isStart":true})});var subQ2=makeQuery(id+"F5.imprint","INTERSECT",VERTEX,{"disambiguationData":[OD(0.0)],"derivedFrom":[subQ1,subQ0]});Q185=makeQuery(id+"F5.imprint","IMPRINT",FACE,{"disambiguationData":[TD([[makeQuery(id+"F5.imprint","IMPRINT",EDGE,{"disambiguationData":[TD([[subQ2,-1.0]])],"derivedFrom":subQ0}),1.0]])]});}
            var Q186;
            {var subQ0=sQuery(id+"F5.wireOp",EDGE,"E12.1.74.0");var subQ1=makeQuery(id+"F3.boolean.opBoolean","COPY",EDGE,{"derivedFrom":makeQuery(id+"F3.opExtrude","CAP_EDGE",EDGE,{"disambiguationData":[OSD([sQuery(id+"F2.wireOp",EDGE,"E6")])],"isStart":true})});var subQ2=makeQuery(id+"F5.imprint","INTERSECT",VERTEX,{"disambiguationData":[OD(0.0)],"derivedFrom":[subQ1,subQ0]});Q186=makeQuery(id+"F5.imprint","IMPRINT",FACE,{"disambiguationData":[TD([[makeQuery(id+"F5.imprint","IMPRINT",EDGE,{"disambiguationData":[TD([[subQ2,-1.0]])],"derivedFrom":subQ0}),1.0]])]});}
            var Q187;
            {var subQ0=sQuery(id+"F5.wireOp",EDGE,"E12.1.107.0");var subQ1=makeQuery(id+"F3.boolean.opBoolean","COPY",EDGE,{"derivedFrom":makeQuery(id+"F3.opExtrude","CAP_EDGE",EDGE,{"disambiguationData":[OSD([sQuery(id+"F2.wireOp",EDGE,"E6")])],"isStart":true})});var subQ2=makeQuery(id+"F5.imprint","INTERSECT",VERTEX,{"disambiguationData":[OD(0.0)],"derivedFrom":[subQ1,subQ0]});Q187=makeQuery(id+"F5.imprint","IMPRINT",FACE,{"disambiguationData":[TD([[makeQuery(id+"F5.imprint","IMPRINT",EDGE,{"disambiguationData":[TD([[subQ2,1.0]])],"derivedFrom":subQ0}),1.0]])]});}
            var Q188;
            {var subQ0=sQuery(id+"F5.wireOp",EDGE,"E12.1.75.0");var subQ1=makeQuery(id+"F3.boolean.opBoolean","COPY",EDGE,{"derivedFrom":makeQuery(id+"F3.opExtrude","CAP_EDGE",EDGE,{"disambiguationData":[OSD([sQuery(id+"F2.wireOp",EDGE,"E6")])],"isStart":true})});var subQ2=makeQuery(id+"F5.imprint","INTERSECT",VERTEX,{"disambiguationData":[OD(0.0)],"derivedFrom":[subQ1,subQ0]});Q188=makeQuery(id+"F5.imprint","IMPRINT",FACE,{"disambiguationData":[TD([[makeQuery(id+"F5.imprint","IMPRINT",EDGE,{"disambiguationData":[TD([[subQ2,-1.0]])],"derivedFrom":subQ0}),1.0]])]});}
            var Q189;
            {var subQ0=sQuery(id+"F5.wireOp",EDGE,"E12.1.91.0");var subQ1=makeQuery(id+"F3.boolean.opBoolean","COPY",EDGE,{"derivedFrom":makeQuery(id+"F3.opExtrude","CAP_EDGE",EDGE,{"disambiguationData":[OSD([sQuery(id+"F2.wireOp",EDGE,"E6")])],"isStart":true})});var subQ2=makeQuery(id+"F5.imprint","INTERSECT",VERTEX,{"disambiguationData":[OD(0.0)],"derivedFrom":[subQ1,subQ0]});Q189=makeQuery(id+"F5.imprint","IMPRINT",FACE,{"disambiguationData":[TD([[makeQuery(id+"F5.imprint","IMPRINT",EDGE,{"disambiguationData":[TD([[subQ2,-1.0]])],"derivedFrom":subQ0}),1.0]])]});}
            var Q190;
            {var subQ0=sQuery(id+"F5.wireOp",EDGE,"E12.1.75.0");var subQ1=makeQuery(id+"F3.boolean.opBoolean","COPY",EDGE,{"derivedFrom":makeQuery(id+"F3.opExtrude","CAP_EDGE",EDGE,{"disambiguationData":[OSD([sQuery(id+"F2.wireOp",EDGE,"E6")])],"isStart":true})});var subQ2=makeQuery(id+"F5.imprint","INTERSECT",VERTEX,{"disambiguationData":[OD(0.0)],"derivedFrom":[subQ1,subQ0]});Q190=makeQuery(id+"F5.imprint","IMPRINT",FACE,{"disambiguationData":[TD([[makeQuery(id+"F5.imprint","IMPRINT",EDGE,{"disambiguationData":[TD([[subQ2,1.0]])],"derivedFrom":subQ0}),1.0]])]});}
            var Q191;
            {var subQ0=sQuery(id+"F5.wireOp",EDGE,"E12.1.103.0");var subQ1=makeQuery(id+"F3.boolean.opBoolean","COPY",EDGE,{"derivedFrom":makeQuery(id+"F3.opExtrude","CAP_EDGE",EDGE,{"disambiguationData":[OSD([sQuery(id+"F2.wireOp",EDGE,"E6")])],"isStart":true})});var subQ2=makeQuery(id+"F5.imprint","INTERSECT",VERTEX,{"disambiguationData":[OD(0.0)],"derivedFrom":[subQ1,subQ0]});Q191=makeQuery(id+"F5.imprint","IMPRINT",FACE,{"disambiguationData":[TD([[makeQuery(id+"F5.imprint","IMPRINT",EDGE,{"disambiguationData":[TD([[subQ2,-1.0]])],"derivedFrom":subQ0}),1.0]])]});}
            var Q192;
            {var subQ0=sQuery(id+"F5.wireOp",EDGE,"E12.1.87.0");var subQ1=makeQuery(id+"F3.boolean.opBoolean","COPY",EDGE,{"derivedFrom":makeQuery(id+"F3.opExtrude","CAP_EDGE",EDGE,{"disambiguationData":[OSD([sQuery(id+"F2.wireOp",EDGE,"E6")])],"isStart":true})});var subQ2=makeQuery(id+"F5.imprint","INTERSECT",VERTEX,{"disambiguationData":[OD(0.0)],"derivedFrom":[subQ1,subQ0]});Q192=makeQuery(id+"F5.imprint","IMPRINT",FACE,{"disambiguationData":[TD([[makeQuery(id+"F5.imprint","IMPRINT",EDGE,{"disambiguationData":[TD([[subQ2,1.0]])],"derivedFrom":subQ0}),1.0]])]});}
            var Q193;
            {var subQ0=sQuery(id+"F5.wireOp",EDGE,"E12.1.107.0");var subQ1=makeQuery(id+"F3.boolean.opBoolean","COPY",EDGE,{"derivedFrom":makeQuery(id+"F3.opExtrude","CAP_EDGE",EDGE,{"disambiguationData":[OSD([sQuery(id+"F2.wireOp",EDGE,"E6")])],"isStart":true})});var subQ2=makeQuery(id+"F5.imprint","INTERSECT",VERTEX,{"disambiguationData":[OD(0.0)],"derivedFrom":[subQ1,subQ0]});Q193=makeQuery(id+"F5.imprint","IMPRINT",FACE,{"disambiguationData":[TD([[makeQuery(id+"F5.imprint","IMPRINT",EDGE,{"disambiguationData":[TD([[subQ2,-1.0]])],"derivedFrom":subQ0}),1.0]])]});}
            var Q194;
            {var subQ0=sQuery(id+"F5.wireOp",EDGE,"E12.1.108.0");var subQ1=makeQuery(id+"F3.boolean.opBoolean","COPY",EDGE,{"derivedFrom":makeQuery(id+"F3.opExtrude","CAP_EDGE",EDGE,{"disambiguationData":[OSD([sQuery(id+"F2.wireOp",EDGE,"E6")])],"isStart":true})});var subQ2=makeQuery(id+"F5.imprint","INTERSECT",VERTEX,{"disambiguationData":[OD(0.0)],"derivedFrom":[subQ1,subQ0]});Q194=makeQuery(id+"F5.imprint","IMPRINT",FACE,{"disambiguationData":[TD([[makeQuery(id+"F5.imprint","IMPRINT",EDGE,{"disambiguationData":[TD([[subQ2,1.0]])],"derivedFrom":subQ0}),1.0]])]});}
            var Q195;
            {var subQ0=sQuery(id+"F5.wireOp",EDGE,"E12.1.76.0");var subQ1=makeQuery(id+"F3.boolean.opBoolean","COPY",EDGE,{"derivedFrom":makeQuery(id+"F3.opExtrude","CAP_EDGE",EDGE,{"disambiguationData":[OSD([sQuery(id+"F2.wireOp",EDGE,"E6")])],"isStart":true})});var subQ2=makeQuery(id+"F5.imprint","INTERSECT",VERTEX,{"disambiguationData":[OD(0.0)],"derivedFrom":[subQ1,subQ0]});Q195=makeQuery(id+"F5.imprint","IMPRINT",FACE,{"disambiguationData":[TD([[makeQuery(id+"F5.imprint","IMPRINT",EDGE,{"disambiguationData":[TD([[subQ2,-1.0]])],"derivedFrom":subQ0}),1.0]])]});}
            var Q196;
            {var subQ0=sQuery(id+"F5.wireOp",EDGE,"E12.1.92.0");var subQ1=makeQuery(id+"F3.boolean.opBoolean","COPY",EDGE,{"derivedFrom":makeQuery(id+"F3.opExtrude","CAP_EDGE",EDGE,{"disambiguationData":[OSD([sQuery(id+"F2.wireOp",EDGE,"E6")])],"isStart":true})});var subQ2=makeQuery(id+"F5.imprint","INTERSECT",VERTEX,{"disambiguationData":[OD(0.0)],"derivedFrom":[subQ1,subQ0]});Q196=makeQuery(id+"F5.imprint","IMPRINT",FACE,{"disambiguationData":[TD([[makeQuery(id+"F5.imprint","IMPRINT",EDGE,{"disambiguationData":[TD([[subQ2,-1.0]])],"derivedFrom":subQ0}),1.0]])]});}
            var Q197;
            {var subQ0=sQuery(id+"F5.wireOp",EDGE,"E12.1.104.0");var subQ1=makeQuery(id+"F3.boolean.opBoolean","COPY",EDGE,{"derivedFrom":makeQuery(id+"F3.opExtrude","CAP_EDGE",EDGE,{"disambiguationData":[OSD([sQuery(id+"F2.wireOp",EDGE,"E6")])],"isStart":true})});var subQ2=makeQuery(id+"F5.imprint","INTERSECT",VERTEX,{"disambiguationData":[OD(0.0)],"derivedFrom":[subQ1,subQ0]});Q197=makeQuery(id+"F5.imprint","IMPRINT",FACE,{"disambiguationData":[TD([[makeQuery(id+"F5.imprint","IMPRINT",EDGE,{"disambiguationData":[TD([[subQ2,-1.0]])],"derivedFrom":subQ0}),1.0]])]});}
            var Q198;
            {var subQ0=sQuery(id+"F5.wireOp",EDGE,"E12.1.88.0");var subQ1=makeQuery(id+"F3.boolean.opBoolean","COPY",EDGE,{"derivedFrom":makeQuery(id+"F3.opExtrude","CAP_EDGE",EDGE,{"disambiguationData":[OSD([sQuery(id+"F2.wireOp",EDGE,"E6")])],"isStart":true})});var subQ2=makeQuery(id+"F5.imprint","INTERSECT",VERTEX,{"disambiguationData":[OD(0.0)],"derivedFrom":[subQ1,subQ0]});Q198=makeQuery(id+"F5.imprint","IMPRINT",FACE,{"disambiguationData":[TD([[makeQuery(id+"F5.imprint","IMPRINT",EDGE,{"disambiguationData":[TD([[subQ2,1.0]])],"derivedFrom":subQ0}),1.0]])]});}
            var Q199;
            {var subQ0=sQuery(id+"F5.wireOp",EDGE,"E12.1.72.0");var subQ1=makeQuery(id+"F3.boolean.opBoolean","COPY",EDGE,{"derivedFrom":makeQuery(id+"F3.opExtrude","CAP_EDGE",EDGE,{"disambiguationData":[OSD([sQuery(id+"F2.wireOp",EDGE,"E6")])],"isStart":true})});var subQ2=makeQuery(id+"F5.imprint","INTERSECT",VERTEX,{"disambiguationData":[OD(0.0)],"derivedFrom":[subQ1,subQ0]});Q199=makeQuery(id+"F5.imprint","IMPRINT",FACE,{"disambiguationData":[TD([[makeQuery(id+"F5.imprint","IMPRINT",EDGE,{"disambiguationData":[TD([[subQ2,1.0]])],"derivedFrom":subQ0}),1.0]])]});}
            var Q200;
            {var subQ0=sQuery(id+"F5.wireOp",EDGE,"E12.1.95.0");var subQ1=makeQuery(id+"F3.boolean.opBoolean","COPY",EDGE,{"derivedFrom":makeQuery(id+"F3.opExtrude","CAP_EDGE",EDGE,{"disambiguationData":[OSD([sQuery(id+"F2.wireOp",EDGE,"E6")])],"isStart":true})});var subQ2=makeQuery(id+"F5.imprint","INTERSECT",VERTEX,{"disambiguationData":[OD(0.0)],"derivedFrom":[subQ1,subQ0]});Q200=makeQuery(id+"F5.imprint","IMPRINT",FACE,{"disambiguationData":[TD([[makeQuery(id+"F5.imprint","IMPRINT",EDGE,{"disambiguationData":[TD([[subQ2,-1.0]])],"derivedFrom":subQ0}),1.0]])]});}
            var Q201;
            {var subQ0=sQuery(id+"F5.wireOp",EDGE,"E12.1.79.0");var subQ1=makeQuery(id+"F3.boolean.opBoolean","COPY",EDGE,{"derivedFrom":makeQuery(id+"F3.opExtrude","CAP_EDGE",EDGE,{"disambiguationData":[OSD([sQuery(id+"F2.wireOp",EDGE,"E6")])],"isStart":true})});var subQ2=makeQuery(id+"F5.imprint","INTERSECT",VERTEX,{"disambiguationData":[OD(0.0)],"derivedFrom":[subQ1,subQ0]});Q201=makeQuery(id+"F5.imprint","IMPRINT",FACE,{"disambiguationData":[TD([[makeQuery(id+"F5.imprint","IMPRINT",EDGE,{"disambiguationData":[TD([[subQ2,-1.0]])],"derivedFrom":subQ0}),1.0]])]});}
            var Q202;
            {var subQ0=sQuery(id+"F5.wireOp",EDGE,"E12.1.63.0");var subQ1=makeQuery(id+"F3.boolean.opBoolean","COPY",EDGE,{"derivedFrom":makeQuery(id+"F3.opExtrude","CAP_EDGE",EDGE,{"disambiguationData":[OSD([sQuery(id+"F2.wireOp",EDGE,"E6")])],"isStart":true})});var subQ2=makeQuery(id+"F5.imprint","INTERSECT",VERTEX,{"disambiguationData":[OD(0.0)],"derivedFrom":[subQ1,subQ0]});Q202=makeQuery(id+"F5.imprint","IMPRINT",FACE,{"disambiguationData":[TD([[makeQuery(id+"F5.imprint","IMPRINT",EDGE,{"disambiguationData":[TD([[subQ2,-1.0]])],"derivedFrom":subQ0}),1.0]])]});}
            var Q203;
            {var subQ0=sQuery(id+"F5.wireOp",EDGE,"E12.1.93.0");var subQ1=makeQuery(id+"F3.boolean.opBoolean","COPY",EDGE,{"derivedFrom":makeQuery(id+"F3.opExtrude","CAP_EDGE",EDGE,{"disambiguationData":[OSD([sQuery(id+"F2.wireOp",EDGE,"E6")])],"isStart":true})});var subQ2=makeQuery(id+"F5.imprint","INTERSECT",VERTEX,{"disambiguationData":[OD(0.0)],"derivedFrom":[subQ1,subQ0]});Q203=makeQuery(id+"F5.imprint","IMPRINT",FACE,{"disambiguationData":[TD([[makeQuery(id+"F5.imprint","IMPRINT",EDGE,{"disambiguationData":[TD([[subQ2,1.0]])],"derivedFrom":subQ0}),1.0]])]});}
            var Q204;
            {var subQ0=sQuery(id+"F5.wireOp",EDGE,"E12.1.82.0");var subQ1=makeQuery(id+"F3.boolean.opBoolean","COPY",EDGE,{"derivedFrom":makeQuery(id+"F3.opExtrude","CAP_EDGE",EDGE,{"disambiguationData":[OSD([sQuery(id+"F2.wireOp",EDGE,"E6")])],"isStart":true})});var subQ2=makeQuery(id+"F5.imprint","INTERSECT",VERTEX,{"disambiguationData":[OD(0.0)],"derivedFrom":[subQ1,subQ0]});Q204=makeQuery(id+"F5.imprint","IMPRINT",FACE,{"disambiguationData":[TD([[makeQuery(id+"F5.imprint","IMPRINT",EDGE,{"disambiguationData":[TD([[subQ2,-1.0]])],"derivedFrom":subQ0}),1.0]])]});}
            var Q205;
            {var subQ0=sQuery(id+"F5.wireOp",EDGE,"E12.1.81.0");var subQ1=makeQuery(id+"F3.boolean.opBoolean","COPY",EDGE,{"derivedFrom":makeQuery(id+"F3.opExtrude","CAP_EDGE",EDGE,{"disambiguationData":[OSD([sQuery(id+"F2.wireOp",EDGE,"E6")])],"isStart":true})});var subQ2=makeQuery(id+"F5.imprint","INTERSECT",VERTEX,{"disambiguationData":[OD(0.0)],"derivedFrom":[subQ1,subQ0]});Q205=makeQuery(id+"F5.imprint","IMPRINT",FACE,{"disambiguationData":[TD([[makeQuery(id+"F5.imprint","IMPRINT",EDGE,{"disambiguationData":[TD([[subQ2,-1.0]])],"derivedFrom":subQ0}),1.0]])]});}
            var Q206;
            {var subQ0=sQuery(id+"F5.wireOp",EDGE,"E12.1.80.0");var subQ1=makeQuery(id+"F3.boolean.opBoolean","COPY",EDGE,{"derivedFrom":makeQuery(id+"F3.opExtrude","CAP_EDGE",EDGE,{"disambiguationData":[OSD([sQuery(id+"F2.wireOp",EDGE,"E6")])],"isStart":true})});var subQ2=makeQuery(id+"F5.imprint","INTERSECT",VERTEX,{"disambiguationData":[OD(0.0)],"derivedFrom":[subQ1,subQ0]});Q206=makeQuery(id+"F5.imprint","IMPRINT",FACE,{"disambiguationData":[TD([[makeQuery(id+"F5.imprint","IMPRINT",EDGE,{"disambiguationData":[TD([[subQ2,-1.0]])],"derivedFrom":subQ0}),1.0]])]});}
            var Q207;
            {var subQ0=sQuery(id+"F5.wireOp",EDGE,"E12.1.83.0");var subQ1=makeQuery(id+"F3.boolean.opBoolean","COPY",EDGE,{"derivedFrom":makeQuery(id+"F3.opExtrude","CAP_EDGE",EDGE,{"disambiguationData":[OSD([sQuery(id+"F2.wireOp",EDGE,"E6")])],"isStart":true})});var subQ2=makeQuery(id+"F5.imprint","INTERSECT",VERTEX,{"disambiguationData":[OD(0.0)],"derivedFrom":[subQ1,subQ0]});Q207=makeQuery(id+"F5.imprint","IMPRINT",FACE,{"disambiguationData":[TD([[makeQuery(id+"F5.imprint","IMPRINT",EDGE,{"disambiguationData":[TD([[subQ2,-1.0]])],"derivedFrom":subQ0}),1.0]])]});}
            var Q208;
            {var subQ0=sQuery(id+"F5.wireOp",EDGE,"E12.1.84.0");var subQ1=makeQuery(id+"F3.boolean.opBoolean","COPY",EDGE,{"derivedFrom":makeQuery(id+"F3.opExtrude","CAP_EDGE",EDGE,{"disambiguationData":[OSD([sQuery(id+"F2.wireOp",EDGE,"E6")])],"isStart":true})});var subQ2=makeQuery(id+"F5.imprint","INTERSECT",VERTEX,{"disambiguationData":[OD(0.0)],"derivedFrom":[subQ1,subQ0]});Q208=makeQuery(id+"F5.imprint","IMPRINT",FACE,{"disambiguationData":[TD([[makeQuery(id+"F5.imprint","IMPRINT",EDGE,{"disambiguationData":[TD([[subQ2,-1.0]])],"derivedFrom":subQ0}),1.0]])]});}
            var Q209;
            {var subQ0=sQuery(id+"F5.wireOp",EDGE,"E12.1.100.0");var subQ1=makeQuery(id+"F3.boolean.opBoolean","COPY",EDGE,{"derivedFrom":makeQuery(id+"F3.opExtrude","CAP_EDGE",EDGE,{"disambiguationData":[OSD([sQuery(id+"F2.wireOp",EDGE,"E6")])],"isStart":true})});var subQ2=makeQuery(id+"F5.imprint","INTERSECT",VERTEX,{"disambiguationData":[OD(0.0)],"derivedFrom":[subQ1,subQ0]});Q209=makeQuery(id+"F5.imprint","IMPRINT",FACE,{"disambiguationData":[TD([[makeQuery(id+"F5.imprint","IMPRINT",EDGE,{"disambiguationData":[TD([[subQ2,1.0]])],"derivedFrom":subQ0}),1.0]])]});}
            var Q210;
            {var subQ0=sQuery(id+"F5.wireOp",EDGE,"E12.1.101.0");var subQ1=makeQuery(id+"F3.boolean.opBoolean","COPY",EDGE,{"derivedFrom":makeQuery(id+"F3.opExtrude","CAP_EDGE",EDGE,{"disambiguationData":[OSD([sQuery(id+"F2.wireOp",EDGE,"E6")])],"isStart":true})});var subQ2=makeQuery(id+"F5.imprint","INTERSECT",VERTEX,{"disambiguationData":[OD(0.0)],"derivedFrom":[subQ1,subQ0]});Q210=makeQuery(id+"F5.imprint","IMPRINT",FACE,{"disambiguationData":[TD([[makeQuery(id+"F5.imprint","IMPRINT",EDGE,{"disambiguationData":[TD([[subQ2,1.0]])],"derivedFrom":subQ0}),1.0]])]});}
            var Q211;
            {var subQ0=sQuery(id+"F5.wireOp",EDGE,"E12.1.65.0");var subQ1=makeQuery(id+"F3.boolean.opBoolean","COPY",EDGE,{"derivedFrom":makeQuery(id+"F3.opExtrude","CAP_EDGE",EDGE,{"disambiguationData":[OSD([sQuery(id+"F2.wireOp",EDGE,"E6")])],"isStart":true})});var subQ2=makeQuery(id+"F5.imprint","INTERSECT",VERTEX,{"disambiguationData":[OD(0.0)],"derivedFrom":[subQ1,subQ0]});Q211=makeQuery(id+"F5.imprint","IMPRINT",FACE,{"disambiguationData":[TD([[makeQuery(id+"F5.imprint","IMPRINT",EDGE,{"disambiguationData":[TD([[subQ2,1.0]])],"derivedFrom":subQ0}),1.0]])]});}
            var Q212;
            {var subQ0=sQuery(id+"F5.wireOp",EDGE,"E12.1.83.0");var subQ1=makeQuery(id+"F3.boolean.opBoolean","COPY",EDGE,{"derivedFrom":makeQuery(id+"F3.opExtrude","CAP_EDGE",EDGE,{"disambiguationData":[OSD([sQuery(id+"F2.wireOp",EDGE,"E6")])],"isStart":true})});var subQ2=makeQuery(id+"F5.imprint","INTERSECT",VERTEX,{"disambiguationData":[OD(0.0)],"derivedFrom":[subQ1,subQ0]});Q212=makeQuery(id+"F5.imprint","IMPRINT",FACE,{"disambiguationData":[TD([[makeQuery(id+"F5.imprint","IMPRINT",EDGE,{"disambiguationData":[TD([[subQ2,1.0]])],"derivedFrom":subQ0}),1.0]])]});}
            var Q213;
            {var subQ0=sQuery(id+"F5.wireOp",EDGE,"E12.1.100.0");var subQ1=makeQuery(id+"F3.boolean.opBoolean","COPY",EDGE,{"derivedFrom":makeQuery(id+"F3.opExtrude","CAP_EDGE",EDGE,{"disambiguationData":[OSD([sQuery(id+"F2.wireOp",EDGE,"E6")])],"isStart":true})});var subQ2=makeQuery(id+"F5.imprint","INTERSECT",VERTEX,{"disambiguationData":[OD(0.0)],"derivedFrom":[subQ1,subQ0]});Q213=makeQuery(id+"F5.imprint","IMPRINT",FACE,{"disambiguationData":[TD([[makeQuery(id+"F5.imprint","IMPRINT",EDGE,{"disambiguationData":[TD([[subQ2,-1.0]])],"derivedFrom":subQ0}),1.0]])]});}
            var Q214;
            {var subQ0=sQuery(id+"F5.wireOp",EDGE,"E12.1.84.0");var subQ1=makeQuery(id+"F3.boolean.opBoolean","COPY",EDGE,{"derivedFrom":makeQuery(id+"F3.opExtrude","CAP_EDGE",EDGE,{"disambiguationData":[OSD([sQuery(id+"F2.wireOp",EDGE,"E6")])],"isStart":true})});var subQ2=makeQuery(id+"F5.imprint","INTERSECT",VERTEX,{"disambiguationData":[OD(0.0)],"derivedFrom":[subQ1,subQ0]});Q214=makeQuery(id+"F5.imprint","IMPRINT",FACE,{"disambiguationData":[TD([[makeQuery(id+"F5.imprint","IMPRINT",EDGE,{"disambiguationData":[TD([[subQ2,1.0]])],"derivedFrom":subQ0}),1.0]])]});}
            var Q215;
            {var subQ0=sQuery(id+"F5.wireOp",EDGE,"E12.1.101.0");var subQ1=makeQuery(id+"F3.boolean.opBoolean","COPY",EDGE,{"derivedFrom":makeQuery(id+"F3.opExtrude","CAP_EDGE",EDGE,{"disambiguationData":[OSD([sQuery(id+"F2.wireOp",EDGE,"E6")])],"isStart":true})});var subQ2=makeQuery(id+"F5.imprint","INTERSECT",VERTEX,{"disambiguationData":[OD(0.0)],"derivedFrom":[subQ1,subQ0]});Q215=makeQuery(id+"F5.imprint","IMPRINT",FACE,{"disambiguationData":[TD([[makeQuery(id+"F5.imprint","IMPRINT",EDGE,{"disambiguationData":[TD([[subQ2,-1.0]])],"derivedFrom":subQ0}),1.0]])]});}
            var Q216;
            {var subQ0=sQuery(id+"F5.wireOp",EDGE,"E12.1.102.0");var subQ1=makeQuery(id+"F3.boolean.opBoolean","COPY",EDGE,{"derivedFrom":makeQuery(id+"F3.opExtrude","CAP_EDGE",EDGE,{"disambiguationData":[OSD([sQuery(id+"F2.wireOp",EDGE,"E6")])],"isStart":true})});var subQ2=makeQuery(id+"F5.imprint","INTERSECT",VERTEX,{"disambiguationData":[OD(0.0)],"derivedFrom":[subQ1,subQ0]});Q216=makeQuery(id+"F5.imprint","IMPRINT",FACE,{"disambiguationData":[TD([[makeQuery(id+"F5.imprint","IMPRINT",EDGE,{"disambiguationData":[TD([[subQ2,-1.0]])],"derivedFrom":subQ0}),1.0]])]});}
            var Q217;
            {var subQ0=sQuery(id+"F5.wireOp",EDGE,"E12.1.71.0");var subQ1=makeQuery(id+"F3.boolean.opBoolean","COPY",EDGE,{"derivedFrom":makeQuery(id+"F3.opExtrude","CAP_EDGE",EDGE,{"disambiguationData":[OSD([sQuery(id+"F2.wireOp",EDGE,"E6")])],"isStart":true})});var subQ2=makeQuery(id+"F5.imprint","INTERSECT",VERTEX,{"disambiguationData":[OD(0.0)],"derivedFrom":[subQ1,subQ0]});Q217=makeQuery(id+"F5.imprint","IMPRINT",FACE,{"disambiguationData":[TD([[makeQuery(id+"F5.imprint","IMPRINT",EDGE,{"disambiguationData":[TD([[subQ2,1.0]])],"derivedFrom":subQ0}),1.0]])]});}
            var Q218;
            {var subQ0=sQuery(id+"F5.wireOp",EDGE,"E12.1.91.0");var subQ1=makeQuery(id+"F3.boolean.opBoolean","COPY",EDGE,{"derivedFrom":makeQuery(id+"F3.opExtrude","CAP_EDGE",EDGE,{"disambiguationData":[OSD([sQuery(id+"F2.wireOp",EDGE,"E6")])],"isStart":true})});var subQ2=makeQuery(id+"F5.imprint","INTERSECT",VERTEX,{"disambiguationData":[OD(0.0)],"derivedFrom":[subQ1,subQ0]});Q218=makeQuery(id+"F5.imprint","IMPRINT",FACE,{"disambiguationData":[TD([[makeQuery(id+"F5.imprint","IMPRINT",EDGE,{"disambiguationData":[TD([[subQ2,1.0]])],"derivedFrom":subQ0}),1.0]])]});}
            var Q219;
            {var subQ0=sQuery(id+"F5.wireOp",EDGE,"E12.1.80.0");var subQ1=makeQuery(id+"F3.boolean.opBoolean","COPY",EDGE,{"derivedFrom":makeQuery(id+"F3.opExtrude","CAP_EDGE",EDGE,{"disambiguationData":[OSD([sQuery(id+"F2.wireOp",EDGE,"E6")])],"isStart":true})});var subQ2=makeQuery(id+"F5.imprint","INTERSECT",VERTEX,{"disambiguationData":[OD(0.0)],"derivedFrom":[subQ1,subQ0]});Q219=makeQuery(id+"F5.imprint","IMPRINT",FACE,{"disambiguationData":[TD([[makeQuery(id+"F5.imprint","IMPRINT",EDGE,{"disambiguationData":[TD([[subQ2,1.0]])],"derivedFrom":subQ0}),1.0]])]});}
            var Q220;
            {var subQ0=sQuery(id+"F5.wireOp",EDGE,"E12.1.81.0");var subQ1=makeQuery(id+"F3.boolean.opBoolean","COPY",EDGE,{"derivedFrom":makeQuery(id+"F3.opExtrude","CAP_EDGE",EDGE,{"disambiguationData":[OSD([sQuery(id+"F2.wireOp",EDGE,"E6")])],"isStart":true})});var subQ2=makeQuery(id+"F5.imprint","INTERSECT",VERTEX,{"disambiguationData":[OD(0.0)],"derivedFrom":[subQ1,subQ0]});Q220=makeQuery(id+"F5.imprint","IMPRINT",FACE,{"disambiguationData":[TD([[makeQuery(id+"F5.imprint","IMPRINT",EDGE,{"disambiguationData":[TD([[subQ2,1.0]])],"derivedFrom":subQ0}),1.0]])]});}
            var Q221;
            {var subQ0=sQuery(id+"F5.wireOp",EDGE,"E12.1.82.0");var subQ1=makeQuery(id+"F3.boolean.opBoolean","COPY",EDGE,{"derivedFrom":makeQuery(id+"F3.opExtrude","CAP_EDGE",EDGE,{"disambiguationData":[OSD([sQuery(id+"F2.wireOp",EDGE,"E6")])],"isStart":true})});var subQ2=makeQuery(id+"F5.imprint","INTERSECT",VERTEX,{"disambiguationData":[OD(0.0)],"derivedFrom":[subQ1,subQ0]});Q221=makeQuery(id+"F5.imprint","IMPRINT",FACE,{"disambiguationData":[TD([[makeQuery(id+"F5.imprint","IMPRINT",EDGE,{"disambiguationData":[TD([[subQ2,1.0]])],"derivedFrom":subQ0}),1.0]])]});}
            var Q222;
            {var subQ0=sQuery(id+"F5.wireOp",EDGE,"E12.1.146.0");var subQ1=makeQuery(id+"F3.boolean.opBoolean","COPY",EDGE,{"derivedFrom":makeQuery(id+"F3.opExtrude","CAP_EDGE",EDGE,{"disambiguationData":[OSD([sQuery(id+"F2.wireOp",EDGE,"E6")])],"isStart":true})});var subQ2=makeQuery(id+"F5.imprint","INTERSECT",VERTEX,{"disambiguationData":[OD(0.0)],"derivedFrom":[subQ1,subQ0]});Q222=makeQuery(id+"F5.imprint","IMPRINT",FACE,{"disambiguationData":[TD([[makeQuery(id+"F5.imprint","IMPRINT",EDGE,{"disambiguationData":[TD([[subQ2,1.0]])],"derivedFrom":subQ0}),1.0]])]});}
            var Q223;
            {var subQ0=sQuery(id+"F5.wireOp",EDGE,"E12.1.130.0");var subQ1=makeQuery(id+"F3.boolean.opBoolean","COPY",EDGE,{"derivedFrom":makeQuery(id+"F3.opExtrude","CAP_EDGE",EDGE,{"disambiguationData":[OSD([sQuery(id+"F2.wireOp",EDGE,"E6")])],"isStart":true})});var subQ2=makeQuery(id+"F5.imprint","INTERSECT",VERTEX,{"disambiguationData":[OD(0.0)],"derivedFrom":[subQ1,subQ0]});Q223=makeQuery(id+"F5.imprint","IMPRINT",FACE,{"disambiguationData":[TD([[makeQuery(id+"F5.imprint","IMPRINT",EDGE,{"disambiguationData":[TD([[subQ2,1.0]])],"derivedFrom":subQ0}),1.0]])]});}
            var Q224;
            {var subQ0=sQuery(id+"F5.wireOp",EDGE,"E12.1.124.0");var subQ1=makeQuery(id+"F3.boolean.opBoolean","COPY",EDGE,{"derivedFrom":makeQuery(id+"F3.opExtrude","CAP_EDGE",EDGE,{"disambiguationData":[OSD([sQuery(id+"F2.wireOp",EDGE,"E6")])],"isStart":true})});var subQ2=makeQuery(id+"F5.imprint","INTERSECT",VERTEX,{"disambiguationData":[OD(0.0)],"derivedFrom":[subQ1,subQ0]});Q224=makeQuery(id+"F5.imprint","IMPRINT",FACE,{"disambiguationData":[TD([[makeQuery(id+"F5.imprint","IMPRINT",EDGE,{"disambiguationData":[TD([[subQ2,-1.0]])],"derivedFrom":subQ0}),1.0]])]});}
            var Q225;
            {var subQ0=sQuery(id+"F5.wireOp",EDGE,"E12.1.128.0");var subQ1=makeQuery(id+"F3.boolean.opBoolean","COPY",EDGE,{"derivedFrom":makeQuery(id+"F3.opExtrude","CAP_EDGE",EDGE,{"disambiguationData":[OSD([sQuery(id+"F2.wireOp",EDGE,"E6")])],"isStart":true})});var subQ2=makeQuery(id+"F5.imprint","INTERSECT",VERTEX,{"disambiguationData":[OD(0.0)],"derivedFrom":[subQ1,subQ0]});Q225=makeQuery(id+"F5.imprint","IMPRINT",FACE,{"disambiguationData":[TD([[makeQuery(id+"F5.imprint","IMPRINT",EDGE,{"disambiguationData":[TD([[subQ2,1.0]])],"derivedFrom":subQ0}),1.0]])]});}
            var Q226;
            {var subQ0=sQuery(id+"F5.wireOp",EDGE,"E12.1.131.0");var subQ1=makeQuery(id+"F3.boolean.opBoolean","COPY",EDGE,{"derivedFrom":makeQuery(id+"F3.opExtrude","CAP_EDGE",EDGE,{"disambiguationData":[OSD([sQuery(id+"F2.wireOp",EDGE,"E6")])],"isStart":true})});var subQ2=makeQuery(id+"F5.imprint","INTERSECT",VERTEX,{"disambiguationData":[OD(0.0)],"derivedFrom":[subQ1,subQ0]});Q226=makeQuery(id+"F5.imprint","IMPRINT",FACE,{"disambiguationData":[TD([[makeQuery(id+"F5.imprint","IMPRINT",EDGE,{"disambiguationData":[TD([[subQ2,1.0]])],"derivedFrom":subQ0}),1.0]])]});}
            var Q227;
            {var subQ0=sQuery(id+"F5.wireOp",EDGE,"E12.1.142.0");var subQ1=makeQuery(id+"F3.boolean.opBoolean","COPY",EDGE,{"derivedFrom":makeQuery(id+"F3.opExtrude","CAP_EDGE",EDGE,{"disambiguationData":[OSD([sQuery(id+"F2.wireOp",EDGE,"E6")])],"isStart":true})});var subQ2=makeQuery(id+"F5.imprint","INTERSECT",VERTEX,{"disambiguationData":[OD(0.0)],"derivedFrom":[subQ1,subQ0]});Q227=makeQuery(id+"F5.imprint","IMPRINT",FACE,{"disambiguationData":[TD([[makeQuery(id+"F5.imprint","IMPRINT",EDGE,{"disambiguationData":[TD([[subQ2,1.0]])],"derivedFrom":subQ0}),1.0]])]});}
            var Q228;
            {var subQ0=sQuery(id+"F5.wireOp",EDGE,"E12.1.143.0");var subQ1=makeQuery(id+"F3.boolean.opBoolean","COPY",EDGE,{"derivedFrom":makeQuery(id+"F3.opExtrude","CAP_EDGE",EDGE,{"disambiguationData":[OSD([sQuery(id+"F2.wireOp",EDGE,"E6")])],"isStart":true})});var subQ2=makeQuery(id+"F5.imprint","INTERSECT",VERTEX,{"disambiguationData":[OD(0.0)],"derivedFrom":[subQ1,subQ0]});Q228=makeQuery(id+"F5.imprint","IMPRINT",FACE,{"disambiguationData":[TD([[makeQuery(id+"F5.imprint","IMPRINT",EDGE,{"disambiguationData":[TD([[subQ2,-1.0]])],"derivedFrom":subQ0}),1.0]])]});}
            var Q229;
            {var subQ0=sQuery(id+"F5.wireOp",EDGE,"E12.1.132.0");var subQ1=makeQuery(id+"F3.boolean.opBoolean","COPY",EDGE,{"derivedFrom":makeQuery(id+"F3.opExtrude","CAP_EDGE",EDGE,{"disambiguationData":[OSD([sQuery(id+"F2.wireOp",EDGE,"E6")])],"isStart":true})});var subQ2=makeQuery(id+"F5.imprint","INTERSECT",VERTEX,{"disambiguationData":[OD(0.0)],"derivedFrom":[subQ1,subQ0]});Q229=makeQuery(id+"F5.imprint","IMPRINT",FACE,{"disambiguationData":[TD([[makeQuery(id+"F5.imprint","IMPRINT",EDGE,{"disambiguationData":[TD([[subQ2,1.0]])],"derivedFrom":subQ0}),1.0]])]});}
            var Q230;
            {var subQ0=sQuery(id+"F5.wireOp",EDGE,"E12.1.116.0");var subQ1=makeQuery(id+"F3.boolean.opBoolean","COPY",EDGE,{"derivedFrom":makeQuery(id+"F3.opExtrude","CAP_EDGE",EDGE,{"disambiguationData":[OSD([sQuery(id+"F2.wireOp",EDGE,"E6")])],"isStart":true})});var subQ2=makeQuery(id+"F5.imprint","INTERSECT",VERTEX,{"disambiguationData":[OD(0.0)],"derivedFrom":[subQ1,subQ0]});Q230=makeQuery(id+"F5.imprint","IMPRINT",FACE,{"disambiguationData":[TD([[makeQuery(id+"F5.imprint","IMPRINT",EDGE,{"disambiguationData":[TD([[subQ2,1.0]])],"derivedFrom":subQ0}),1.0]])]});}
            var Q231;
            {var subQ0=sQuery(id+"F5.wireOp",EDGE,"E12.1.112.0");var subQ1=makeQuery(id+"F3.boolean.opBoolean","COPY",EDGE,{"derivedFrom":makeQuery(id+"F3.opExtrude","CAP_EDGE",EDGE,{"disambiguationData":[OSD([sQuery(id+"F2.wireOp",EDGE,"E6")])],"isStart":true})});var subQ2=makeQuery(id+"F5.imprint","INTERSECT",VERTEX,{"disambiguationData":[OD(0.0)],"derivedFrom":[subQ1,subQ0]});Q231=makeQuery(id+"F5.imprint","IMPRINT",FACE,{"disambiguationData":[TD([[makeQuery(id+"F5.imprint","IMPRINT",EDGE,{"disambiguationData":[TD([[subQ2,-1.0]])],"derivedFrom":subQ0}),1.0]])]});}
            var Q232;
            {var subQ0=sQuery(id+"F5.wireOp",EDGE,"E12.1.133.0");var subQ1=makeQuery(id+"F3.boolean.opBoolean","COPY",EDGE,{"derivedFrom":makeQuery(id+"F3.opExtrude","CAP_EDGE",EDGE,{"disambiguationData":[OSD([sQuery(id+"F2.wireOp",EDGE,"E6")])],"isStart":true})});var subQ2=makeQuery(id+"F5.imprint","INTERSECT",VERTEX,{"disambiguationData":[OD(0.0)],"derivedFrom":[subQ1,subQ0]});Q232=makeQuery(id+"F5.imprint","IMPRINT",FACE,{"disambiguationData":[TD([[makeQuery(id+"F5.imprint","IMPRINT",EDGE,{"disambiguationData":[TD([[subQ2,1.0]])],"derivedFrom":subQ0}),1.0]])]});}
            var Q233;
            {var subQ0=sQuery(id+"F5.wireOp",EDGE,"E12.1.117.0");var subQ1=makeQuery(id+"F3.boolean.opBoolean","COPY",EDGE,{"derivedFrom":makeQuery(id+"F3.opExtrude","CAP_EDGE",EDGE,{"disambiguationData":[OSD([sQuery(id+"F2.wireOp",EDGE,"E6")])],"isStart":true})});var subQ2=makeQuery(id+"F5.imprint","INTERSECT",VERTEX,{"disambiguationData":[OD(0.0)],"derivedFrom":[subQ1,subQ0]});Q233=makeQuery(id+"F5.imprint","IMPRINT",FACE,{"disambiguationData":[TD([[makeQuery(id+"F5.imprint","IMPRINT",EDGE,{"disambiguationData":[TD([[subQ2,1.0]])],"derivedFrom":subQ0}),1.0]])]});}
            var Q234;
            {var subQ0=sQuery(id+"F5.wireOp",EDGE,"E12.1.145.0");var subQ1=makeQuery(id+"F3.boolean.opBoolean","COPY",EDGE,{"derivedFrom":makeQuery(id+"F3.opExtrude","CAP_EDGE",EDGE,{"disambiguationData":[OSD([sQuery(id+"F2.wireOp",EDGE,"E6")])],"isStart":true})});var subQ2=makeQuery(id+"F5.imprint","INTERSECT",VERTEX,{"disambiguationData":[OD(0.0)],"derivedFrom":[subQ1,subQ0]});Q234=makeQuery(id+"F5.imprint","IMPRINT",FACE,{"disambiguationData":[TD([[makeQuery(id+"F5.imprint","IMPRINT",EDGE,{"disambiguationData":[TD([[subQ2,-1.0]])],"derivedFrom":subQ0}),1.0]])]});}
            var Q235;
            {var subQ0=sQuery(id+"F5.wireOp",EDGE,"E12.1.134.0");var subQ1=makeQuery(id+"F3.boolean.opBoolean","COPY",EDGE,{"derivedFrom":makeQuery(id+"F3.opExtrude","CAP_EDGE",EDGE,{"disambiguationData":[OSD([sQuery(id+"F2.wireOp",EDGE,"E6")])],"isStart":true})});var subQ2=makeQuery(id+"F5.imprint","INTERSECT",VERTEX,{"disambiguationData":[OD(0.0)],"derivedFrom":[subQ1,subQ0]});Q235=makeQuery(id+"F5.imprint","IMPRINT",FACE,{"disambiguationData":[TD([[makeQuery(id+"F5.imprint","IMPRINT",EDGE,{"disambiguationData":[TD([[subQ2,1.0]])],"derivedFrom":subQ0}),1.0]])]});}
            var Q236;
            {var subQ0=sQuery(id+"F5.wireOp",EDGE,"E12.1.114.0");var subQ1=makeQuery(id+"F3.boolean.opBoolean","COPY",EDGE,{"derivedFrom":makeQuery(id+"F3.opExtrude","CAP_EDGE",EDGE,{"disambiguationData":[OSD([sQuery(id+"F2.wireOp",EDGE,"E6")])],"isStart":true})});var subQ2=makeQuery(id+"F5.imprint","INTERSECT",VERTEX,{"disambiguationData":[OD(0.0)],"derivedFrom":[subQ1,subQ0]});Q236=makeQuery(id+"F5.imprint","IMPRINT",FACE,{"disambiguationData":[TD([[makeQuery(id+"F5.imprint","IMPRINT",EDGE,{"disambiguationData":[TD([[subQ2,-1.0]])],"derivedFrom":subQ0}),1.0]])]});}
            var Q237;
            {var subQ0=sQuery(id+"F5.wireOp",EDGE,"E12.1.135.0");var subQ1=makeQuery(id+"F3.boolean.opBoolean","COPY",EDGE,{"derivedFrom":makeQuery(id+"F3.opExtrude","CAP_EDGE",EDGE,{"disambiguationData":[OSD([sQuery(id+"F2.wireOp",EDGE,"E6")])],"isStart":true})});var subQ2=makeQuery(id+"F5.imprint","INTERSECT",VERTEX,{"disambiguationData":[OD(0.0)],"derivedFrom":[subQ1,subQ0]});Q237=makeQuery(id+"F5.imprint","IMPRINT",FACE,{"disambiguationData":[TD([[makeQuery(id+"F5.imprint","IMPRINT",EDGE,{"disambiguationData":[TD([[subQ2,1.0]])],"derivedFrom":subQ0}),1.0]])]});}
            var Q238;
            {var subQ0=sQuery(id+"F5.wireOp",EDGE,"E12.1.147.0");var subQ1=makeQuery(id+"F3.boolean.opBoolean","COPY",EDGE,{"derivedFrom":makeQuery(id+"F3.opExtrude","CAP_EDGE",EDGE,{"disambiguationData":[OSD([sQuery(id+"F2.wireOp",EDGE,"E6")])],"isStart":true})});var subQ2=makeQuery(id+"F5.imprint","INTERSECT",VERTEX,{"disambiguationData":[OD(0.0)],"derivedFrom":[subQ1,subQ0]});Q238=makeQuery(id+"F5.imprint","IMPRINT",FACE,{"disambiguationData":[TD([[makeQuery(id+"F5.imprint","IMPRINT",EDGE,{"disambiguationData":[TD([[subQ2,-1.0]])],"derivedFrom":subQ0}),1.0]])]});}
            var Q239;
            {var subQ0=sQuery(id+"F5.wireOp",EDGE,"E12.1.137.0");var subQ1=makeQuery(id+"F3.boolean.opBoolean","COPY",EDGE,{"derivedFrom":makeQuery(id+"F3.opExtrude","CAP_EDGE",EDGE,{"disambiguationData":[OSD([sQuery(id+"F2.wireOp",EDGE,"E6")])],"isStart":true})});var subQ2=makeQuery(id+"F5.imprint","INTERSECT",VERTEX,{"disambiguationData":[OD(0.0)],"derivedFrom":[subQ1,subQ0]});Q239=makeQuery(id+"F5.imprint","IMPRINT",FACE,{"disambiguationData":[TD([[makeQuery(id+"F5.imprint","IMPRINT",EDGE,{"disambiguationData":[TD([[subQ2,1.0]])],"derivedFrom":subQ0}),1.0]])]});}
            var Q240;
            {var subQ0=sQuery(id+"F5.wireOp",EDGE,"E12.1.122.0");var subQ1=makeQuery(id+"F3.boolean.opBoolean","COPY",EDGE,{"derivedFrom":makeQuery(id+"F3.opExtrude","CAP_EDGE",EDGE,{"disambiguationData":[OSD([sQuery(id+"F2.wireOp",EDGE,"E6")])],"isStart":true})});var subQ2=makeQuery(id+"F5.imprint","INTERSECT",VERTEX,{"disambiguationData":[OD(0.0)],"derivedFrom":[subQ1,subQ0]});Q240=makeQuery(id+"F5.imprint","IMPRINT",FACE,{"disambiguationData":[TD([[makeQuery(id+"F5.imprint","IMPRINT",EDGE,{"disambiguationData":[TD([[subQ2,-1.0]])],"derivedFrom":subQ0}),1.0]])]});}
            var Q241;
            {var subQ0=sQuery(id+"F5.wireOp",EDGE,"E12.1.138.0");var subQ1=makeQuery(id+"F3.boolean.opBoolean","COPY",EDGE,{"derivedFrom":makeQuery(id+"F3.opExtrude","CAP_EDGE",EDGE,{"disambiguationData":[OSD([sQuery(id+"F2.wireOp",EDGE,"E6")])],"isStart":true})});var subQ2=makeQuery(id+"F5.imprint","INTERSECT",VERTEX,{"disambiguationData":[OD(0.0)],"derivedFrom":[subQ1,subQ0]});Q241=makeQuery(id+"F5.imprint","IMPRINT",FACE,{"disambiguationData":[TD([[makeQuery(id+"F5.imprint","IMPRINT",EDGE,{"disambiguationData":[TD([[subQ2,1.0]])],"derivedFrom":subQ0}),1.0]])]});}
            var Q242;
            {var subQ0=sQuery(id+"F5.wireOp",EDGE,"E12.1.119.0");var subQ1=makeQuery(id+"F3.boolean.opBoolean","COPY",EDGE,{"derivedFrom":makeQuery(id+"F3.opExtrude","CAP_EDGE",EDGE,{"disambiguationData":[OSD([sQuery(id+"F2.wireOp",EDGE,"E6")])],"isStart":true})});var subQ2=makeQuery(id+"F5.imprint","INTERSECT",VERTEX,{"disambiguationData":[OD(0.0)],"derivedFrom":[subQ1,subQ0]});Q242=makeQuery(id+"F5.imprint","IMPRINT",FACE,{"disambiguationData":[TD([[makeQuery(id+"F5.imprint","IMPRINT",EDGE,{"disambiguationData":[TD([[subQ2,-1.0]])],"derivedFrom":subQ0}),1.0]])]});}
            var Q243;
            {var subQ0=sQuery(id+"F5.wireOp",EDGE,"E12.1.111.0");var subQ1=makeQuery(id+"F3.boolean.opBoolean","COPY",EDGE,{"derivedFrom":makeQuery(id+"F3.opExtrude","CAP_EDGE",EDGE,{"disambiguationData":[OSD([sQuery(id+"F2.wireOp",EDGE,"E6")])],"isStart":true})});var subQ2=makeQuery(id+"F5.imprint","INTERSECT",VERTEX,{"disambiguationData":[OD(0.0)],"derivedFrom":[subQ1,subQ0]});Q243=makeQuery(id+"F5.imprint","IMPRINT",FACE,{"disambiguationData":[TD([[makeQuery(id+"F5.imprint","IMPRINT",EDGE,{"disambiguationData":[TD([[subQ2,1.0]])],"derivedFrom":subQ0}),1.0]])]});}
            var Q244;
            {var subQ0=sQuery(id+"F5.wireOp",EDGE,"E12.1.140.0");var subQ1=makeQuery(id+"F3.boolean.opBoolean","COPY",EDGE,{"derivedFrom":makeQuery(id+"F3.opExtrude","CAP_EDGE",EDGE,{"disambiguationData":[OSD([sQuery(id+"F2.wireOp",EDGE,"E6")])],"isStart":true})});var subQ2=makeQuery(id+"F5.imprint","INTERSECT",VERTEX,{"disambiguationData":[OD(0.0)],"derivedFrom":[subQ1,subQ0]});Q244=makeQuery(id+"F5.imprint","IMPRINT",FACE,{"disambiguationData":[TD([[makeQuery(id+"F5.imprint","IMPRINT",EDGE,{"disambiguationData":[TD([[subQ2,1.0]])],"derivedFrom":subQ0}),1.0]])]});}
            var Q245;
            {var subQ0=sQuery(id+"F5.wireOp",EDGE,"E12.1.120.0");var subQ1=makeQuery(id+"F3.boolean.opBoolean","COPY",EDGE,{"derivedFrom":makeQuery(id+"F3.opExtrude","CAP_EDGE",EDGE,{"disambiguationData":[OSD([sQuery(id+"F2.wireOp",EDGE,"E6")])],"isStart":true})});var subQ2=makeQuery(id+"F5.imprint","INTERSECT",VERTEX,{"disambiguationData":[OD(0.0)],"derivedFrom":[subQ1,subQ0]});Q245=makeQuery(id+"F5.imprint","IMPRINT",FACE,{"disambiguationData":[TD([[makeQuery(id+"F5.imprint","IMPRINT",EDGE,{"disambiguationData":[TD([[subQ2,-1.0]])],"derivedFrom":subQ0}),1.0]])]});}
            var Q246;
            {var subQ0=sQuery(id+"F5.wireOp",EDGE,"E12.1.113.0");var subQ1=makeQuery(id+"F3.boolean.opBoolean","COPY",EDGE,{"derivedFrom":makeQuery(id+"F3.opExtrude","CAP_EDGE",EDGE,{"disambiguationData":[OSD([sQuery(id+"F2.wireOp",EDGE,"E6")])],"isStart":true})});var subQ2=makeQuery(id+"F5.imprint","INTERSECT",VERTEX,{"disambiguationData":[OD(0.0)],"derivedFrom":[subQ1,subQ0]});Q246=makeQuery(id+"F5.imprint","IMPRINT",FACE,{"disambiguationData":[TD([[makeQuery(id+"F5.imprint","IMPRINT",EDGE,{"disambiguationData":[TD([[subQ2,1.0]])],"derivedFrom":subQ0}),1.0]])]});}
            var Q247;
            {var subQ0=sQuery(id+"F5.wireOp",EDGE,"E12.1.141.0");var subQ1=makeQuery(id+"F3.boolean.opBoolean","COPY",EDGE,{"derivedFrom":makeQuery(id+"F3.opExtrude","CAP_EDGE",EDGE,{"disambiguationData":[OSD([sQuery(id+"F2.wireOp",EDGE,"E6")])],"isStart":true})});var subQ2=makeQuery(id+"F5.imprint","INTERSECT",VERTEX,{"disambiguationData":[OD(0.0)],"derivedFrom":[subQ1,subQ0]});Q247=makeQuery(id+"F5.imprint","IMPRINT",FACE,{"disambiguationData":[TD([[makeQuery(id+"F5.imprint","IMPRINT",EDGE,{"disambiguationData":[TD([[subQ2,-1.0]])],"derivedFrom":subQ0}),1.0]])]});}
            var Q248;
            {var subQ0=sQuery(id+"F5.wireOp",EDGE,"E12.1.145.0");var subQ1=makeQuery(id+"F3.boolean.opBoolean","COPY",EDGE,{"derivedFrom":makeQuery(id+"F3.opExtrude","CAP_EDGE",EDGE,{"disambiguationData":[OSD([sQuery(id+"F2.wireOp",EDGE,"E6")])],"isStart":true})});var subQ2=makeQuery(id+"F5.imprint","INTERSECT",VERTEX,{"disambiguationData":[OD(0.0)],"derivedFrom":[subQ1,subQ0]});Q248=makeQuery(id+"F5.imprint","IMPRINT",FACE,{"disambiguationData":[TD([[makeQuery(id+"F5.imprint","IMPRINT",EDGE,{"disambiguationData":[TD([[subQ2,1.0]])],"derivedFrom":subQ0}),1.0]])]});}
            var Q249;
            {var subQ0=sQuery(id+"F5.wireOp",EDGE,"E12.1.114.0");var subQ1=makeQuery(id+"F3.boolean.opBoolean","COPY",EDGE,{"derivedFrom":makeQuery(id+"F3.opExtrude","CAP_EDGE",EDGE,{"disambiguationData":[OSD([sQuery(id+"F2.wireOp",EDGE,"E6")])],"isStart":true})});var subQ2=makeQuery(id+"F5.imprint","INTERSECT",VERTEX,{"disambiguationData":[OD(0.0)],"derivedFrom":[subQ1,subQ0]});Q249=makeQuery(id+"F5.imprint","IMPRINT",FACE,{"disambiguationData":[TD([[makeQuery(id+"F5.imprint","IMPRINT",EDGE,{"disambiguationData":[TD([[subQ2,1.0]])],"derivedFrom":subQ0}),1.0]])]});}
            var Q250;
            {var subQ0=sQuery(id+"F5.wireOp",EDGE,"E12.1.129.0");var subQ1=makeQuery(id+"F3.boolean.opBoolean","COPY",EDGE,{"derivedFrom":makeQuery(id+"F3.opExtrude","CAP_EDGE",EDGE,{"disambiguationData":[OSD([sQuery(id+"F2.wireOp",EDGE,"E6")])],"isStart":true})});var subQ2=makeQuery(id+"F5.imprint","INTERSECT",VERTEX,{"disambiguationData":[OD(0.0)],"derivedFrom":[subQ1,subQ0]});Q250=makeQuery(id+"F5.imprint","IMPRINT",FACE,{"disambiguationData":[TD([[makeQuery(id+"F5.imprint","IMPRINT",EDGE,{"disambiguationData":[TD([[subQ2,1.0]])],"derivedFrom":subQ0}),1.0]])]});}
            var Q251;
            {var subQ0=sQuery(id+"F5.wireOp",EDGE,"E12.1.142.0");var subQ1=makeQuery(id+"F3.boolean.opBoolean","COPY",EDGE,{"derivedFrom":makeQuery(id+"F3.opExtrude","CAP_EDGE",EDGE,{"disambiguationData":[OSD([sQuery(id+"F2.wireOp",EDGE,"E6")])],"isStart":true})});var subQ2=makeQuery(id+"F5.imprint","INTERSECT",VERTEX,{"disambiguationData":[OD(0.0)],"derivedFrom":[subQ1,subQ0]});Q251=makeQuery(id+"F5.imprint","IMPRINT",FACE,{"disambiguationData":[TD([[makeQuery(id+"F5.imprint","IMPRINT",EDGE,{"disambiguationData":[TD([[subQ2,-1.0]])],"derivedFrom":subQ0}),1.0]])]});}
            var Q252;
            {var subQ0=sQuery(id+"F5.wireOp",EDGE,"E12.1.140.0");var subQ1=makeQuery(id+"F3.boolean.opBoolean","COPY",EDGE,{"derivedFrom":makeQuery(id+"F3.opExtrude","CAP_EDGE",EDGE,{"disambiguationData":[OSD([sQuery(id+"F2.wireOp",EDGE,"E6")])],"isStart":true})});var subQ2=makeQuery(id+"F5.imprint","INTERSECT",VERTEX,{"disambiguationData":[OD(0.0)],"derivedFrom":[subQ1,subQ0]});Q252=makeQuery(id+"F5.imprint","IMPRINT",FACE,{"disambiguationData":[TD([[makeQuery(id+"F5.imprint","IMPRINT",EDGE,{"disambiguationData":[TD([[subQ2,-1.0]])],"derivedFrom":subQ0}),1.0]])]});}
            var Q253;
            {var subQ0=sQuery(id+"F5.wireOp",EDGE,"E12.1.112.0");var subQ1=makeQuery(id+"F3.boolean.opBoolean","COPY",EDGE,{"derivedFrom":makeQuery(id+"F3.opExtrude","CAP_EDGE",EDGE,{"disambiguationData":[OSD([sQuery(id+"F2.wireOp",EDGE,"E6")])],"isStart":true})});var subQ2=makeQuery(id+"F5.imprint","INTERSECT",VERTEX,{"disambiguationData":[OD(0.0)],"derivedFrom":[subQ1,subQ0]});Q253=makeQuery(id+"F5.imprint","IMPRINT",FACE,{"disambiguationData":[TD([[makeQuery(id+"F5.imprint","IMPRINT",EDGE,{"disambiguationData":[TD([[subQ2,1.0]])],"derivedFrom":subQ0}),1.0]])]});}
            var Q254;
            {var subQ0=sQuery(id+"F5.wireOp",EDGE,"E12.1.144.0");var subQ1=makeQuery(id+"F3.boolean.opBoolean","COPY",EDGE,{"derivedFrom":makeQuery(id+"F3.opExtrude","CAP_EDGE",EDGE,{"disambiguationData":[OSD([sQuery(id+"F2.wireOp",EDGE,"E6")])],"isStart":true})});var subQ2=makeQuery(id+"F5.imprint","INTERSECT",VERTEX,{"disambiguationData":[OD(0.0)],"derivedFrom":[subQ1,subQ0]});Q254=makeQuery(id+"F5.imprint","IMPRINT",FACE,{"disambiguationData":[TD([[makeQuery(id+"F5.imprint","IMPRINT",EDGE,{"disambiguationData":[TD([[subQ2,1.0]])],"derivedFrom":subQ0}),1.0]])]});}
            var Q255;
            {var subQ0=sQuery(id+"F5.wireOp",EDGE,"E12.1.141.0");var subQ1=makeQuery(id+"F3.boolean.opBoolean","COPY",EDGE,{"derivedFrom":makeQuery(id+"F3.opExtrude","CAP_EDGE",EDGE,{"disambiguationData":[OSD([sQuery(id+"F2.wireOp",EDGE,"E6")])],"isStart":true})});var subQ2=makeQuery(id+"F5.imprint","INTERSECT",VERTEX,{"disambiguationData":[OD(0.0)],"derivedFrom":[subQ1,subQ0]});Q255=makeQuery(id+"F5.imprint","IMPRINT",FACE,{"disambiguationData":[TD([[makeQuery(id+"F5.imprint","IMPRINT",EDGE,{"disambiguationData":[TD([[subQ2,1.0]])],"derivedFrom":subQ0}),1.0]])]});}
            var Q256;
            {var subQ0=sQuery(id+"F5.wireOp",EDGE,"E12.1.147.0");var subQ1=makeQuery(id+"F3.boolean.opBoolean","COPY",EDGE,{"derivedFrom":makeQuery(id+"F3.opExtrude","CAP_EDGE",EDGE,{"disambiguationData":[OSD([sQuery(id+"F2.wireOp",EDGE,"E6")])],"isStart":true})});var subQ2=makeQuery(id+"F5.imprint","INTERSECT",VERTEX,{"disambiguationData":[OD(0.0)],"derivedFrom":[subQ1,subQ0]});Q256=makeQuery(id+"F5.imprint","IMPRINT",FACE,{"disambiguationData":[TD([[makeQuery(id+"F5.imprint","IMPRINT",EDGE,{"disambiguationData":[TD([[subQ2,1.0]])],"derivedFrom":subQ0}),1.0]])]});}
            var Q257;
            {var subQ0=sQuery(id+"F5.wireOp",EDGE,"E12.1.115.0");var subQ1=makeQuery(id+"F3.boolean.opBoolean","COPY",EDGE,{"derivedFrom":makeQuery(id+"F3.opExtrude","CAP_EDGE",EDGE,{"disambiguationData":[OSD([sQuery(id+"F2.wireOp",EDGE,"E6")])],"isStart":true})});var subQ2=makeQuery(id+"F5.imprint","INTERSECT",VERTEX,{"disambiguationData":[OD(0.0)],"derivedFrom":[subQ1,subQ0]});Q257=makeQuery(id+"F5.imprint","IMPRINT",FACE,{"disambiguationData":[TD([[makeQuery(id+"F5.imprint","IMPRINT",EDGE,{"disambiguationData":[TD([[subQ2,1.0]])],"derivedFrom":subQ0}),1.0]])]});}
            var Q258;
            {var subQ0=sQuery(id+"F5.wireOp",EDGE,"E12.1.111.0");var subQ1=makeQuery(id+"F3.boolean.opBoolean","COPY",EDGE,{"derivedFrom":makeQuery(id+"F3.opExtrude","CAP_EDGE",EDGE,{"disambiguationData":[OSD([sQuery(id+"F2.wireOp",EDGE,"E6")])],"isStart":true})});var subQ2=makeQuery(id+"F5.imprint","INTERSECT",VERTEX,{"disambiguationData":[OD(0.0)],"derivedFrom":[subQ1,subQ0]});Q258=makeQuery(id+"F5.imprint","IMPRINT",FACE,{"disambiguationData":[TD([[makeQuery(id+"F5.imprint","IMPRINT",EDGE,{"disambiguationData":[TD([[subQ2,-1.0]])],"derivedFrom":subQ0}),1.0]])]});}
            var Q259;
            {var subQ0=sQuery(id+"F5.wireOp",EDGE,"E12.1.127.0");var subQ1=makeQuery(id+"F3.boolean.opBoolean","COPY",EDGE,{"derivedFrom":makeQuery(id+"F3.opExtrude","CAP_EDGE",EDGE,{"disambiguationData":[OSD([sQuery(id+"F2.wireOp",EDGE,"E6")])],"isStart":true})});var subQ2=makeQuery(id+"F5.imprint","INTERSECT",VERTEX,{"disambiguationData":[OD(0.0)],"derivedFrom":[subQ1,subQ0]});Q259=makeQuery(id+"F5.imprint","IMPRINT",FACE,{"disambiguationData":[TD([[makeQuery(id+"F5.imprint","IMPRINT",EDGE,{"disambiguationData":[TD([[subQ2,-1.0]])],"derivedFrom":subQ0}),1.0]])]});}
            var Q260;
            {var subQ0=sQuery(id+"F5.wireOp",EDGE,"E12.1.121.0");var subQ1=makeQuery(id+"F3.boolean.opBoolean","COPY",EDGE,{"derivedFrom":makeQuery(id+"F3.opExtrude","CAP_EDGE",EDGE,{"disambiguationData":[OSD([sQuery(id+"F2.wireOp",EDGE,"E6")])],"isStart":true})});var subQ2=makeQuery(id+"F5.imprint","INTERSECT",VERTEX,{"disambiguationData":[OD(0.0)],"derivedFrom":[subQ1,subQ0]});Q260=makeQuery(id+"F5.imprint","IMPRINT",FACE,{"disambiguationData":[TD([[makeQuery(id+"F5.imprint","IMPRINT",EDGE,{"disambiguationData":[TD([[subQ2,-1.0]])],"derivedFrom":subQ0}),1.0]])]});}
            var Q261;
            {var subQ0=sQuery(id+"F5.wireOp",EDGE,"E12.1.126.0");var subQ1=makeQuery(id+"F3.boolean.opBoolean","COPY",EDGE,{"derivedFrom":makeQuery(id+"F3.opExtrude","CAP_EDGE",EDGE,{"disambiguationData":[OSD([sQuery(id+"F2.wireOp",EDGE,"E6")])],"isStart":true})});var subQ2=makeQuery(id+"F5.imprint","INTERSECT",VERTEX,{"disambiguationData":[OD(0.0)],"derivedFrom":[subQ1,subQ0]});Q261=makeQuery(id+"F5.imprint","IMPRINT",FACE,{"disambiguationData":[TD([[makeQuery(id+"F5.imprint","IMPRINT",EDGE,{"disambiguationData":[TD([[subQ2,1.0]])],"derivedFrom":subQ0}),1.0]])]});}
            var Q262;
            {var subQ0=sQuery(id+"F5.wireOp",EDGE,"E12.1.148.0");var subQ1=makeQuery(id+"F3.boolean.opBoolean","COPY",EDGE,{"derivedFrom":makeQuery(id+"F3.opExtrude","CAP_EDGE",EDGE,{"disambiguationData":[OSD([sQuery(id+"F2.wireOp",EDGE,"E6")])],"isStart":true})});var subQ2=makeQuery(id+"F5.imprint","INTERSECT",VERTEX,{"disambiguationData":[OD(0.0)],"derivedFrom":[subQ1,subQ0]});Q262=makeQuery(id+"F5.imprint","IMPRINT",FACE,{"disambiguationData":[TD([[makeQuery(id+"F5.imprint","IMPRINT",EDGE,{"disambiguationData":[TD([[subQ2,1.0]])],"derivedFrom":subQ0}),1.0]])]});}
            var Q263;
            {var subQ0=sQuery(id+"F5.wireOp",EDGE,"E12.1.137.0");var subQ1=makeQuery(id+"F3.boolean.opBoolean","COPY",EDGE,{"derivedFrom":makeQuery(id+"F3.opExtrude","CAP_EDGE",EDGE,{"disambiguationData":[OSD([sQuery(id+"F2.wireOp",EDGE,"E6")])],"isStart":true})});var subQ2=makeQuery(id+"F5.imprint","INTERSECT",VERTEX,{"disambiguationData":[OD(0.0)],"derivedFrom":[subQ1,subQ0]});Q263=makeQuery(id+"F5.imprint","IMPRINT",FACE,{"disambiguationData":[TD([[makeQuery(id+"F5.imprint","IMPRINT",EDGE,{"disambiguationData":[TD([[subQ2,-1.0]])],"derivedFrom":subQ0}),1.0]])]});}
            var Q264;
            {var subQ0=sQuery(id+"F5.wireOp",EDGE,"E12.1.128.0");var subQ1=makeQuery(id+"F3.boolean.opBoolean","COPY",EDGE,{"derivedFrom":makeQuery(id+"F3.opExtrude","CAP_EDGE",EDGE,{"disambiguationData":[OSD([sQuery(id+"F2.wireOp",EDGE,"E6")])],"isStart":true})});var subQ2=makeQuery(id+"F5.imprint","INTERSECT",VERTEX,{"disambiguationData":[OD(0.0)],"derivedFrom":[subQ1,subQ0]});Q264=makeQuery(id+"F5.imprint","IMPRINT",FACE,{"disambiguationData":[TD([[makeQuery(id+"F5.imprint","IMPRINT",EDGE,{"disambiguationData":[TD([[subQ2,-1.0]])],"derivedFrom":subQ0}),1.0]])]});}
            var Q265;
            {var subQ0=sQuery(id+"F5.wireOp",EDGE,"E12.1.144.0");var subQ1=makeQuery(id+"F3.boolean.opBoolean","COPY",EDGE,{"derivedFrom":makeQuery(id+"F3.opExtrude","CAP_EDGE",EDGE,{"disambiguationData":[OSD([sQuery(id+"F2.wireOp",EDGE,"E6")])],"isStart":true})});var subQ2=makeQuery(id+"F5.imprint","INTERSECT",VERTEX,{"disambiguationData":[OD(0.0)],"derivedFrom":[subQ1,subQ0]});Q265=makeQuery(id+"F5.imprint","IMPRINT",FACE,{"disambiguationData":[TD([[makeQuery(id+"F5.imprint","IMPRINT",EDGE,{"disambiguationData":[TD([[subQ2,-1.0]])],"derivedFrom":subQ0}),1.0]])]});}
            var Q266;
            {var subQ0=sQuery(id+"F5.wireOp",EDGE,"E12.1.129.0");var subQ1=makeQuery(id+"F3.boolean.opBoolean","COPY",EDGE,{"derivedFrom":makeQuery(id+"F3.opExtrude","CAP_EDGE",EDGE,{"disambiguationData":[OSD([sQuery(id+"F2.wireOp",EDGE,"E6")])],"isStart":true})});var subQ2=makeQuery(id+"F5.imprint","INTERSECT",VERTEX,{"disambiguationData":[OD(0.0)],"derivedFrom":[subQ1,subQ0]});Q266=makeQuery(id+"F5.imprint","IMPRINT",FACE,{"disambiguationData":[TD([[makeQuery(id+"F5.imprint","IMPRINT",EDGE,{"disambiguationData":[TD([[subQ2,-1.0]])],"derivedFrom":subQ0}),1.0]])]});}
            var Q267;
            {var subQ0=sQuery(id+"F5.wireOp",EDGE,"E12.1.113.0");var subQ1=makeQuery(id+"F3.boolean.opBoolean","COPY",EDGE,{"derivedFrom":makeQuery(id+"F3.opExtrude","CAP_EDGE",EDGE,{"disambiguationData":[OSD([sQuery(id+"F2.wireOp",EDGE,"E6")])],"isStart":true})});var subQ2=makeQuery(id+"F5.imprint","INTERSECT",VERTEX,{"disambiguationData":[OD(0.0)],"derivedFrom":[subQ1,subQ0]});Q267=makeQuery(id+"F5.imprint","IMPRINT",FACE,{"disambiguationData":[TD([[makeQuery(id+"F5.imprint","IMPRINT",EDGE,{"disambiguationData":[TD([[subQ2,-1.0]])],"derivedFrom":subQ0}),1.0]])]});}
            var Q268;
            {var subQ0=sQuery(id+"F5.wireOp",EDGE,"E12.1.118.0");var subQ1=makeQuery(id+"F3.boolean.opBoolean","COPY",EDGE,{"derivedFrom":makeQuery(id+"F3.opExtrude","CAP_EDGE",EDGE,{"disambiguationData":[OSD([sQuery(id+"F2.wireOp",EDGE,"E6")])],"isStart":true})});var subQ2=makeQuery(id+"F5.imprint","INTERSECT",VERTEX,{"disambiguationData":[OD(0.0)],"derivedFrom":[subQ1,subQ0]});Q268=makeQuery(id+"F5.imprint","IMPRINT",FACE,{"disambiguationData":[TD([[makeQuery(id+"F5.imprint","IMPRINT",EDGE,{"disambiguationData":[TD([[subQ2,1.0]])],"derivedFrom":subQ0}),1.0]])]});}
            var Q269;
            {var subQ0=sQuery(id+"F5.wireOp",EDGE,"E12.1.146.0");var subQ1=makeQuery(id+"F3.boolean.opBoolean","COPY",EDGE,{"derivedFrom":makeQuery(id+"F3.opExtrude","CAP_EDGE",EDGE,{"disambiguationData":[OSD([sQuery(id+"F2.wireOp",EDGE,"E6")])],"isStart":true})});var subQ2=makeQuery(id+"F5.imprint","INTERSECT",VERTEX,{"disambiguationData":[OD(0.0)],"derivedFrom":[subQ1,subQ0]});Q269=makeQuery(id+"F5.imprint","IMPRINT",FACE,{"disambiguationData":[TD([[makeQuery(id+"F5.imprint","IMPRINT",EDGE,{"disambiguationData":[TD([[subQ2,-1.0]])],"derivedFrom":subQ0}),1.0]])]});}
            var Q270;
            {var subQ0=sQuery(id+"F5.wireOp",EDGE,"E12.1.130.0");var subQ1=makeQuery(id+"F3.boolean.opBoolean","COPY",EDGE,{"derivedFrom":makeQuery(id+"F3.opExtrude","CAP_EDGE",EDGE,{"disambiguationData":[OSD([sQuery(id+"F2.wireOp",EDGE,"E6")])],"isStart":true})});var subQ2=makeQuery(id+"F5.imprint","INTERSECT",VERTEX,{"disambiguationData":[OD(0.0)],"derivedFrom":[subQ1,subQ0]});Q270=makeQuery(id+"F5.imprint","IMPRINT",FACE,{"disambiguationData":[TD([[makeQuery(id+"F5.imprint","IMPRINT",EDGE,{"disambiguationData":[TD([[subQ2,-1.0]])],"derivedFrom":subQ0}),1.0]])]});}
            var Q271;
            {var subQ0=sQuery(id+"F5.wireOp",EDGE,"E12.1.119.0");var subQ1=makeQuery(id+"F3.boolean.opBoolean","COPY",EDGE,{"derivedFrom":makeQuery(id+"F3.opExtrude","CAP_EDGE",EDGE,{"disambiguationData":[OSD([sQuery(id+"F2.wireOp",EDGE,"E6")])],"isStart":true})});var subQ2=makeQuery(id+"F5.imprint","INTERSECT",VERTEX,{"disambiguationData":[OD(0.0)],"derivedFrom":[subQ1,subQ0]});Q271=makeQuery(id+"F5.imprint","IMPRINT",FACE,{"disambiguationData":[TD([[makeQuery(id+"F5.imprint","IMPRINT",EDGE,{"disambiguationData":[TD([[subQ2,1.0]])],"derivedFrom":subQ0}),1.0]])]});}
            var Q272;
            {var subQ0=sQuery(id+"F5.wireOp",EDGE,"E12.1.131.0");var subQ1=makeQuery(id+"F3.boolean.opBoolean","COPY",EDGE,{"derivedFrom":makeQuery(id+"F3.opExtrude","CAP_EDGE",EDGE,{"disambiguationData":[OSD([sQuery(id+"F2.wireOp",EDGE,"E6")])],"isStart":true})});var subQ2=makeQuery(id+"F5.imprint","INTERSECT",VERTEX,{"disambiguationData":[OD(0.0)],"derivedFrom":[subQ1,subQ0]});Q272=makeQuery(id+"F5.imprint","IMPRINT",FACE,{"disambiguationData":[TD([[makeQuery(id+"F5.imprint","IMPRINT",EDGE,{"disambiguationData":[TD([[subQ2,-1.0]])],"derivedFrom":subQ0}),1.0]])]});}
            var Q273;
            {var subQ0=sQuery(id+"F5.wireOp",EDGE,"E12.1.115.0");var subQ1=makeQuery(id+"F3.boolean.opBoolean","COPY",EDGE,{"derivedFrom":makeQuery(id+"F3.opExtrude","CAP_EDGE",EDGE,{"disambiguationData":[OSD([sQuery(id+"F2.wireOp",EDGE,"E6")])],"isStart":true})});var subQ2=makeQuery(id+"F5.imprint","INTERSECT",VERTEX,{"disambiguationData":[OD(0.0)],"derivedFrom":[subQ1,subQ0]});Q273=makeQuery(id+"F5.imprint","IMPRINT",FACE,{"disambiguationData":[TD([[makeQuery(id+"F5.imprint","IMPRINT",EDGE,{"disambiguationData":[TD([[subQ2,-1.0]])],"derivedFrom":subQ0}),1.0]])]});}
            var Q274;
            {var subQ0=sQuery(id+"F5.wireOp",EDGE,"E12.1.120.0");var subQ1=makeQuery(id+"F3.boolean.opBoolean","COPY",EDGE,{"derivedFrom":makeQuery(id+"F3.opExtrude","CAP_EDGE",EDGE,{"disambiguationData":[OSD([sQuery(id+"F2.wireOp",EDGE,"E6")])],"isStart":true})});var subQ2=makeQuery(id+"F5.imprint","INTERSECT",VERTEX,{"disambiguationData":[OD(0.0)],"derivedFrom":[subQ1,subQ0]});Q274=makeQuery(id+"F5.imprint","IMPRINT",FACE,{"disambiguationData":[TD([[makeQuery(id+"F5.imprint","IMPRINT",EDGE,{"disambiguationData":[TD([[subQ2,1.0]])],"derivedFrom":subQ0}),1.0]])]});}
            var Q275;
            {var subQ0=sQuery(id+"F5.wireOp",EDGE,"E12.1.136.0");var subQ1=makeQuery(id+"F3.boolean.opBoolean","COPY",EDGE,{"derivedFrom":makeQuery(id+"F3.opExtrude","CAP_EDGE",EDGE,{"disambiguationData":[OSD([sQuery(id+"F2.wireOp",EDGE,"E6")])],"isStart":true})});var subQ2=makeQuery(id+"F5.imprint","INTERSECT",VERTEX,{"disambiguationData":[OD(0.0)],"derivedFrom":[subQ1,subQ0]});Q275=makeQuery(id+"F5.imprint","IMPRINT",FACE,{"disambiguationData":[TD([[makeQuery(id+"F5.imprint","IMPRINT",EDGE,{"disambiguationData":[TD([[subQ2,1.0]])],"derivedFrom":subQ0}),1.0]])]});}
            var Q276;
            {var subQ0=sQuery(id+"F5.wireOp",EDGE,"E12.1.148.0");var subQ1=makeQuery(id+"F3.boolean.opBoolean","COPY",EDGE,{"derivedFrom":makeQuery(id+"F3.opExtrude","CAP_EDGE",EDGE,{"disambiguationData":[OSD([sQuery(id+"F2.wireOp",EDGE,"E6")])],"isStart":true})});var subQ2=makeQuery(id+"F5.imprint","INTERSECT",VERTEX,{"disambiguationData":[OD(0.0)],"derivedFrom":[subQ1,subQ0]});Q276=makeQuery(id+"F5.imprint","IMPRINT",FACE,{"disambiguationData":[TD([[makeQuery(id+"F5.imprint","IMPRINT",EDGE,{"disambiguationData":[TD([[subQ2,-1.0]])],"derivedFrom":subQ0}),1.0]])]});}
            var Q277;
            {var subQ0=sQuery(id+"F5.wireOp",EDGE,"E12.1.132.0");var subQ1=makeQuery(id+"F3.boolean.opBoolean","COPY",EDGE,{"derivedFrom":makeQuery(id+"F3.opExtrude","CAP_EDGE",EDGE,{"disambiguationData":[OSD([sQuery(id+"F2.wireOp",EDGE,"E6")])],"isStart":true})});var subQ2=makeQuery(id+"F5.imprint","INTERSECT",VERTEX,{"disambiguationData":[OD(0.0)],"derivedFrom":[subQ1,subQ0]});Q277=makeQuery(id+"F5.imprint","IMPRINT",FACE,{"disambiguationData":[TD([[makeQuery(id+"F5.imprint","IMPRINT",EDGE,{"disambiguationData":[TD([[subQ2,-1.0]])],"derivedFrom":subQ0}),1.0]])]});}
            var Q278;
            {var subQ0=sQuery(id+"F5.wireOp",EDGE,"E12.1.116.0");var subQ1=makeQuery(id+"F3.boolean.opBoolean","COPY",EDGE,{"derivedFrom":makeQuery(id+"F3.opExtrude","CAP_EDGE",EDGE,{"disambiguationData":[OSD([sQuery(id+"F2.wireOp",EDGE,"E6")])],"isStart":true})});var subQ2=makeQuery(id+"F5.imprint","INTERSECT",VERTEX,{"disambiguationData":[OD(0.0)],"derivedFrom":[subQ1,subQ0]});Q278=makeQuery(id+"F5.imprint","IMPRINT",FACE,{"disambiguationData":[TD([[makeQuery(id+"F5.imprint","IMPRINT",EDGE,{"disambiguationData":[TD([[subQ2,-1.0]])],"derivedFrom":subQ0}),1.0]])]});}
            var Q279;
            {var subQ0=sQuery(id+"F5.wireOp",EDGE,"E12.1.133.0");var subQ1=makeQuery(id+"F3.boolean.opBoolean","COPY",EDGE,{"derivedFrom":makeQuery(id+"F3.opExtrude","CAP_EDGE",EDGE,{"disambiguationData":[OSD([sQuery(id+"F2.wireOp",EDGE,"E6")])],"isStart":true})});var subQ2=makeQuery(id+"F5.imprint","INTERSECT",VERTEX,{"disambiguationData":[OD(0.0)],"derivedFrom":[subQ1,subQ0]});Q279=makeQuery(id+"F5.imprint","IMPRINT",FACE,{"disambiguationData":[TD([[makeQuery(id+"F5.imprint","IMPRINT",EDGE,{"disambiguationData":[TD([[subQ2,-1.0]])],"derivedFrom":subQ0}),1.0]])]});}
            var Q280;
            {var subQ0=sQuery(id+"F5.wireOp",EDGE,"E12.1.117.0");var subQ1=makeQuery(id+"F3.boolean.opBoolean","COPY",EDGE,{"derivedFrom":makeQuery(id+"F3.opExtrude","CAP_EDGE",EDGE,{"disambiguationData":[OSD([sQuery(id+"F2.wireOp",EDGE,"E6")])],"isStart":true})});var subQ2=makeQuery(id+"F5.imprint","INTERSECT",VERTEX,{"disambiguationData":[OD(0.0)],"derivedFrom":[subQ1,subQ0]});Q280=makeQuery(id+"F5.imprint","IMPRINT",FACE,{"disambiguationData":[TD([[makeQuery(id+"F5.imprint","IMPRINT",EDGE,{"disambiguationData":[TD([[subQ2,-1.0]])],"derivedFrom":subQ0}),1.0]])]});}
            var Q281;
            {var subQ0=sQuery(id+"F5.wireOp",EDGE,"E12.1.121.0");var subQ1=makeQuery(id+"F3.boolean.opBoolean","COPY",EDGE,{"derivedFrom":makeQuery(id+"F3.opExtrude","CAP_EDGE",EDGE,{"disambiguationData":[OSD([sQuery(id+"F2.wireOp",EDGE,"E6")])],"isStart":true})});var subQ2=makeQuery(id+"F5.imprint","INTERSECT",VERTEX,{"disambiguationData":[OD(0.0)],"derivedFrom":[subQ1,subQ0]});Q281=makeQuery(id+"F5.imprint","IMPRINT",FACE,{"disambiguationData":[TD([[makeQuery(id+"F5.imprint","IMPRINT",EDGE,{"disambiguationData":[TD([[subQ2,1.0]])],"derivedFrom":subQ0}),1.0]])]});}
            var Q282;
            {var subQ0=sQuery(id+"F5.wireOp",EDGE,"E12.1.134.0");var subQ1=makeQuery(id+"F3.boolean.opBoolean","COPY",EDGE,{"derivedFrom":makeQuery(id+"F3.opExtrude","CAP_EDGE",EDGE,{"disambiguationData":[OSD([sQuery(id+"F2.wireOp",EDGE,"E6")])],"isStart":true})});var subQ2=makeQuery(id+"F5.imprint","INTERSECT",VERTEX,{"disambiguationData":[OD(0.0)],"derivedFrom":[subQ1,subQ0]});Q282=makeQuery(id+"F5.imprint","IMPRINT",FACE,{"disambiguationData":[TD([[makeQuery(id+"F5.imprint","IMPRINT",EDGE,{"disambiguationData":[TD([[subQ2,-1.0]])],"derivedFrom":subQ0}),1.0]])]});}
            var Q283;
            {var subQ0=sQuery(id+"F5.wireOp",EDGE,"E12.1.118.0");var subQ1=makeQuery(id+"F3.boolean.opBoolean","COPY",EDGE,{"derivedFrom":makeQuery(id+"F3.opExtrude","CAP_EDGE",EDGE,{"disambiguationData":[OSD([sQuery(id+"F2.wireOp",EDGE,"E6")])],"isStart":true})});var subQ2=makeQuery(id+"F5.imprint","INTERSECT",VERTEX,{"disambiguationData":[OD(0.0)],"derivedFrom":[subQ1,subQ0]});Q283=makeQuery(id+"F5.imprint","IMPRINT",FACE,{"disambiguationData":[TD([[makeQuery(id+"F5.imprint","IMPRINT",EDGE,{"disambiguationData":[TD([[subQ2,-1.0]])],"derivedFrom":subQ0}),1.0]])]});}
            var Q284;
            {var subQ0=sQuery(id+"F5.wireOp",EDGE,"E12.1.122.0");var subQ1=makeQuery(id+"F3.boolean.opBoolean","COPY",EDGE,{"derivedFrom":makeQuery(id+"F3.opExtrude","CAP_EDGE",EDGE,{"disambiguationData":[OSD([sQuery(id+"F2.wireOp",EDGE,"E6")])],"isStart":true})});var subQ2=makeQuery(id+"F5.imprint","INTERSECT",VERTEX,{"disambiguationData":[OD(0.0)],"derivedFrom":[subQ1,subQ0]});Q284=makeQuery(id+"F5.imprint","IMPRINT",FACE,{"disambiguationData":[TD([[makeQuery(id+"F5.imprint","IMPRINT",EDGE,{"disambiguationData":[TD([[subQ2,1.0]])],"derivedFrom":subQ0}),1.0]])]});}
            var Q285;
            {var subQ0=sQuery(id+"F5.wireOp",EDGE,"E12.1.138.0");var subQ1=makeQuery(id+"F3.boolean.opBoolean","COPY",EDGE,{"derivedFrom":makeQuery(id+"F3.opExtrude","CAP_EDGE",EDGE,{"disambiguationData":[OSD([sQuery(id+"F2.wireOp",EDGE,"E6")])],"isStart":true})});var subQ2=makeQuery(id+"F5.imprint","INTERSECT",VERTEX,{"disambiguationData":[OD(0.0)],"derivedFrom":[subQ1,subQ0]});Q285=makeQuery(id+"F5.imprint","IMPRINT",FACE,{"disambiguationData":[TD([[makeQuery(id+"F5.imprint","IMPRINT",EDGE,{"disambiguationData":[TD([[subQ2,-1.0]])],"derivedFrom":subQ0}),1.0]])]});}
            var Q286;
            {var subQ0=sQuery(id+"F5.wireOp",EDGE,"E12.1.143.0");var subQ1=makeQuery(id+"F3.boolean.opBoolean","COPY",EDGE,{"derivedFrom":makeQuery(id+"F3.opExtrude","CAP_EDGE",EDGE,{"disambiguationData":[OSD([sQuery(id+"F2.wireOp",EDGE,"E6")])],"isStart":true})});var subQ2=makeQuery(id+"F5.imprint","INTERSECT",VERTEX,{"disambiguationData":[OD(0.0)],"derivedFrom":[subQ1,subQ0]});Q286=makeQuery(id+"F5.imprint","IMPRINT",FACE,{"disambiguationData":[TD([[makeQuery(id+"F5.imprint","IMPRINT",EDGE,{"disambiguationData":[TD([[subQ2,1.0]])],"derivedFrom":subQ0}),1.0]])]});}
            var Q287;
            {var subQ0=sQuery(id+"F5.wireOp",EDGE,"E12.1.127.0");var subQ1=makeQuery(id+"F3.boolean.opBoolean","COPY",EDGE,{"derivedFrom":makeQuery(id+"F3.opExtrude","CAP_EDGE",EDGE,{"disambiguationData":[OSD([sQuery(id+"F2.wireOp",EDGE,"E6")])],"isStart":true})});var subQ2=makeQuery(id+"F5.imprint","INTERSECT",VERTEX,{"disambiguationData":[OD(0.0)],"derivedFrom":[subQ1,subQ0]});Q287=makeQuery(id+"F5.imprint","IMPRINT",FACE,{"disambiguationData":[TD([[makeQuery(id+"F5.imprint","IMPRINT",EDGE,{"disambiguationData":[TD([[subQ2,1.0]])],"derivedFrom":subQ0}),1.0]])]});}
            var Q288;
            {var subQ0=sQuery(id+"F5.wireOp",EDGE,"E12.1.135.0");var subQ1=makeQuery(id+"F3.boolean.opBoolean","COPY",EDGE,{"derivedFrom":makeQuery(id+"F3.opExtrude","CAP_EDGE",EDGE,{"disambiguationData":[OSD([sQuery(id+"F2.wireOp",EDGE,"E6")])],"isStart":true})});var subQ2=makeQuery(id+"F5.imprint","INTERSECT",VERTEX,{"disambiguationData":[OD(0.0)],"derivedFrom":[subQ1,subQ0]});Q288=makeQuery(id+"F5.imprint","IMPRINT",FACE,{"disambiguationData":[TD([[makeQuery(id+"F5.imprint","IMPRINT",EDGE,{"disambiguationData":[TD([[subQ2,-1.0]])],"derivedFrom":subQ0}),1.0]])]});}
            var Q289;
            {var subQ0=sQuery(id+"F5.wireOp",EDGE,"E12.1.123.0");var subQ1=makeQuery(id+"F3.boolean.opBoolean","COPY",EDGE,{"derivedFrom":makeQuery(id+"F3.opExtrude","CAP_EDGE",EDGE,{"disambiguationData":[OSD([sQuery(id+"F2.wireOp",EDGE,"E6")])],"isStart":true})});var subQ2=makeQuery(id+"F5.imprint","INTERSECT",VERTEX,{"disambiguationData":[OD(0.0)],"derivedFrom":[subQ1,subQ0]});Q289=makeQuery(id+"F5.imprint","IMPRINT",FACE,{"disambiguationData":[TD([[makeQuery(id+"F5.imprint","IMPRINT",EDGE,{"disambiguationData":[TD([[subQ2,1.0]])],"derivedFrom":subQ0}),1.0]])]});}
            var Q290;
            {var subQ0=sQuery(id+"F5.wireOp",EDGE,"E12.1.139.0");var subQ1=makeQuery(id+"F3.boolean.opBoolean","COPY",EDGE,{"derivedFrom":makeQuery(id+"F3.opExtrude","CAP_EDGE",EDGE,{"disambiguationData":[OSD([sQuery(id+"F2.wireOp",EDGE,"E6")])],"isStart":true})});var subQ2=makeQuery(id+"F5.imprint","INTERSECT",VERTEX,{"disambiguationData":[OD(0.0)],"derivedFrom":[subQ1,subQ0]});Q290=makeQuery(id+"F5.imprint","IMPRINT",FACE,{"disambiguationData":[TD([[makeQuery(id+"F5.imprint","IMPRINT",EDGE,{"disambiguationData":[TD([[subQ2,-1.0]])],"derivedFrom":subQ0}),1.0]])]});}
            var Q291;
            {var subQ0=sQuery(id+"F5.wireOp",EDGE,"E12.1.139.0");var subQ1=makeQuery(id+"F3.boolean.opBoolean","COPY",EDGE,{"derivedFrom":makeQuery(id+"F3.opExtrude","CAP_EDGE",EDGE,{"disambiguationData":[OSD([sQuery(id+"F2.wireOp",EDGE,"E6")])],"isStart":true})});var subQ2=makeQuery(id+"F5.imprint","INTERSECT",VERTEX,{"disambiguationData":[OD(0.0)],"derivedFrom":[subQ1,subQ0]});Q291=makeQuery(id+"F5.imprint","IMPRINT",FACE,{"disambiguationData":[TD([[makeQuery(id+"F5.imprint","IMPRINT",EDGE,{"disambiguationData":[TD([[subQ2,1.0]])],"derivedFrom":subQ0}),1.0]])]});}
            var Q292;
            {var subQ0=sQuery(id+"F5.wireOp",EDGE,"E12.1.123.0");var subQ1=makeQuery(id+"F3.boolean.opBoolean","COPY",EDGE,{"derivedFrom":makeQuery(id+"F3.opExtrude","CAP_EDGE",EDGE,{"disambiguationData":[OSD([sQuery(id+"F2.wireOp",EDGE,"E6")])],"isStart":true})});var subQ2=makeQuery(id+"F5.imprint","INTERSECT",VERTEX,{"disambiguationData":[OD(0.0)],"derivedFrom":[subQ1,subQ0]});Q292=makeQuery(id+"F5.imprint","IMPRINT",FACE,{"disambiguationData":[TD([[makeQuery(id+"F5.imprint","IMPRINT",EDGE,{"disambiguationData":[TD([[subQ2,-1.0]])],"derivedFrom":subQ0}),1.0]])]});}
            var Q293;
            {var subQ0=sQuery(id+"F5.wireOp",EDGE,"E12.1.124.0");var subQ1=makeQuery(id+"F3.boolean.opBoolean","COPY",EDGE,{"derivedFrom":makeQuery(id+"F3.opExtrude","CAP_EDGE",EDGE,{"disambiguationData":[OSD([sQuery(id+"F2.wireOp",EDGE,"E6")])],"isStart":true})});var subQ2=makeQuery(id+"F5.imprint","INTERSECT",VERTEX,{"disambiguationData":[OD(0.0)],"derivedFrom":[subQ1,subQ0]});Q293=makeQuery(id+"F5.imprint","IMPRINT",FACE,{"disambiguationData":[TD([[makeQuery(id+"F5.imprint","IMPRINT",EDGE,{"disambiguationData":[TD([[subQ2,1.0]])],"derivedFrom":subQ0}),1.0]])]});}
            var Q294;
            {var subQ0=sQuery(id+"F5.wireOp",EDGE,"E12.1.149.0");var subQ1=makeQuery(id+"F3.boolean.opBoolean","COPY",EDGE,{"derivedFrom":makeQuery(id+"F3.opExtrude","CAP_EDGE",EDGE,{"disambiguationData":[OSD([sQuery(id+"F2.wireOp",EDGE,"E5")])],"isStart":true})});var subQ2=makeQuery(id+"F5.imprint","INTERSECT",VERTEX,{"derivedFrom":[subQ1,subQ0]});Q294=makeQuery(id+"F5.imprint","IMPRINT",FACE,{"disambiguationData":[TD([[makeQuery(id+"F5.imprint","IMPRINT",EDGE,{"disambiguationData":[TD([[subQ2,-1.0]])],"derivedFrom":subQ0}),1.0]])]});}
            var Q295;
            {var subQ0=sQuery(id+"F5.wireOp",EDGE,"E12.1.136.0");var subQ1=makeQuery(id+"F3.boolean.opBoolean","COPY",EDGE,{"derivedFrom":makeQuery(id+"F3.opExtrude","CAP_EDGE",EDGE,{"disambiguationData":[OSD([sQuery(id+"F2.wireOp",EDGE,"E6")])],"isStart":true})});var subQ2=makeQuery(id+"F5.imprint","INTERSECT",VERTEX,{"disambiguationData":[OD(0.0)],"derivedFrom":[subQ1,subQ0]});Q295=makeQuery(id+"F5.imprint","IMPRINT",FACE,{"disambiguationData":[TD([[makeQuery(id+"F5.imprint","IMPRINT",EDGE,{"disambiguationData":[TD([[subQ2,-1.0]])],"derivedFrom":subQ0}),1.0]])]});}
            var Q296;
            {var subQ0=sQuery(id+"F5.wireOp",EDGE,"E12.1.125.0");var subQ1=makeQuery(id+"F3.boolean.opBoolean","COPY",EDGE,{"derivedFrom":makeQuery(id+"F3.opExtrude","CAP_EDGE",EDGE,{"disambiguationData":[OSD([sQuery(id+"F2.wireOp",EDGE,"E6")])],"isStart":true})});var subQ2=makeQuery(id+"F5.imprint","INTERSECT",VERTEX,{"disambiguationData":[OD(0.0)],"derivedFrom":[subQ1,subQ0]});Q296=makeQuery(id+"F5.imprint","IMPRINT",FACE,{"disambiguationData":[TD([[makeQuery(id+"F5.imprint","IMPRINT",EDGE,{"disambiguationData":[TD([[subQ2,-1.0]])],"derivedFrom":subQ0}),1.0]])]});}
            var Q297;
            {var subQ0=sQuery(id+"F5.wireOp",EDGE,"E12.1.126.0");var subQ1=makeQuery(id+"F3.boolean.opBoolean","COPY",EDGE,{"derivedFrom":makeQuery(id+"F3.opExtrude","CAP_EDGE",EDGE,{"disambiguationData":[OSD([sQuery(id+"F2.wireOp",EDGE,"E6")])],"isStart":true})});var subQ2=makeQuery(id+"F5.imprint","INTERSECT",VERTEX,{"disambiguationData":[OD(0.0)],"derivedFrom":[subQ1,subQ0]});Q297=makeQuery(id+"F5.imprint","IMPRINT",FACE,{"disambiguationData":[TD([[makeQuery(id+"F5.imprint","IMPRINT",EDGE,{"disambiguationData":[TD([[subQ2,-1.0]])],"derivedFrom":subQ0}),1.0]])]});}
            var Q298;
            {var subQ0=sQuery(id+"F5.wireOp",EDGE,"E12.1.125.0");var subQ1=makeQuery(id+"F3.boolean.opBoolean","COPY",EDGE,{"derivedFrom":makeQuery(id+"F3.opExtrude","CAP_EDGE",EDGE,{"disambiguationData":[OSD([sQuery(id+"F2.wireOp",EDGE,"E6")])],"isStart":true})});var subQ2=makeQuery(id+"F5.imprint","INTERSECT",VERTEX,{"disambiguationData":[OD(0.0)],"derivedFrom":[subQ1,subQ0]});Q298=makeQuery(id+"F5.imprint","IMPRINT",FACE,{"disambiguationData":[TD([[makeQuery(id+"F5.imprint","IMPRINT",EDGE,{"disambiguationData":[TD([[subQ2,1.0]])],"derivedFrom":subQ0}),1.0]])]});}
            var Q299;
            {var subQ0=sQuery(id+"F5.wireOp",EDGE,"E12.1.149.0");var subQ1=makeQuery(id+"F3.boolean.opBoolean","COPY",EDGE,{"derivedFrom":makeQuery(id+"F3.opExtrude","CAP_EDGE",EDGE,{"disambiguationData":[OSD([sQuery(id+"F2.wireOp",EDGE,"E5")])],"isStart":true})});var subQ2=makeQuery(id+"F5.imprint","INTERSECT",VERTEX,{"derivedFrom":[subQ1,subQ0]});Q299=makeQuery(id+"F5.imprint","IMPRINT",FACE,{"disambiguationData":[TD([[makeQuery(id+"F5.imprint","IMPRINT",EDGE,{"disambiguationData":[TD([[subQ2,1.0]])],"derivedFrom":subQ0}),1.0]])]});}
            extrude(context, id + "F6", {"entities" : qUnion([Q0, Q1, Q2, Q3, Q4, Q5, Q6, Q7, Q8, Q9, Q10, Q11, Q12, Q13, Q14, Q15, Q16, Q17, Q18, Q19, Q20, Q21, Q22, Q23, Q24, Q25, Q26, Q27, Q28, Q29, Q30, Q31, Q32, Q33, Q34, Q35, Q36, Q37, Q38, Q39, Q40, Q41, Q42, Q43, Q44, Q45, Q46, Q47, Q48, Q49, Q50, Q51, Q52, Q53, Q54, Q55, Q56, Q57, Q58, Q59, Q60, Q61, Q62, Q63, Q64, Q65, Q66, Q67, Q68, Q69, Q70, Q71, Q72, Q73, Q74, Q75, Q76, Q77, Q78, Q79, Q80, Q81, Q82, Q83, Q84, Q85, Q86, Q87, Q88, Q89, Q90, Q91, Q92, Q93, Q94, Q95, Q96, Q97, Q98, Q99, Q100, Q101, Q102, Q103, Q104, Q105, Q106, Q107, Q108, Q109, Q110, Q111, Q112, Q113, Q114, Q115, Q116, Q117, Q118, Q119, Q120, Q121, Q122, Q123, Q124, Q125, Q126, Q127, Q128, Q129, Q130, Q131, Q132, Q133, Q134, Q135, Q136, Q137, Q138, Q139, Q140, Q141, Q142, Q143, Q144, Q145, Q146, Q147, Q148, Q149, Q150, Q151, Q152, Q153, Q154, Q155, Q156, Q157, Q158, Q159, Q160, Q161, Q162, Q163, Q164, Q165, Q166, Q167, Q168, Q169, Q170, Q171, Q172, Q173, Q174, Q175, Q176, Q177, Q178, Q179, Q180, Q181, Q182, Q183, Q184, Q185, Q186, Q187, Q188, Q189, Q190, Q191, Q192, Q193, Q194, Q195, Q196, Q197, Q198, Q199, Q200, Q201, Q202, Q203, Q204, Q205, Q206, Q207, Q208, Q209, Q210, Q211, Q212, Q213, Q214, Q215, Q216, Q217, Q218, Q219, Q220, Q221, Q222, Q223, Q224, Q225, Q226, Q227, Q228, Q229, Q230, Q231, Q232, Q233, Q234, Q235, Q236, Q237, Q238, Q239, Q240, Q241, Q242, Q243, Q244, Q245, Q246, Q247, Q248, Q249, Q250, Q251, Q252, Q253, Q254, Q255, Q256, Q257, Q258, Q259, Q260, Q261, Q262, Q263, Q264, Q265, Q266, Q267, Q268, Q269, Q270, Q271, Q272, Q273, Q274, Q275, Q276, Q277, Q278, Q279, Q280, Q281, Q282, Q283, Q284, Q285, Q286, Q287, Q288, Q289, Q290, Q291, Q292, Q293, Q294, Q295, Q296, Q297, Q298, Q299]), "operationType" : NewBodyOperationType.REMOVE, "endBound" : BoundingType.THROUGH_ALL, "oppositeDirection" : true, "depth" : 25 * mm});
        }
    });
